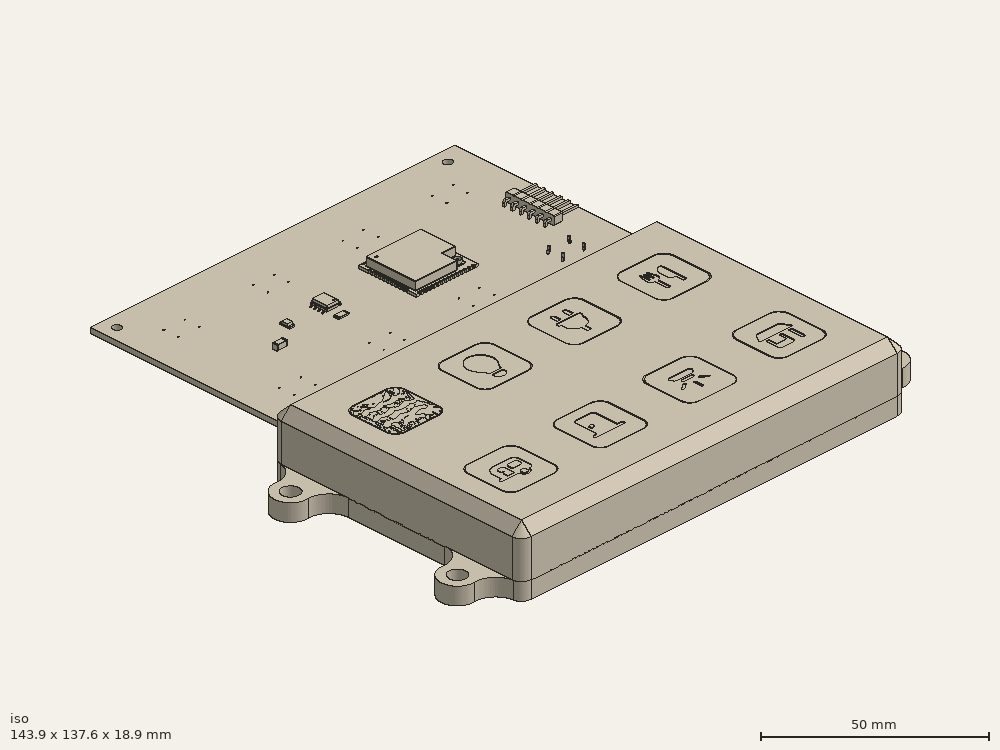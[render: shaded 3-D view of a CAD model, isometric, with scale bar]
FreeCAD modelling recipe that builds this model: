
FCSTD DOCUMENT  (FreeCAD 1.1R20260223 (Git shallow))
Label: trailer-switch-panel-eight-buttons
License: All rights reserved
LicenseURL: https://en.wikipedia.org/wiki/All_rights_reserved
objects: App::Link×73, Sketcher::SketchObject×42, Part::Feature×32, PartDesign::Pad×27, App::Point×24, PartDesign::Pocket×23, App::Part×12, PartDesign::Plane×11, PartDesign::Body×11, App::VarSet×9, PartDesign::Thickness×9, PartDesign::AdditivePipe×9, Part::Part2DObjectPython×8, PartDesign::SubShapeBinder×3, App::FeaturePython×3, PartDesign::CoordinateSystem×2, PartDesign::Mirrored×2, PartDesign::Fillet×2, Assembly::JointGroup×1, Assembly::AssemblyObject×1, +1 more types
note: 368 computed .brp shape members not serialized (recipe doc carries the construction recipe); baked Part::Feature solids carry a one-line shape summary decoded from their .brp

FEATURE [PartDesign::CoordinateSystem] Local_CS_cc27
  AttacherType = Attacher::AttachEngine3D
  MapMode = 2
FEATURE [Part::Feature] Pcb_cc27
  Placement = pos=(-24.2366,113.11,0) rot=(0,0,1;0rad)
  shape: bbox 113.4 x 65.77 x 1.6 mm, 60 faces (baked)
FEATURE [Sketcher::SketchObject] PCB_Sketch_cc27
  ArcFitTolerance = 1e-06
  ExternalTypes = [0]
  FullyConstrained = false
  MakeInternals = false
  sketch-geometry (8):
    g0: LineSegment StartX=0.45 StartY=65.81 StartZ=0 EndX=113.87 EndY=65.81 EndZ=0
    g1: LineSegment StartX=113.87 StartY=65.81 StartZ=0 EndX=113.87 EndY=0.04 EndZ=0
    g2: LineSegment StartX=113.87 StartY=0.04 StartZ=0 EndX=0.45 EndY=0.04 EndZ=0
    g3: LineSegment StartX=0.45 StartY=0.04 StartZ=0 EndX=0.45 EndY=65.81 EndZ=0
    g4: Circle CenterX=4.51408 CenterY=61.5799 CenterZ=0 NormalX=0 NormalY=0 NormalZ=1 AngleXU=0 Radius=1.25
    g5: Circle CenterX=107.514 CenterY=61.5799 CenterZ=0 NormalX=0 NormalY=0 NormalZ=1 AngleXU=0 Radius=1.25
    g6: Circle CenterX=107.514 CenterY=5.02733 CenterZ=0 NormalX=0 NormalY=0 NormalZ=1 AngleXU=0 Radius=1.25
    g7: Circle CenterX=4.51408 CenterY=5.02733 CenterZ=0 NormalX=0 NormalY=0 NormalZ=1 AngleXU=0 Radius=1.25
  constraints (4):
    c: Coincident(g2,g3)
    c: Coincident(g0,g3)
    c: Coincident(g1,g2)
    c: Coincident(g0,g1)
FEATURE [App::Part] Board_Geoms_cc27
  Group = -> [Pcb_cc27,PCB_Sketch_cc27]
  Origin = -> Origin
FEATURE [Part::Feature] Shape  label="C6_C_1206_3216Metric_fe8f5ab1829c"
  Placement = pos=(23.5634,30.042,0) rot=(0,0,1;3.14159rad)
  shape: bbox 3.2 x 1.6 x 1.6 mm, 28 faces (baked)
FEATURE [Part::Feature] Shape001  label="U1_ESP32-WROOM-32U_0b53285c672d"
  Placement = pos=(69.99,33.305,0) rot=(0,0,-1;1.5708rad)
  shape: bbox 19.2 x 18 x 3.2 mm, 766 faces (baked)
FEATURE [Part::Feature] Shape002  label="U2_SOIC_8_39x49mm_P127mm_6befcaffebcc"
  Placement = pos=(43.625,35.8786,0) rot=(0,0,1;3.14159rad)
  shape: bbox 6 x 4.9 x 1.75 mm, 156 faces (baked)
FEATURE [App::Link] C6_C_1206_3216Metric_fe8f5ab1829c_ln_  label="C5_C_1206_3216Metric_921661c36668"
  LinkPlacement = pos=(23.5634,32.484,0) rot=(0,0,1;3.14159rad)
  LinkedObject = -> Shape
  Placement = pos=(23.5634,32.484,0) rot=(0,0,1;3.14159rad)
FEATURE [App::Link] C6_C_1206_3216Metric_fe8f5ab1829c_ln_001  label="C4_C_1206_3216Metric_1d953bd43f95"
  LinkPlacement = pos=(18.375,36.646,0) rot=(0,0,1;0rad)
  LinkedObject = -> Shape
  Placement = pos=(18.375,36.646,0) rot=(0,0,1;0rad)
FEATURE [App::Link] C6_C_1206_3216Metric_fe8f5ab1829c_ln_002  label="C3_C_1206_3216Metric_0d3c0877bab4"
  LinkPlacement = pos=(18.375,29.28,0) rot=(0,0,1;0rad)
  LinkedObject = -> Shape
  Placement = pos=(18.375,29.28,0) rot=(0,0,1;0rad)
FEATURE [Part::Feature] Shape003  label="R4_R_1206_3216Metric_a98f0a8b4acf"
  Placement = pos=(42.97,30.25,0) rot=(0,0,1;3.14159rad)
  shape: bbox 3.2 x 1.6 x 0.55 mm, 26 faces (baked)
FEATURE [Part::Feature] Part__Feature  label="AP63203WU-7"
  shape: bbox 0.65 x 0.63 x 0.375 mm, 14 faces (baked)
FEATURE [Part::Feature] Part__Feature001  label="AP63203WU-008"
  shape: bbox 0.65 x 0.63 x 0.375 mm, 14 faces (baked)
FEATURE [Part::Feature] Part__Feature002  label="AP63203WU-009"
  shape: bbox 0.65 x 0.63 x 0.375 mm, 14 faces (baked)
FEATURE [Part::Feature] Part__Feature003  label="AP63203WU-010"
  shape: bbox 0.65 x 0.63 x 0.375 mm, 14 faces (baked)
FEATURE [Part::Feature] Part__Feature004  label="AP63203WU-011"
  shape: bbox 0.65 x 0.63 x 0.375 mm, 14 faces (baked)
FEATURE [Part::Feature] Part__Feature005  label="AP63203WU-012"
  shape: bbox 0.65 x 0.63 x 0.375 mm, 14 faces (baked)
FEATURE [Part::Feature] Part__Feature006  label="AP63203WU-013"
  shape: bbox 1.601 x 0.9 x 2.901 mm, 45 faces (baked)
FEATURE [Part::Feature] Part__Feature007  label="AP63203WU-014"
  shape: bbox 0.2 x 0.05 x 0.2 mm, 4 faces (baked)
FEATURE [App::Part] AP63203WU_7  label="IC1_AP63203WU-015_b8c35da43584"
  Group = -> [Part__Feature,Part__Feature001,Part__Feature002,Part__Feature003,Part__Feature004,Part__Feature005,Part__Feature006,Part__Feature007]
  Origin = -> Origin008
  Placement = pos=(18.126,32.96,0) rot=(1,0,0;1.5708rad)
FEATURE [App::Link] R4_R_1206_3216Metric_a98f0a8b4acf_ln_  label="R1_R_1206_3216Metric_0d48a55c24de"
  LinkPlacement = pos=(92.55,43.89,0) rot=(0,0,1;1.5708rad)
  LinkedObject = -> Shape003
  Placement = pos=(92.55,43.89,0) rot=(0,0,1;1.5708rad)
FEATURE [App::Link] C6_C_1206_3216Metric_fe8f5ab1829c_ln_003  label="C1_C_1206_3216Metric_20d4e43c8e49"
  LinkPlacement = pos=(85.52,41.17,0) rot=(0,0,1;3.14159rad)
  LinkedObject = -> Shape
  Placement = pos=(85.52,41.17,0) rot=(0,0,1;3.14159rad)
FEATURE [App::Link] R4_R_1206_3216Metric_a98f0a8b4acf_ln_001  label="R2_R_1206_3216Metric_7877a5f10d37"
  LinkPlacement = pos=(31.62,30.71,0) rot=(0,0,1;1.5708rad)
  LinkedObject = -> Shape003
  Placement = pos=(31.62,30.71,0) rot=(0,0,1;1.5708rad)
FEATURE [Part::Feature] Shape004  label="J1_PinHeader_1x06_P254mm_Horizontal_6c59025dd184"
  Placement = pos=(102.61,39.06,0) rot=(0,0,1;0rad)
  shape: bbox 10.36 x 15.24 x 5.54 mm, 166 faces (baked)
FEATURE [App::Link] C6_C_1206_3216Metric_fe8f5ab1829c_ln_004  label="C2_C_1206_3216Metric_1073df5edb1d"
  LinkPlacement = pos=(85.52,43.71,0) rot=(0,0,1;3.14159rad)
  LinkedObject = -> Shape
  Placement = pos=(85.52,43.71,0) rot=(0,0,1;3.14159rad)
FEATURE [Part::Feature] Shape005  label="D1_LED_1206_3216Metric_5818a68925bf"
  Placement = pos=(31.6022,35.7369,0) rot=(0,0,-1;1.5708rad)
  shape: bbox 1.6 x 3.2 x 1.1 mm, 50 faces (baked)
FEATURE [App::Link] R4_R_1206_3216Metric_a98f0a8b4acf_ln_002  label="R12_R_1206_3216Metric_9a77f9e92562"
  LinkPlacement = pos=(107.28,49.04,0) rot=(0,0,1;0rad)
  LinkedObject = -> Shape003
  Placement = pos=(107.28,49.04,0) rot=(0,0,1;0rad)
FEATURE [App::Part] Top_cc27
  Group = -> [Shape,Shape001,Shape002,C6_C_1206_3216Metric_fe8f5ab1829c_ln_,C6_C_1206_3216Metric_fe8f5ab1829c_ln_001,C6_C_1206_3216Metric_fe8f5ab1829c_ln_002,Shape003,AP63203WU_7,R4_R_1206_3216Metric_a98f0a8b4acf_ln_,C6_C_1206_3216Metric_fe8f5ab1829c_ln_003,R4_R_1206_3216Metric_a98f0a8b4acf_ln_001,Shape004,C6_C_1206_3216Metric_fe8f5ab1829c_ln_004,Shape005,R4_R_1206_3216Metric_a98f0a8b4acf_ln_002]
  Origin = -> Origin003
FEATURE [App::Link] R4_R_1206_3216Metric_a98f0a8b4acf_ln_003  label="R10_R_1206_3216Metric_955bf38eb66b"
  LinkPlacement = pos=(63.83,5.8,-1.6) rot=(1,0,0;3.14159rad)
  LinkedObject = -> Shape003
  Placement = pos=(63.83,5.8,-1.6) rot=(1,0,0;3.14159rad)
FEATURE [App::Link] D1_LED_1206_3216Metric_5818a68925bf_ln_  label="D7_LED_1206_3216Metric_e0f900cdbb9d"
  LinkPlacement = pos=(42.1175,5.8,-1.6) rot=(0,1,0;3.14159rad)
  LinkedObject = -> Shape005
  Placement = pos=(42.1175,5.8,-1.6) rot=(0,1,0;3.14159rad)
FEATURE [App::Link] D1_LED_1206_3216Metric_5818a68925bf_ln_001  label="D8_LED_1206_3216Metric_4590835c06e2"
  LinkPlacement = pos=(69.9575,5.8,-1.6) rot=(0,1,0;3.14159rad)
  LinkedObject = -> Shape005
  Placement = pos=(69.9575,5.8,-1.6) rot=(0,1,0;3.14159rad)
FEATURE [App::Link] R4_R_1206_3216Metric_a98f0a8b4acf_ln_004  label="R8_R_1206_3216Metric_c4d4031c6124"
  LinkPlacement = pos=(9.39,7.35,-1.6) rot=(0.707107,-0.707107,0;3.14159rad)
  LinkedObject = -> Shape003
  Placement = pos=(9.39,7.35,-1.6) rot=(0.707107,-0.707107,0;3.14159rad)
FEATURE [Part::Feature] Shape006  label="SW8_SW_PUSH_6mm_76d8f6a7f289"
  Placement = pos=(101.07,17.5,-1.6) rot=(0,1,0;3.14159rad)
  shape: bbox 7.174 x 6 x 7.8 mm, 105 faces (baked)
FEATURE [App::Link] R4_R_1206_3216Metric_a98f0a8b4acf_ln_005  label="R3_R_1206_3216Metric_c80006f71293"
  LinkPlacement = pos=(92.2,61.31,-1.6) rot=(1,0,0;3.14159rad)
  LinkedObject = -> Shape003
  Placement = pos=(92.2,61.31,-1.6) rot=(1,0,0;3.14159rad)
FEATURE [App::Link] R4_R_1206_3216Metric_a98f0a8b4acf_ln_006  label="R7_R_1206_3216Metric_6f705efabba0"
  LinkPlacement = pos=(20.25,61.26,-1.6) rot=(0,1,0;3.14159rad)
  LinkedObject = -> Shape003
  Placement = pos=(20.25,61.26,-1.6) rot=(0,1,0;3.14159rad)
FEATURE [App::Link] SW8_SW_PUSH_6mm_76d8f6a7f289_ln_  label="SW5_SW_PUSH_6mm_bc2679ab0c28"
  LinkPlacement = pos=(17.55,17.5,-1.6) rot=(0,1,0;3.14159rad)
  LinkedObject = -> Shape006
  Placement = pos=(17.55,17.5,-1.6) rot=(0,1,0;3.14159rad)
FEATURE [App::Link] D1_LED_1206_3216Metric_5818a68925bf_ln_002  label="D9_LED_1206_3216Metric_f97e9ca9ca0c"
  LinkPlacement = pos=(97.7975,5.8,-1.6) rot=(1,0,0;3.14159rad)
  LinkedObject = -> Shape005
  Placement = pos=(97.7975,5.8,-1.6) rot=(1,0,0;3.14159rad)
FEATURE [App::Link] R4_R_1206_3216Metric_a98f0a8b4acf_ln_007  label="R6_R_1206_3216Metric_4dd85524e60b"
  LinkPlacement = pos=(48.42,61.26,-1.6) rot=(0,1,0;3.14159rad)
  LinkedObject = -> Shape003
  Placement = pos=(48.42,61.26,-1.6) rot=(0,1,0;3.14159rad)
FEATURE [App::Link] R4_R_1206_3216Metric_a98f0a8b4acf_ln_008  label="R5_R_1206_3216Metric_5aff5c873fbb"
  LinkPlacement = pos=(75.86,61.27,-1.6) rot=(0,1,0;3.14159rad)
  LinkedObject = -> Shape003
  Placement = pos=(75.86,61.27,-1.6) rot=(0,1,0;3.14159rad)
FEATURE [App::Link] SW8_SW_PUSH_6mm_76d8f6a7f289_ln_001  label="SW7_SW_PUSH_6mm_98a993c83935"
  LinkPlacement = pos=(73.23,17.5,-1.6) rot=(0,1,0;3.14159rad)
  LinkedObject = -> Shape006
  Placement = pos=(73.23,17.5,-1.6) rot=(0,1,0;3.14159rad)
FEATURE [App::Link] SW8_SW_PUSH_6mm_76d8f6a7f289_ln_002  label="SW6_SW_PUSH_6mm_e97d2eab9daa"
  LinkPlacement = pos=(45.39,17.5,-1.6) rot=(0,1,0;3.14159rad)
  LinkedObject = -> Shape006
  Placement = pos=(45.39,17.5,-1.6) rot=(0,1,0;3.14159rad)
FEATURE [App::Link] D1_LED_1206_3216Metric_5818a68925bf_ln_003  label="D4_LED_1206_3216Metric_98b5ea636a78"
  LinkPlacement = pos=(42.1625,61.26,-1.6) rot=(1,0,0;3.14159rad)
  LinkedObject = -> Shape005
  Placement = pos=(42.1625,61.26,-1.6) rot=(1,0,0;3.14159rad)
FEATURE [App::Link] D1_LED_1206_3216Metric_5818a68925bf_ln_004  label="D2_LED_1206_3216Metric_2fa2df955063"
  LinkPlacement = pos=(97.7975,61.26,-1.6) rot=(0,1,0;3.14159rad)
  LinkedObject = -> Shape005
  Placement = pos=(97.7975,61.26,-1.6) rot=(0,1,0;3.14159rad)
FEATURE [App::Link] SW8_SW_PUSH_6mm_76d8f6a7f289_ln_003  label="SW2_SW_PUSH_6mm_e1b948049a03"
  LinkPlacement = pos=(66.73,49.03,-1.6) rot=(1,0,0;3.14159rad)
  LinkedObject = -> Shape006
  Placement = pos=(66.73,49.03,-1.6) rot=(1,0,0;3.14159rad)
FEATURE [App::Link] R4_R_1206_3216Metric_a98f0a8b4acf_ln_009  label="R11_R_1206_3216Metric_e90fbb06c50b"
  LinkPlacement = pos=(104,8.6,-1.6) rot=(0.707107,-0.707107,0;3.14159rad)
  LinkedObject = -> Shape003
  Placement = pos=(104,8.6,-1.6) rot=(0.707107,-0.707107,0;3.14159rad)
FEATURE [App::Link] SW8_SW_PUSH_6mm_76d8f6a7f289_ln_004  label="SW1_SW_PUSH_6mm_846872bf3f2a"
  LinkPlacement = pos=(94.57,49.03,-1.6) rot=(1,0,0;3.14159rad)
  LinkedObject = -> Shape006
  Placement = pos=(94.57,49.03,-1.6) rot=(1,0,0;3.14159rad)
FEATURE [App::Link] SW8_SW_PUSH_6mm_76d8f6a7f289_ln_005  label="SW3_SW_PUSH_6mm_786fe8b935ec"
  LinkPlacement = pos=(38.89,49.03,-1.6) rot=(1,0,0;3.14159rad)
  LinkedObject = -> Shape006
  Placement = pos=(38.89,49.03,-1.6) rot=(1,0,0;3.14159rad)
FEATURE [App::Link] D1_LED_1206_3216Metric_5818a68925bf_ln_005  label="D6_LED_1206_3216Metric_e89784457430"
  LinkPlacement = pos=(14.3225,5.8,-1.6) rot=(0,1,0;3.14159rad)
  LinkedObject = -> Shape005
  Placement = pos=(14.3225,5.8,-1.6) rot=(0,1,0;3.14159rad)
FEATURE [App::Link] D1_LED_1206_3216Metric_5818a68925bf_ln_006  label="D5_LED_1206_3216Metric_64f8a7d577f6"
  LinkPlacement = pos=(14.3225,61.26,-1.6) rot=(1,0,0;3.14159rad)
  LinkedObject = -> Shape005
  Placement = pos=(14.3225,61.26,-1.6) rot=(1,0,0;3.14159rad)
FEATURE [App::Link] D1_LED_1206_3216Metric_5818a68925bf_ln_007  label="D3_LED_1206_3216Metric_db0b37632ff3"
  LinkPlacement = pos=(70.0025,61.26,-1.6) rot=(1,0,0;3.14159rad)
  LinkedObject = -> Shape005
  Placement = pos=(70.0025,61.26,-1.6) rot=(1,0,0;3.14159rad)
FEATURE [App::Link] R4_R_1206_3216Metric_a98f0a8b4acf_ln_010  label="R9_R_1206_3216Metric_fd9422578c86"
  LinkPlacement = pos=(35.88,5.8,-1.6) rot=(1,0,0;3.14159rad)
  LinkedObject = -> Shape003
  Placement = pos=(35.88,5.8,-1.6) rot=(1,0,0;3.14159rad)
FEATURE [App::Link] SW8_SW_PUSH_6mm_76d8f6a7f289_ln_006  label="SW4_SW_PUSH_6mm_2c4766872f97"
  LinkPlacement = pos=(11.05,49.03,-1.6) rot=(1,0,0;3.14159rad)
  LinkedObject = -> Shape006
  Placement = pos=(11.05,49.03,-1.6) rot=(1,0,0;3.14159rad)
FEATURE [App::Part] Bot_cc27
  Group = -> [R4_R_1206_3216Metric_a98f0a8b4acf_ln_003,D1_LED_1206_3216Metric_5818a68925bf_ln_,D1_LED_1206_3216Metric_5818a68925bf_ln_001,R4_R_1206_3216Metric_a98f0a8b4acf_ln_004,Shape006,R4_R_1206_3216Metric_a98f0a8b4acf_ln_005,R4_R_1206_3216Metric_a98f0a8b4acf_ln_006,SW8_SW_PUSH_6mm_76d8f6a7f289_ln_,D1_LED_1206_3216Metric_5818a68925bf_ln_002,R4_R_1206_3216Metric_a98f0a8b4acf_ln_007,+14 more]
  Origin = -> Origin004
FEATURE [App::Part] Step_Models_cc27
  Group = -> [Top_cc27,Bot_cc27]
  Origin = -> Origin002
FEATURE [App::Part] Board_cc27  label="trailer-switch-panel-eight-buttons"
  Group = -> [Local_CS_cc27,Board_Geoms_cc27,Step_Models_cc27]
  Origin = -> Origin001
  Placement = pos=(0,0,0) rot=(1,0,0;3.14159rad)
FEATURE [PartDesign::SubShapeBinder] Binder006  label="BinderPcb001"
  BindCopyOnChange = 0
  BindMode = 0
  ClaimChildren = false
  Context = -> Body003 [Binder006.]
  Fuse = false
  MakeFace = true
  OffsetFill = false
  OffsetIntersection = false
  OffsetJoinType = 0
  OffsetOpenResult = false
  PartialLoad = false
  Placement = pos=(0,0,-3.64) rot=(0,0,1;0rad)
  Refine = true
  Relative = true
  Support = -> [Board_cc27]
  _Version = 2
FEATURE [Sketcher::SketchObject] Sketch033  label="SketchBackPlateToCover"
  ArcFitTolerance = 1e-06
  AttachmentSupport = -> [XY_Plane013]
  ExternalGeometry = -> [Binder006]
  ExternalTypes = [0]
  FullyConstrained = true
  MakeInternals = false
  MapMode = 5
  expr: Constraints[19] = <<VarSetButtonDimensions>>.Base_button_width + <<VarSetButtonDimensions>>.tolerance
  expr: Constraints[20] = <<VarSetButtonDimensions>>.Base_button_height + <<VarSetButtonDimensions>>.tolerance
  expr: Constraints[33] = <<VarSetButtonDimensions>>.Base_button_radius
  sketch-geometry (84):
    g0: LineSegment StartX=6.2 StartY=-10.05 StartZ=0 EndX=6.2 EndY=-20.45 EndZ=0
    g1: LineSegment StartX=9.2 StartY=-23.45 StartZ=0 EndX=19.6 EndY=-23.45 EndZ=0
    g2: LineSegment StartX=22.6 StartY=-20.45 StartZ=0 EndX=22.6 EndY=-10.05 EndZ=0
    g3: LineSegment StartX=19.6 StartY=-7.05 StartZ=0 EndX=9.2 EndY=-7.05 EndZ=0
    g4: ArcOfCircle CenterX=9.2 CenterY=-10.05 CenterZ=0 NormalX=0 NormalY=0 NormalZ=1 AngleXU=0 Radius=3 StartAngle=1.5708 EndAngle=3.14159
    g5: ArcOfCircle CenterX=9.2 CenterY=-20.45 CenterZ=0 NormalX=0 NormalY=0 NormalZ=1 AngleXU=0 Radius=3 StartAngle=3.14159 EndAngle=4.71239
    g6: ArcOfCircle CenterX=19.6 CenterY=-20.45 CenterZ=0 NormalX=0 NormalY=0 NormalZ=1 AngleXU=0 Radius=3 StartAngle=4.71239 EndAngle=6.28319
    g7: ArcOfCircle CenterX=19.6 CenterY=-10.05 CenterZ=0 NormalX=0 NormalY=0 NormalZ=1 AngleXU=0 Radius=3 StartAngle=6e-16 EndAngle=1.5708
    g8: GeomPoint [constr] X=6.2 Y=-7.05 Z=0
    g9: GeomPoint [constr] X=22.6 Y=-23.45 Z=0
    g10: LineSegment StartX=-3 StartY=6 StartZ=0 EndX=-3 EndY=-71.81 EndZ=0
    g11: LineSegment StartX=-3 StartY=-71.81 StartZ=0 EndX=116.87 EndY=-71.81 EndZ=0
    g12: LineSegment StartX=116.87 StartY=-71.81 StartZ=0 EndX=116.87 EndY=6 EndZ=0
    g13: LineSegment StartX=116.87 StartY=6 StartZ=0 EndX=-3 EndY=6 EndZ=0
    g14: LineSegment StartX=34.04 StartY=-10.05 StartZ=0 EndX=34.04 EndY=-20.45 EndZ=0
    g15: LineSegment StartX=37.04 StartY=-23.45 StartZ=0 EndX=47.44 EndY=-23.45 EndZ=0
    g16: LineSegment StartX=50.44 StartY=-20.45 StartZ=0 EndX=50.44 EndY=-10.05 EndZ=0
    g17: LineSegment StartX=47.44 StartY=-7.05 StartZ=0 EndX=37.04 EndY=-7.05 EndZ=0
    g18: ArcOfCircle CenterX=37.04 CenterY=-10.05 CenterZ=0 NormalX=0 NormalY=0 NormalZ=1 AngleXU=0 Radius=3 StartAngle=1.5708 EndAngle=3.14159
    g19: ArcOfCircle CenterX=37.04 CenterY=-20.45 CenterZ=0 NormalX=0 NormalY=0 NormalZ=1 AngleXU=0 Radius=3 StartAngle=3.14159 EndAngle=4.71239
    g20: ArcOfCircle CenterX=47.44 CenterY=-20.45 CenterZ=0 NormalX=0 NormalY=0 NormalZ=1 AngleXU=0 Radius=3 StartAngle=4.71239 EndAngle=6.28319
    g21: ArcOfCircle CenterX=47.44 CenterY=-10.05 CenterZ=0 NormalX=0 NormalY=0 NormalZ=1 AngleXU=0 Radius=3 StartAngle=0 EndAngle=1.5708
    g22: GeomPoint [constr] X=50.44 Y=-23.45 Z=0
    g23: GeomPoint [constr] X=42.24 Y=-15.25 Z=0
    g24: LineSegment StartX=61.88 StartY=-10.05 StartZ=0 EndX=61.88 EndY=-20.45 EndZ=0
    g25: LineSegment StartX=64.88 StartY=-23.45 StartZ=0 EndX=75.28 EndY=-23.45 EndZ=0
    g26: LineSegment StartX=78.28 StartY=-20.45 StartZ=0 EndX=78.28 EndY=-10.05 EndZ=0
    g27: LineSegment StartX=75.28 StartY=-7.05 StartZ=0 EndX=64.88 EndY=-7.05 EndZ=0
    g28: ArcOfCircle CenterX=64.88 CenterY=-10.05 CenterZ=0 NormalX=0 NormalY=0 NormalZ=1 AngleXU=0 Radius=3 StartAngle=1.5708 EndAngle=3.14159
    g29: ArcOfCircle CenterX=64.88 CenterY=-20.45 CenterZ=0 NormalX=0 NormalY=0 NormalZ=1 AngleXU=0 Radius=3 StartAngle=3.14159 EndAngle=4.71239
    g30: ArcOfCircle CenterX=75.28 CenterY=-20.45 CenterZ=0 NormalX=0 NormalY=0 NormalZ=1 AngleXU=0 Radius=3 StartAngle=4.71239 EndAngle=6.28319
    g31: ArcOfCircle CenterX=75.28 CenterY=-10.05 CenterZ=0 NormalX=0 NormalY=0 NormalZ=1 AngleXU=0 Radius=3 StartAngle=1e-16 EndAngle=1.5708
    g32: GeomPoint [constr] X=78.28 Y=-23.45 Z=0
    g33: GeomPoint [constr] X=70.08 Y=-15.25 Z=0
    g34: LineSegment StartX=89.72 StartY=-10.05 StartZ=0 EndX=89.72 EndY=-20.45 EndZ=0
    g35: LineSegment StartX=92.72 StartY=-23.45 StartZ=0 EndX=103.12 EndY=-23.45 EndZ=0
    g36: LineSegment StartX=106.12 StartY=-20.45 StartZ=0 EndX=106.12 EndY=-10.05 EndZ=0
    g37: LineSegment StartX=103.12 StartY=-7.05 StartZ=0 EndX=92.72 EndY=-7.05 EndZ=0
    g38: ArcOfCircle CenterX=92.72 CenterY=-10.05 CenterZ=0 NormalX=0 NormalY=0 NormalZ=1 AngleXU=0 Radius=3 StartAngle=1.5708 EndAngle=3.14159
    g39: ArcOfCircle CenterX=92.72 CenterY=-20.45 CenterZ=0 NormalX=0 NormalY=0 NormalZ=1 AngleXU=0 Radius=3 StartAngle=3.14159 EndAngle=4.71239
    g40: ArcOfCircle CenterX=103.12 CenterY=-20.45 CenterZ=0 NormalX=0 NormalY=0 NormalZ=1 AngleXU=0 Radius=3 StartAngle=4.71239 EndAngle=6.28319
    g41: ArcOfCircle CenterX=103.12 CenterY=-10.05 CenterZ=0 NormalX=0 NormalY=0 NormalZ=1 AngleXU=0 Radius=3 StartAngle=3e-16 EndAngle=1.5708
    g42: GeomPoint [constr] X=106.12 Y=-23.45 Z=0
    g43: GeomPoint [constr] X=97.92 Y=-15.25 Z=0
    g44: LineSegment StartX=6 StartY=-46.08 StartZ=0 EndX=6 EndY=-56.48 EndZ=0
    g45: LineSegment StartX=9 StartY=-59.48 StartZ=0 EndX=19.4 EndY=-59.48 EndZ=0
    g46: LineSegment StartX=22.4 StartY=-56.48 StartZ=0 EndX=22.4 EndY=-46.08 EndZ=0
    g47: LineSegment StartX=19.4 StartY=-43.08 StartZ=0 EndX=9 EndY=-43.08 EndZ=0
    g48: ArcOfCircle CenterX=9 CenterY=-46.08 CenterZ=0 NormalX=0 NormalY=0 NormalZ=1 AngleXU=0 Radius=3 StartAngle=1.5708 EndAngle=3.14159
    g49: ArcOfCircle CenterX=9 CenterY=-56.48 CenterZ=0 NormalX=0 NormalY=0 NormalZ=1 AngleXU=0 Radius=3 StartAngle=3.14159 EndAngle=4.71239
    g50: ArcOfCircle CenterX=19.4 CenterY=-56.48 CenterZ=0 NormalX=0 NormalY=0 NormalZ=1 AngleXU=0 Radius=3 StartAngle=4.71239 EndAngle=6.28319
    g51: ArcOfCircle CenterX=19.4 CenterY=-46.08 CenterZ=0 NormalX=0 NormalY=0 NormalZ=1 AngleXU=0 Radius=3 StartAngle=9e-16 EndAngle=1.5708
    g52: GeomPoint [constr] X=22.4 Y=-59.48 Z=0
    g53: GeomPoint [constr] X=14.2 Y=-51.28 Z=0
    g54: LineSegment StartX=33.84 StartY=-46.08 StartZ=0 EndX=33.84 EndY=-56.48 EndZ=0
    g55: LineSegment StartX=36.84 StartY=-59.48 StartZ=0 EndX=47.24 EndY=-59.48 EndZ=0
    g56: LineSegment StartX=50.24 StartY=-56.48 StartZ=0 EndX=50.24 EndY=-46.08 EndZ=0
    g57: LineSegment StartX=47.24 StartY=-43.08 StartZ=0 EndX=36.84 EndY=-43.08 EndZ=0
    g58: ArcOfCircle CenterX=36.84 CenterY=-46.08 CenterZ=0 NormalX=0 NormalY=0 NormalZ=1 AngleXU=0 Radius=3 StartAngle=1.5708 EndAngle=3.14159
    g59: ArcOfCircle CenterX=36.84 CenterY=-56.48 CenterZ=0 NormalX=0 NormalY=0 NormalZ=1 AngleXU=0 Radius=3 StartAngle=3.14159 EndAngle=4.71239
    g60: ArcOfCircle CenterX=47.24 CenterY=-56.48 CenterZ=0 NormalX=0 NormalY=0 NormalZ=1 AngleXU=0 Radius=3 StartAngle=4.71239 EndAngle=6.28319
    g61: ArcOfCircle CenterX=47.24 CenterY=-46.08 CenterZ=0 NormalX=0 NormalY=0 NormalZ=1 AngleXU=0 Radius=3 StartAngle=7e-16 EndAngle=1.5708
    g62: GeomPoint [constr] X=50.24 Y=-59.48 Z=0
    g63: GeomPoint [constr] X=42.04 Y=-51.28 Z=0
    g64: LineSegment StartX=61.68 StartY=-46.08 StartZ=0 EndX=61.68 EndY=-56.48 EndZ=0
    g65: LineSegment StartX=64.68 StartY=-59.48 StartZ=0 EndX=75.08 EndY=-59.48 EndZ=0
    g66: LineSegment StartX=78.08 StartY=-56.48 StartZ=0 EndX=78.08 EndY=-46.08 EndZ=0
    g67: LineSegment StartX=75.08 StartY=-43.08 StartZ=0 EndX=64.68 EndY=-43.08 EndZ=0
    g68: ArcOfCircle CenterX=64.68 CenterY=-46.08 CenterZ=0 NormalX=0 NormalY=0 NormalZ=1 AngleXU=0 Radius=3 StartAngle=1.5708 EndAngle=3.14159
    g69: ArcOfCircle CenterX=64.68 CenterY=-56.48 CenterZ=0 NormalX=0 NormalY=0 NormalZ=1 AngleXU=0 Radius=3 StartAngle=3.14159 EndAngle=4.71239
    g70: ArcOfCircle CenterX=75.08 CenterY=-56.48 CenterZ=0 NormalX=0 NormalY=0 NormalZ=1 AngleXU=0 Radius=3 StartAngle=4.71239 EndAngle=6.28319
    g71: ArcOfCircle CenterX=75.08 CenterY=-46.08 CenterZ=0 NormalX=0 NormalY=0 NormalZ=1 AngleXU=0 Radius=3 StartAngle=9e-16 EndAngle=1.5708
    g72: GeomPoint [constr] X=78.08 Y=-59.48 Z=0
    g73: GeomPoint [constr] X=69.88 Y=-51.28 Z=0
    g74: LineSegment StartX=89.52 StartY=-46.08 StartZ=0 EndX=89.52 EndY=-56.48 EndZ=0
    g75: LineSegment StartX=92.52 StartY=-59.48 StartZ=0 EndX=102.92 EndY=-59.48 EndZ=0
    g76: LineSegment StartX=105.92 StartY=-56.48 StartZ=0 EndX=105.92 EndY=-46.08 EndZ=0
    g77: LineSegment StartX=102.92 StartY=-43.08 StartZ=0 EndX=92.52 EndY=-43.08 EndZ=0
    g78: ArcOfCircle CenterX=92.52 CenterY=-46.08 CenterZ=0 NormalX=0 NormalY=0 NormalZ=1 AngleXU=0 Radius=3 StartAngle=1.5708 EndAngle=3.14159
    g79: ArcOfCircle CenterX=92.52 CenterY=-56.48 CenterZ=0 NormalX=0 NormalY=0 NormalZ=1 AngleXU=0 Radius=3 StartAngle=3.14159 EndAngle=4.71239
    g80: ArcOfCircle CenterX=102.92 CenterY=-56.48 CenterZ=0 NormalX=0 NormalY=0 NormalZ=1 AngleXU=0 Radius=3 StartAngle=4.71239 EndAngle=6.28319
    g81: ArcOfCircle CenterX=102.92 CenterY=-46.08 CenterZ=0 NormalX=0 NormalY=0 NormalZ=1 AngleXU=0 Radius=3 StartAngle=6e-16 EndAngle=1.5708
    g82: GeomPoint [constr] X=105.92 Y=-59.48 Z=0
    g83: GeomPoint [constr] X=97.72 Y=-51.28 Z=0
  constraints (189):
    c: Tangent(g0,g4) = -1.5708
    c: Tangent(g0,g5) = -1.5708
    c: Tangent(g1,g5) = -1.5708
    c: Tangent(g1,g6) = -1.5708
    c: Tangent(g2,g6) = -1.5708
    c: Tangent(g2,g7) = -1.5708
    c: Tangent(g3,g7) = -1.5708
    c: Tangent(g3,g4) = -1.5708
    c: Vertical(g0)
    c: Vertical(g2)
    c: Horizontal(g1)
    c: Horizontal(g3)
    c: Equal(g4,g5)
    c: Equal(g5,g6)
    c: Equal(g6,g7)
    c: PointOnObject(g8,g0)
    c: PointOnObject(g8,g3)
    c: PointOnObject(g9,g1)
    c: PointOnObject(g9,g2)
    c: Distance(g0,g2) = 16.4
    c: Distance(g1,g3) = 16.4
    c: Coincident(g10,g11)
    c: Coincident(g11,g12)
    c: Coincident(g12,g13)
    c: Coincident(g13,g10)
    c: Vertical(g10)
    c: Vertical(g12)
    c: Horizontal(g11)
    c: Horizontal(g13)
    c: DistanceX(g10,g-1) = 3
    c: DistanceY(g-1,g10) = 6
    c: DistanceX(g-5,g11) = 3
    c: DistanceY(g11,g-5) = 6
    c: Radius(g7) = 3
    c: Symmetric(g4,g6,g-7)
    c: Tangent(g14,g18) = -1.5708
    c: Tangent(g14,g19) = -1.5708
    c: Tangent(g15,g19) = -1.5708
    c: Tangent(g15,g20) = -1.5708
    c: Tangent(g16,g20) = -1.5708
    c: Tangent(g16,g21) = -1.5708
    c: Tangent(g17,g21) = -1.5708
    c: Tangent(g17,g18) = -1.5708
    c: Vertical(g14)
    c: Vertical(g16)
    c: Horizontal(g15)
    c: Horizontal(g17)
    c: Equal(g18,g19)
    c: Equal(g19,g20)
    c: Equal(g20,g21)
    c: Symmetric(g16,g14,g23)
    c: PointOnObject(g22,g15)
    c: PointOnObject(g22,g16)
    c: Coincident(g23,g-8)
    c: Tangent(g24,g28) = -1.5708
    c: Tangent(g24,g29) = -1.5708
    c: Tangent(g25,g29) = -1.5708
    c: Tangent(g25,g30) = -1.5708
    c: Tangent(g26,g30) = -1.5708
    c: Tangent(g26,g31) = -1.5708
    c: Tangent(g27,g31) = -1.5708
    c: Tangent(g27,g28) = -1.5708
    c: Vertical(g24)
    c: Vertical(g26)
    c: Horizontal(g25)
    c: Horizontal(g27)
    c: Equal(g28,g29)
    c: Equal(g29,g30)
    c: Equal(g30,g31)
    c: Symmetric(g26,g24,g33)
    c: PointOnObject(g32,g25)
    c: PointOnObject(g32,g26)
    c: Coincident(g33,g-9)
    c: Tangent(g34,g38) = -1.5708
    c: Tangent(g34,g39) = -1.5708
    c: Tangent(g35,g39) = -1.5708
    c: Tangent(g35,g40) = -1.5708
    c: Tangent(g36,g40) = -1.5708
    c: Tangent(g36,g41) = -1.5708
    c: Tangent(g37,g41) = -1.5708
    c: Tangent(g37,g38) = -1.5708
    c: Vertical(g34)
    c: Vertical(g36)
    c: Horizontal(g35)
    c: Horizontal(g37)
    c: Equal(g38,g39)
    c: Equal(g39,g40)
    c: Equal(g40,g41)
    c: Symmetric(g36,g34,g43)
    c: PointOnObject(g42,g35)
    c: PointOnObject(g42,g36)
    c: Coincident(g43,g-10)
    c: Tangent(g44,g48) = -1.5708
    c: Tangent(g44,g49) = -1.5708
    c: Tangent(g45,g49) = -1.5708
    c: Tangent(g45,g50) = -1.5708
    c: Tangent(g46,g50) = -1.5708
    c: Tangent(g46,g51) = -1.5708
    c: Tangent(g47,g51) = -1.5708
    c: Tangent(g47,g48) = -1.5708
    c: Vertical(g44)
    c: Vertical(g46)
    c: Horizontal(g45)
    c: Horizontal(g47)
    c: Equal(g48,g49)
    c: Equal(g49,g50)
    c: Equal(g50,g51)
    c: Symmetric(g46,g44,g53)
    c: PointOnObject(g52,g45)
    c: PointOnObject(g52,g46)
    c: Coincident(g53,g-14)
    c: Tangent(g54,g58) = -1.5708
    c: Tangent(g54,g59) = -1.5708
    c: Tangent(g55,g59) = -1.5708
    c: Tangent(g55,g60) = -1.5708
    c: Tangent(g56,g60) = -1.5708
    c: Tangent(g56,g61) = -1.5708
    c: Tangent(g57,g61) = -1.5708
    c: Tangent(g57,g58) = -1.5708
    c: Vertical(g54)
    c: Vertical(g56)
    c: Horizontal(g55)
    c: Horizontal(g57)
    c: Equal(g58,g59)
    c: Equal(g59,g60)
    c: Equal(g60,g61)
    c: Symmetric(g56,g54,g63)
    c: PointOnObject(g62,g55)
    c: PointOnObject(g62,g56)
    c: Coincident(g63,g-13)
    c: Tangent(g64,g68) = -1.5708
    c: Tangent(g64,g69) = -1.5708
    c: Tangent(g65,g69) = -1.5708
    c: Tangent(g65,g70) = -1.5708
    c: Tangent(g66,g70) = -1.5708
    c: Tangent(g66,g71) = -1.5708
    c: Tangent(g67,g71) = -1.5708
    c: Tangent(g67,g68) = -1.5708
    c: Vertical(g64)
    c: Vertical(g66)
    c: Horizontal(g65)
    c: Horizontal(g67)
    c: Equal(g68,g69)
    c: Equal(g69,g70)
    c: Equal(g70,g71)
    c: Symmetric(g66,g64,g73)
    c: PointOnObject(g72,g65)
    c: PointOnObject(g72,g66)
    c: Coincident(g73,g-12)
    c: Tangent(g74,g78) = -1.5708
    c: Tangent(g74,g79) = -1.5708
    c: Tangent(g75,g79) = -1.5708
    c: Tangent(g75,g80) = -1.5708
    c: Tangent(g76,g80) = -1.5708
    c: Tangent(g76,g81) = -1.5708
    c: Tangent(g77,g81) = -1.5708
    c: Tangent(g77,g78) = -1.5708
    c: Vertical(g74)
    c: Vertical(g76)
    c: Horizontal(g75)
    c: Horizontal(g77)
    c: Equal(g78,g79)
    c: Equal(g79,g80)
    c: Equal(g80,g81)
    c: Symmetric(g76,g74,g83)
    c: PointOnObject(g82,g75)
    c: PointOnObject(g82,g76)
    c: Coincident(g83,g-11)
    c: Equal(g4,g18)
    c: Equal(g18,g48)
    c: Equal(g48,g58)
    c: Equal(g58,g68)
    c: Equal(g68,g28)
    c: Equal(g28,g38)
    c: Equal(g38,g78)
    c: Equal(g2,g16)
    c: Equal(g16,g26)
    c: Equal(g26,g36)
    c: Equal(g36,g76)
    c: Equal(g76,g66)
    c: Equal(g66,g56)
    c: Equal(g56,g46)
    c: Equal(g3,g17)
    c: Equal(g17,g27)
    c: Equal(g27,g37)
    c: Equal(g37,g77)
    c: Equal(g77,g67)
    c: Equal(g67,g57)
    c: Equal(g57,g47)
FEATURE [App::VarSet] VarSet002  label="VarSetButtonDimensions"
  Base_base_thickness = 1.5
  Base_button_height = 16
  Base_button_radius = 3
  Base_button_slide_depth = 0.09
  Base_button_width = 16
  button_cap_height = 3
  button_cap_wall_thickness = 1.5
  button_snap_thickness = 0.5
  button_tab_depth = 1
  tolerance = 0.4
FEATURE [PartDesign::Pad] Pad024  label="PadOuterWalls"
  Direction = (0,0,1)
  Length = 1.5
  Length2 = 10
  Profile = -> Sketch033
  ReferenceAxis = -> Sketch033 [N_Axis]
  Refine = true
  SideType = 0
  Suppressed = false
  Type = 0
  Type2 = 0
  expr: Length = <<VarSetButtonDimensions>>.Base_base_thickness
FEATURE [Sketcher::SketchObject] Sketch034  label="SketchButtonSlide"
  ArcFitTolerance = 1e-06
  AttachmentSupport = -> [Pad024]
  ExternalGeometry = -> [Pad024]
  ExternalTypes = [0]
  FullyConstrained = true
  MakeInternals = false
  MapMode = 5
  Placement = pos=(0,0,1.5) rot=(0,0,1;0rad)
  expr: Constraints[29] = <<VarSetButtonDimensions>>.Base_button_radius
  expr: Constraints[30] = <<VarSetButtonDimensions>>.Base_button_width + <<VarSetButtonDimensions>>.tolerance + <<VarSetButtonDimensions>>.button_snap_thickness * 2 + <<VarSetButtonDimensions>>.button_tab_depth
  expr: Constraints[31] = <<VarSetButtonDimensions>>.Base_button_width + <<VarSetButtonDimensions>>.tolerance + <<VarSetButtonDimensions>>.button_snap_thickness * 2 + <<VarSetButtonDimensions>>.button_tab_depth
  sketch-geometry (93):
    g0: LineSegment StartX=-3 StartY=6 StartZ=0 EndX=-3 EndY=-71.81 EndZ=0
    g1: LineSegment StartX=-3 StartY=-71.81 StartZ=0 EndX=116.87 EndY=-71.81 EndZ=0
    g2: LineSegment StartX=116.87 StartY=-71.81 StartZ=0 EndX=116.87 EndY=6 EndZ=0
    g3: LineSegment StartX=116.87 StartY=6 StartZ=0 EndX=-3 EndY=6 EndZ=0
    g4: LineSegment StartX=5.2 StartY=-9.05 StartZ=0 EndX=5.2 EndY=-21.45 EndZ=0
    g5: LineSegment StartX=8.2 StartY=-24.45 StartZ=0 EndX=20.6 EndY=-24.45 EndZ=0
    g6: LineSegment StartX=23.6 StartY=-21.45 StartZ=0 EndX=23.6 EndY=-9.05 EndZ=0
    g7: LineSegment StartX=20.6 StartY=-6.05 StartZ=0 EndX=8.2 EndY=-6.05 EndZ=0
    g8: ArcOfCircle CenterX=8.2 CenterY=-9.05 CenterZ=0 NormalX=0 NormalY=0 NormalZ=1 AngleXU=0 Radius=3 StartAngle=1.5708 EndAngle=3.14159
    g9: ArcOfCircle CenterX=8.2 CenterY=-21.45 CenterZ=0 NormalX=0 NormalY=0 NormalZ=1 AngleXU=0 Radius=3 StartAngle=3.14159 EndAngle=4.71239
    g10: ArcOfCircle CenterX=20.6 CenterY=-21.45 CenterZ=0 NormalX=0 NormalY=0 NormalZ=1 AngleXU=0 Radius=3 StartAngle=4.71239 EndAngle=6.28319
    g11: ArcOfCircle CenterX=20.6 CenterY=-9.05 CenterZ=0 NormalX=0 NormalY=0 NormalZ=1 AngleXU=0 Radius=3 StartAngle=0 EndAngle=1.5708
    g12: GeomPoint [constr] X=5.2 Y=-6.05 Z=0
    g13: GeomPoint [constr] X=23.6 Y=-24.45 Z=0
    g14: GeomPoint X=14.4 Y=-15.25 Z=0
    g15: GeomPoint X=14.4 Y=-15.25 Z=0
    g16: LineSegment StartX=33.04 StartY=-9.05 StartZ=0 EndX=33.04 EndY=-21.45 EndZ=0
    g17: LineSegment StartX=36.04 StartY=-24.45 StartZ=0 EndX=48.44 EndY=-24.45 EndZ=0
    g18: LineSegment StartX=51.44 StartY=-21.45 StartZ=0 EndX=51.44 EndY=-9.05 EndZ=0
    g19: LineSegment StartX=48.44 StartY=-6.05 StartZ=0 EndX=36.04 EndY=-6.05 EndZ=0
    g20: ArcOfCircle CenterX=36.04 CenterY=-9.05 CenterZ=0 NormalX=0 NormalY=0 NormalZ=1 AngleXU=0 Radius=3 StartAngle=1.5708 EndAngle=3.14159
    g21: ArcOfCircle CenterX=36.04 CenterY=-21.45 CenterZ=0 NormalX=0 NormalY=0 NormalZ=1 AngleXU=0 Radius=3 StartAngle=3.14159 EndAngle=4.71239
    g22: ArcOfCircle CenterX=48.44 CenterY=-21.45 CenterZ=0 NormalX=0 NormalY=0 NormalZ=1 AngleXU=0 Radius=3 StartAngle=4.71239 EndAngle=6.28319
    g23: ArcOfCircle CenterX=48.44 CenterY=-9.05 CenterZ=0 NormalX=0 NormalY=0 NormalZ=1 AngleXU=0 Radius=3 StartAngle=0 EndAngle=1.5708
    g24: GeomPoint [constr] X=33.04 Y=-6.05 Z=0
    g25: GeomPoint [constr] X=51.44 Y=-24.45 Z=0
    g26: LineSegment StartX=60.88 StartY=-9.05 StartZ=0 EndX=60.88 EndY=-21.45 EndZ=0
    g27: LineSegment StartX=63.88 StartY=-24.45 StartZ=0 EndX=76.28 EndY=-24.45 EndZ=0
    g28: LineSegment StartX=79.28 StartY=-21.45 StartZ=0 EndX=79.28 EndY=-9.05 EndZ=0
    g29: LineSegment StartX=76.28 StartY=-6.05 StartZ=0 EndX=63.88 EndY=-6.05 EndZ=0
    g30: ArcOfCircle CenterX=63.88 CenterY=-9.05 CenterZ=0 NormalX=0 NormalY=0 NormalZ=1 AngleXU=0 Radius=3 StartAngle=1.5708 EndAngle=3.14159
    g31: ArcOfCircle CenterX=63.88 CenterY=-21.45 CenterZ=0 NormalX=0 NormalY=0 NormalZ=1 AngleXU=0 Radius=3 StartAngle=3.14159 EndAngle=4.71239
    g32: ArcOfCircle CenterX=76.28 CenterY=-21.45 CenterZ=0 NormalX=0 NormalY=0 NormalZ=1 AngleXU=0 Radius=3 StartAngle=4.71239 EndAngle=6.28319
    g33: ArcOfCircle CenterX=76.28 CenterY=-9.05 CenterZ=0 NormalX=0 NormalY=0 NormalZ=1 AngleXU=0 Radius=3 StartAngle=0 EndAngle=1.5708
    g34: GeomPoint [constr] X=60.88 Y=-6.05 Z=0
    g35: GeomPoint [constr] X=79.28 Y=-24.45 Z=0
    g36: LineSegment StartX=88.72 StartY=-9.05 StartZ=0 EndX=88.72 EndY=-21.45 EndZ=0
    g37: LineSegment StartX=91.72 StartY=-24.45 StartZ=0 EndX=104.12 EndY=-24.45 EndZ=0
    g38: LineSegment StartX=107.12 StartY=-21.45 StartZ=0 EndX=107.12 EndY=-9.05 EndZ=0
    g39: LineSegment StartX=104.12 StartY=-6.05 StartZ=0 EndX=91.72 EndY=-6.05 EndZ=0
    g40: ArcOfCircle CenterX=91.72 CenterY=-9.05 CenterZ=0 NormalX=0 NormalY=0 NormalZ=1 AngleXU=0 Radius=3 StartAngle=1.5708 EndAngle=3.14159
    g41: ArcOfCircle CenterX=91.72 CenterY=-21.45 CenterZ=0 NormalX=0 NormalY=0 NormalZ=1 AngleXU=0 Radius=3 StartAngle=3.14159 EndAngle=4.71239
    g42: ArcOfCircle CenterX=104.12 CenterY=-21.45 CenterZ=0 NormalX=0 NormalY=0 NormalZ=1 AngleXU=0 Radius=3 StartAngle=4.71239 EndAngle=6.28319
    g43: ArcOfCircle CenterX=104.12 CenterY=-9.05 CenterZ=0 NormalX=0 NormalY=0 NormalZ=1 AngleXU=0 Radius=3 StartAngle=0 EndAngle=1.5708
    g44: GeomPoint [constr] X=88.72 Y=-6.05 Z=0
    g45: GeomPoint [constr] X=107.12 Y=-24.45 Z=0
    g46: LineSegment StartX=88.52 StartY=-45.08 StartZ=0 EndX=88.52 EndY=-57.48 EndZ=0
    g47: LineSegment StartX=91.52 StartY=-60.48 StartZ=0 EndX=103.92 EndY=-60.48 EndZ=0
    g48: LineSegment StartX=106.92 StartY=-57.48 StartZ=0 EndX=106.92 EndY=-45.08 EndZ=0
    g49: LineSegment StartX=103.92 StartY=-42.08 StartZ=0 EndX=91.52 EndY=-42.08 EndZ=0
    g50: ArcOfCircle CenterX=91.52 CenterY=-45.08 CenterZ=0 NormalX=0 NormalY=0 NormalZ=1 AngleXU=0 Radius=3 StartAngle=1.5708 EndAngle=3.14159
    g51: ArcOfCircle CenterX=91.52 CenterY=-57.48 CenterZ=0 NormalX=0 NormalY=0 NormalZ=1 AngleXU=0 Radius=3 StartAngle=3.14159 EndAngle=4.71239
    g52: ArcOfCircle CenterX=103.92 CenterY=-57.48 CenterZ=0 NormalX=0 NormalY=0 NormalZ=1 AngleXU=0 Radius=3 StartAngle=4.71239 EndAngle=6.28319
    g53: ArcOfCircle CenterX=103.92 CenterY=-45.08 CenterZ=0 NormalX=0 NormalY=0 NormalZ=1 AngleXU=0 Radius=3 StartAngle=0 EndAngle=1.5708
    g54: GeomPoint [constr] X=88.52 Y=-42.08 Z=0
    g55: GeomPoint [constr] X=106.92 Y=-60.48 Z=0
    g56: LineSegment StartX=60.68 StartY=-45.08 StartZ=0 EndX=60.68 EndY=-57.48 EndZ=0
    g57: LineSegment StartX=63.68 StartY=-60.48 StartZ=0 EndX=76.08 EndY=-60.48 EndZ=0
    g58: LineSegment StartX=79.08 StartY=-57.48 StartZ=0 EndX=79.08 EndY=-45.08 EndZ=0
    g59: LineSegment StartX=76.08 StartY=-42.08 StartZ=0 EndX=63.68 EndY=-42.08 EndZ=0
    g60: ArcOfCircle CenterX=63.68 CenterY=-45.08 CenterZ=0 NormalX=0 NormalY=0 NormalZ=1 AngleXU=0 Radius=3 StartAngle=1.5708 EndAngle=3.14159
    g61: ArcOfCircle CenterX=63.68 CenterY=-57.48 CenterZ=0 NormalX=0 NormalY=0 NormalZ=1 AngleXU=0 Radius=3 StartAngle=3.14159 EndAngle=4.71239
    g62: ArcOfCircle CenterX=76.08 CenterY=-57.48 CenterZ=0 NormalX=0 NormalY=0 NormalZ=1 AngleXU=0 Radius=3 StartAngle=4.71239 EndAngle=6.28319
    g63: ArcOfCircle CenterX=76.08 CenterY=-45.08 CenterZ=0 NormalX=0 NormalY=0 NormalZ=1 AngleXU=0 Radius=3 StartAngle=0 EndAngle=1.5708
    g64: GeomPoint [constr] X=60.68 Y=-42.08 Z=0
    g65: GeomPoint [constr] X=79.08 Y=-60.48 Z=0
    g66: LineSegment StartX=32.84 StartY=-45.08 StartZ=0 EndX=32.84 EndY=-57.48 EndZ=0
    g67: LineSegment StartX=35.84 StartY=-60.48 StartZ=0 EndX=48.24 EndY=-60.48 EndZ=0
    g68: LineSegment StartX=51.24 StartY=-57.48 StartZ=0 EndX=51.24 EndY=-45.08 EndZ=0
    g69: LineSegment StartX=48.24 StartY=-42.08 StartZ=0 EndX=35.84 EndY=-42.08 EndZ=0
    g70: ArcOfCircle CenterX=35.84 CenterY=-45.08 CenterZ=0 NormalX=0 NormalY=0 NormalZ=1 AngleXU=0 Radius=3 StartAngle=1.5708 EndAngle=3.14159
    g71: ArcOfCircle CenterX=35.84 CenterY=-57.48 CenterZ=0 NormalX=0 NormalY=0 NormalZ=1 AngleXU=0 Radius=3 StartAngle=3.14159 EndAngle=4.71239
    g72: ArcOfCircle CenterX=48.24 CenterY=-57.48 CenterZ=0 NormalX=0 NormalY=0 NormalZ=1 AngleXU=0 Radius=3 StartAngle=4.71239 EndAngle=6.28319
    g73: ArcOfCircle CenterX=48.24 CenterY=-45.08 CenterZ=0 NormalX=0 NormalY=0 NormalZ=1 AngleXU=0 Radius=3 StartAngle=0 EndAngle=1.5708
    g74: GeomPoint [constr] X=32.84 Y=-42.08 Z=0
    g75: GeomPoint [constr] X=51.24 Y=-60.48 Z=0
    g76: LineSegment StartX=5 StartY=-45.08 StartZ=0 EndX=5 EndY=-57.48 EndZ=0
    g77: LineSegment StartX=8 StartY=-60.48 StartZ=0 EndX=20.4 EndY=-60.48 EndZ=0
    g78: LineSegment StartX=23.4 StartY=-57.48 StartZ=0 EndX=23.4 EndY=-45.08 EndZ=0
    g79: LineSegment StartX=20.4 StartY=-42.08 StartZ=0 EndX=8 EndY=-42.08 EndZ=0
    g80: ArcOfCircle CenterX=8 CenterY=-45.08 CenterZ=0 NormalX=0 NormalY=0 NormalZ=1 AngleXU=0 Radius=3 StartAngle=1.5708 EndAngle=3.14159
    g81: ArcOfCircle CenterX=8 CenterY=-57.48 CenterZ=0 NormalX=0 NormalY=0 NormalZ=1 AngleXU=0 Radius=3 StartAngle=3.14159 EndAngle=4.71239
    g82: ArcOfCircle CenterX=20.4 CenterY=-57.48 CenterZ=0 NormalX=0 NormalY=0 NormalZ=1 AngleXU=0 Radius=3 StartAngle=4.71239 EndAngle=6.28319
    g83: ArcOfCircle CenterX=20.4 CenterY=-45.08 CenterZ=0 NormalX=0 NormalY=0 NormalZ=1 AngleXU=0 Radius=3 StartAngle=7e-16 EndAngle=1.5708
    g84: GeomPoint [constr] X=5 Y=-42.08 Z=0
    g85: GeomPoint [constr] X=23.4 Y=-60.48 Z=0
    g86: GeomPoint X=42.24 Y=-15.25 Z=0
    g87: GeomPoint X=70.08 Y=-15.25 Z=0
    g88: GeomPoint X=97.92 Y=-15.25 Z=0
    g89: GeomPoint X=14.2 Y=-51.28 Z=0
    g90: GeomPoint X=42.04 Y=-51.28 Z=0
    g91: GeomPoint X=69.88 Y=-51.28 Z=0
    g92: GeomPoint X=97.72 Y=-51.28 Z=0
  constraints (203):
    c: Coincident(g0,g1)
    c: Coincident(g1,g2)
    c: Coincident(g2,g3)
    c: Coincident(g3,g0)
    c: Vertical(g0)
    c: Vertical(g2)
    c: Horizontal(g1)
    c: Horizontal(g3)
    c: Coincident(g0,g-11)
    c: Coincident(g1,g-12)
    c: Tangent(g4,g8) = -1.5708
    c: Tangent(g4,g9) = -1.5708
    c: Tangent(g5,g9) = -1.5708
    c: Tangent(g5,g10) = -1.5708
    c: Tangent(g6,g10) = -1.5708
    c: Tangent(g6,g11) = -1.5708
    c: Tangent(g7,g11) = -1.5708
    c: Tangent(g7,g8) = -1.5708
    c: Vertical(g4)
    c: Vertical(g6)
    c: Horizontal(g5)
    c: Horizontal(g7)
    c: Equal(g8,g9)
    c: Equal(g9,g10)
    c: Equal(g10,g11)
    c: PointOnObject(g12,g4)
    c: PointOnObject(g12,g7)
    c: PointOnObject(g13,g5)
    c: PointOnObject(g13,g6)
    c: Radius(g11) = 3
    c: DistanceY(g5,g7) = 18.4
    c: DistanceX(g4,g6) = 18.4
    c: Symmetric(g8,g10,g14)
    c: Symmetric(g-4,g-8,g15)
    c: Coincident(g14,g15)
    c: Tangent(g16,g20) = -1.5708
    c: Tangent(g16,g21) = -1.5708
    c: Tangent(g17,g21) = -1.5708
    c: Tangent(g17,g22) = -1.5708
    c: Tangent(g18,g22) = -1.5708
    c: Tangent(g18,g23) = -1.5708
    c: Tangent(g19,g23) = -1.5708
    c: Tangent(g19,g20) = -1.5708
    c: Vertical(g16)
    c: Vertical(g18)
    c: Horizontal(g17)
    c: Horizontal(g19)
    c: Equal(g20,g21)
    c: Equal(g21,g22)
    c: Equal(g22,g23)
    c: PointOnObject(g24,g16)
    c: PointOnObject(g24,g19)
    c: PointOnObject(g25,g17)
    c: PointOnObject(g25,g18)
    c: Tangent(g26,g30) = -1.5708
    c: Tangent(g26,g31) = -1.5708
    c: Tangent(g27,g31) = -1.5708
    c: Tangent(g27,g32) = -1.5708
    c: Tangent(g28,g32) = -1.5708
    c: Tangent(g28,g33) = -1.5708
    c: Tangent(g29,g33) = -1.5708
    c: Tangent(g29,g30) = -1.5708
    c: Vertical(g26)
    c: Vertical(g28)
    c: Horizontal(g27)
    c: Horizontal(g29)
    c: Equal(g30,g31)
    c: Equal(g31,g32)
    c: Equal(g32,g33)
    c: PointOnObject(g34,g26)
    c: PointOnObject(g34,g29)
    c: PointOnObject(g35,g27)
    c: PointOnObject(g35,g28)
    c: Tangent(g36,g40) = -1.5708
    c: Tangent(g36,g41) = -1.5708
    c: Tangent(g37,g41) = -1.5708
    c: Tangent(g37,g42) = -1.5708
    c: Tangent(g38,g42) = -1.5708
    c: Tangent(g38,g43) = -1.5708
    c: Tangent(g39,g43) = -1.5708
    c: Tangent(g39,g40) = -1.5708
    c: Vertical(g36)
    c: Vertical(g38)
    c: Horizontal(g37)
    c: Horizontal(g39)
    c: Equal(g40,g41)
    c: Equal(g41,g42)
    c: Equal(g42,g43)
    c: PointOnObject(g44,g36)
    c: PointOnObject(g44,g39)
    c: PointOnObject(g45,g37)
    c: PointOnObject(g45,g38)
    c: Tangent(g46,g50) = -1.5708
    c: Tangent(g46,g51) = -1.5708
    c: Tangent(g47,g51) = -1.5708
    c: Tangent(g47,g52) = -1.5708
    c: Tangent(g48,g52) = -1.5708
    c: Tangent(g48,g53) = -1.5708
    c: Tangent(g49,g53) = -1.5708
    c: Tangent(g49,g50) = -1.5708
    c: Vertical(g46)
    c: Vertical(g48)
    c: Horizontal(g47)
    c: Horizontal(g49)
    c: Equal(g50,g51)
    c: Equal(g51,g52)
    c: Equal(g52,g53)
    c: PointOnObject(g54,g46)
    c: PointOnObject(g54,g49)
    c: PointOnObject(g55,g47)
    c: PointOnObject(g55,g48)
    c: Tangent(g56,g60) = -1.5708
    c: Tangent(g56,g61) = -1.5708
    c: Tangent(g57,g61) = -1.5708
    c: Tangent(g57,g62) = -1.5708
    c: Tangent(g58,g62) = -1.5708
    c: Tangent(g58,g63) = -1.5708
    c: Tangent(g59,g63) = -1.5708
    c: Tangent(g59,g60) = -1.5708
    c: Vertical(g56)
    c: Vertical(g58)
    c: Horizontal(g57)
    c: Horizontal(g59)
    c: Equal(g60,g61)
    c: Equal(g61,g62)
    c: Equal(g62,g63)
    c: PointOnObject(g64,g56)
    c: PointOnObject(g64,g59)
    c: PointOnObject(g65,g57)
    c: PointOnObject(g65,g58)
    c: Tangent(g66,g70) = -1.5708
    c: Tangent(g66,g71) = -1.5708
    c: Tangent(g67,g71) = -1.5708
    c: Tangent(g67,g72) = -1.5708
    c: Tangent(g68,g72) = -1.5708
    c: Tangent(g68,g73) = -1.5708
    c: Tangent(g69,g73) = -1.5708
    c: Tangent(g69,g70) = -1.5708
    c: Vertical(g66)
    c: Vertical(g68)
    c: Horizontal(g67)
    c: Horizontal(g69)
    c: Equal(g70,g71)
    c: Equal(g71,g72)
    c: Equal(g72,g73)
    c: PointOnObject(g74,g66)
    c: PointOnObject(g74,g69)
    c: PointOnObject(g75,g67)
    c: PointOnObject(g75,g68)
    c: Tangent(g76,g80) = -1.5708
    c: Tangent(g76,g81) = -1.5708
    c: Tangent(g77,g81) = -1.5708
    c: Tangent(g77,g82) = -1.5708
    c: Tangent(g78,g82) = -1.5708
    c: Tangent(g78,g83) = -1.5708
    c: Tangent(g79,g83) = -1.5708
    c: Tangent(g79,g80) = -1.5708
    c: Vertical(g76)
    c: Vertical(g78)
    c: Horizontal(g77)
    c: Horizontal(g79)
    c: Equal(g80,g81)
    c: Equal(g81,g82)
    c: Equal(g82,g83)
    c: PointOnObject(g84,g76)
    c: PointOnObject(g84,g79)
    c: PointOnObject(g85,g77)
    c: PointOnObject(g85,g78)
    c: Equal(g11,g23)
    c: Equal(g23,g33)
    c: Equal(g33,g43)
    c: Equal(g43,g53)
    c: Equal(g53,g63)
    c: Equal(g63,g73)
    c: Equal(g73,g83)
    c: Equal(g7,g19)
    c: Equal(g19,g29)
    c: Equal(g29,g39)
    c: Equal(g39,g49)
    c: Equal(g49,g59)
    c: Equal(g59,g79)
    c: Equal(g76,g66)
    c: Equal(g66,g56)
    c: Equal(g56,g46)
    c: Equal(g46,g36)
    c: Equal(g36,g26)
    c: Equal(g26,g16)
    c: Equal(g16,g4)
    c: Equal(g59,g69)
    c: Symmetric(g-14,g-18,g86)
    c: Symmetric(g20,g22,g86)
    c: Symmetric(g-22,g-26,g87)
    c: Symmetric(g30,g32,g87)
    c: Symmetric(g-29,g-33,g88)
    c: Symmetric(g40,g42,g88)
    c: Symmetric(g-61,g-65,g89)
    c: Symmetric(g-60,g-56,g90)
    c: Symmetric(g-47,g-51,g91)
    c: Symmetric(g-44,g-40,g92)
    c: Symmetric(g50,g52,g92)
    c: Symmetric(g60,g62,g91)
    c: Symmetric(g70,g72,g90)
    c: Symmetric(g80,g82,g89)
FEATURE [PartDesign::Pad] Pad025  label="PadButtonSlideChannel"
  BaseFeature = -> Pad024
  Direction = (0,0,1)
  Length = 1.59
  Length2 = 10
  Profile = -> Sketch034
  ReferenceAxis = -> Sketch034 [N_Axis]
  Refine = true
  SideType = 0
  Suppressed = false
  Type = 0
  Type2 = 0
  expr: Length = <<VarSetButtonDimensions>>.Base_button_slide_depth + <<VarSetButtonDimensions>>.Base_base_thickness
FEATURE [PartDesign::Plane] DatumPlane003  label="DatumPlaneForMirroring"
  AttachmentSupport = -> [Pad025]
  Length = 165.309
  MapMode = 5
  Placement = pos=(0,0,3.09) rot=(0,0,1;0rad)
  ResizeMode = 0
  Width = 120.249
FEATURE [PartDesign::Mirrored] Mirrored004
  BaseFeature = -> Pad025
  MirrorPlane = -> DatumPlane003
  Originals = -> [Pad024,Pad025]
  Refine = true
  Suppressed = false
  TransformMode = 0
FEATURE [Sketcher::SketchObject] Sketch036  label="SketchButtonCapBase"
  ArcFitTolerance = 1e-06
  AttachmentSupport = -> [XY_Plane014]
  ExternalTypes = [0]
  FullyConstrained = true
  MakeInternals = false
  MapMode = 5
  expr: Constraints[19] = <<VarSetButtonDimensions>>.Base_button_radius
  expr: Constraints[20] = <<VarSetButtonDimensions>>.Base_button_height
  expr: Constraints[21] = <<VarSetButtonDimensions>>.Base_button_width
  sketch-geometry (10):
    g0: LineSegment StartX=-5 StartY=-8 StartZ=0 EndX=5 EndY=-8 EndZ=0
    g1: LineSegment StartX=8 StartY=-5 StartZ=0 EndX=8 EndY=5 EndZ=0
    g2: LineSegment StartX=5 StartY=8 StartZ=0 EndX=-5 EndY=8 EndZ=0
    g3: LineSegment StartX=-8 StartY=5 StartZ=0 EndX=-8 EndY=-5 EndZ=0
    g4: ArcOfCircle CenterX=-5 CenterY=-5 CenterZ=0 NormalX=0 NormalY=0 NormalZ=1 AngleXU=0 Radius=3 StartAngle=3.14159 EndAngle=4.71239
    g5: ArcOfCircle CenterX=5 CenterY=-5 CenterZ=0 NormalX=0 NormalY=0 NormalZ=1 AngleXU=0 Radius=3 StartAngle=4.71239 EndAngle=6.28319
    g6: ArcOfCircle CenterX=5 CenterY=5 CenterZ=0 NormalX=0 NormalY=0 NormalZ=1 AngleXU=0 Radius=3 StartAngle=1e-16 EndAngle=1.5708
    g7: ArcOfCircle CenterX=-5 CenterY=5 CenterZ=0 NormalX=0 NormalY=0 NormalZ=1 AngleXU=0 Radius=3 StartAngle=1.5708 EndAngle=3.14159
    g8: GeomPoint [constr] X=8 Y=8 Z=0
    g9: GeomPoint [constr] X=0 Y=0 Z=0
  constraints (22):
    c: Tangent(g0,g4) = -1.5708
    c: Tangent(g0,g5) = -1.5708
    c: Tangent(g1,g5) = -1.5708
    c: Tangent(g1,g6) = -1.5708
    c: Tangent(g2,g6) = -1.5708
    c: Tangent(g2,g7) = -1.5708
    c: Tangent(g3,g7) = -1.5708
    c: Tangent(g3,g4) = -1.5708
    c: Horizontal(g0)
    c: Horizontal(g2)
    c: Vertical(g1)
    c: Vertical(g3)
    c: Equal(g4,g5)
    c: Equal(g5,g6)
    c: Equal(g6,g7)
    c: Symmetric(g2,g0,g9)
    c: PointOnObject(g8,g1)
    c: PointOnObject(g8,g2)
    c: Coincident(g9,g-1)
    c: Radius(g5) = 3
    c: DistanceY(g0,g2) = 16
    c: DistanceX(g3,g1) = 16
FEATURE [PartDesign::Plane] DatumPlane004
  AttachmentSupport = -> [Sketch036]
  Length = 60
  MapMode = 7
  Placement = pos=(8,-5,0) rot=(1,0,0;1.5708rad)
  ResizeMode = 0
  Width = 60
FEATURE [PartDesign::Pad] Pad026  label="PadButtonCapPlusBase"
  Direction = (0,0,1)
  Length = 4.59
  Length2 = 10
  Profile = -> Sketch036
  ReferenceAxis = -> Sketch036 [N_Axis]
  Refine = true
  SideType = 0
  Suppressed = false
  Type = 0
  Type2 = 0
  expr: Length = <<VarSetButtonDimensions>>.button_cap_height + <<VarSetButtonDimensions>>.Base_button_slide_depth + <<VarSetButtonDimensions>>.Base_base_thickness
FEATURE [PartDesign::Thickness] Thickness001  label="ThicknessCapWall"
  Base = -> Pad026 [Face9]
  BaseFeature = -> Pad026
  Intersection = false
  Join = 0
  Mode = 0
  Refine = true
  Reversed = true
  SupportTransform = false
  Suppressed = false
  Value = 1.5
  expr: Value = <<VarSetButtonDimensions>>.button_cap_wall_thickness
FEATURE [App::Link] C6_C_1206_3216Metric_fe8f5ab1829c_ln_005  label="C5_C_1206_3216Metric_921661c36669"
  LinkPlacement = pos=(23.5634,32.484,0) rot=(0,0,1;3.14159rad)
  LinkedObject = -> Shape007
  Placement = pos=(23.5634,32.484,0) rot=(0,0,1;3.14159rad)
FEATURE [App::Link] C6_C_1206_3216Metric_fe8f5ab1829c_ln_006  label="C4_C_1206_3216Metric_1d953bd43f096"
  LinkPlacement = pos=(18.375,36.646,0) rot=(0,0,1;0rad)
  LinkedObject = -> Shape007
  Placement = pos=(18.375,36.646,0) rot=(0,0,1;0rad)
FEATURE [App::Link] C6_C_1206_3216Metric_fe8f5ab1829c_ln_007  label="C3_C_1206_3216Metric_0d3c0877bab005"
  LinkPlacement = pos=(18.375,29.28,0) rot=(0,0,1;0rad)
  LinkedObject = -> Shape007
  Placement = pos=(18.375,29.28,0) rot=(0,0,1;0rad)
FEATURE [App::Link] C6_C_1206_3216Metric_fe8f5ab1829c_ln_008  label="C1_C_1206_3216Metric_20d4e43c8e050"
  LinkPlacement = pos=(85.52,41.17,0) rot=(0,0,1;3.14159rad)
  LinkedObject = -> Shape007
  Placement = pos=(85.52,41.17,0) rot=(0,0,1;3.14159rad)
FEATURE [App::Link] C6_C_1206_3216Metric_fe8f5ab1829c_ln_009  label="C2_C_1206_3216Metric_1073df5edb1d001"
  LinkPlacement = pos=(85.52,43.71,0) rot=(0,0,1;3.14159rad)
  LinkedObject = -> Shape007
  Placement = pos=(85.52,43.71,0) rot=(0,0,1;3.14159rad)
FEATURE [App::Link] D1_LED_1206_3216Metric_5818a68925bf_ln_008  label="D7_LED_1206_3216Metric_e0f900cdbb9d001"
  LinkPlacement = pos=(42.1175,5.8,-1.6) rot=(0,1,0;3.14159rad)
  LinkedObject = -> Shape012
  Placement = pos=(42.1175,5.8,-1.6) rot=(0,1,0;3.14159rad)
FEATURE [App::Link] D1_LED_1206_3216Metric_5818a68925bf_ln_009  label="D8_LED_1206_3216Metric_4590835c06e003"
  LinkPlacement = pos=(69.9575,5.8,-1.6) rot=(0,1,0;3.14159rad)
  LinkedObject = -> Shape012
  Placement = pos=(69.9575,5.8,-1.6) rot=(0,1,0;3.14159rad)
FEATURE [App::Link] D1_LED_1206_3216Metric_5818a68925bf_ln_010  label="D9_LED_1206_3216Metric_f97e9ca9ca0c001"
  LinkPlacement = pos=(97.7975,5.8,-1.6) rot=(1,0,0;3.14159rad)
  LinkedObject = -> Shape012
  Placement = pos=(97.7975,5.8,-1.6) rot=(1,0,0;3.14159rad)
FEATURE [App::Link] D1_LED_1206_3216Metric_5818a68925bf_ln_011  label="D4_LED_1206_3216Metric_98b5ea636a079"
  LinkPlacement = pos=(42.1625,61.26,-1.6) rot=(1,0,0;3.14159rad)
  LinkedObject = -> Shape012
  Placement = pos=(42.1625,61.26,-1.6) rot=(1,0,0;3.14159rad)
FEATURE [App::Link] D1_LED_1206_3216Metric_5818a68925bf_ln_012  label="D2_LED_1206_3216Metric_2fa2df955064"
  LinkPlacement = pos=(97.7975,61.26,-1.6) rot=(0,1,0;3.14159rad)
  LinkedObject = -> Shape012
  Placement = pos=(97.7975,61.26,-1.6) rot=(0,1,0;3.14159rad)
FEATURE [App::Link] D1_LED_1206_3216Metric_5818a68925bf_ln_013  label="D6_LED_1206_3216Metric_e89784457431"
  LinkPlacement = pos=(14.3225,5.8,-1.6) rot=(0,1,0;3.14159rad)
  LinkedObject = -> Shape012
  Placement = pos=(14.3225,5.8,-1.6) rot=(0,1,0;3.14159rad)
FEATURE [App::Link] D1_LED_1206_3216Metric_5818a68925bf_ln_014  label="D5_LED_1206_3216Metric_64f8a7d577f007"
  LinkPlacement = pos=(14.3225,61.26,-1.6) rot=(1,0,0;3.14159rad)
  LinkedObject = -> Shape012
  Placement = pos=(14.3225,61.26,-1.6) rot=(1,0,0;3.14159rad)
FEATURE [App::Link] D1_LED_1206_3216Metric_5818a68925bf_ln_015  label="D3_LED_1206_3216Metric_db0b37632ff004"
  LinkPlacement = pos=(70.0025,61.26,-1.6) rot=(1,0,0;3.14159rad)
  LinkedObject = -> Shape012
  Placement = pos=(70.0025,61.26,-1.6) rot=(1,0,0;3.14159rad)
FEATURE [PartDesign::CoordinateSystem] Local_CS_cc028
  AttacherType = Attacher::AttachEngine3D
  MapMode = 2
FEATURE [Sketcher::SketchObject] PCB_Sketch_cc028
  ArcFitTolerance = 1e-06
  ExternalTypes = [0]
  FullyConstrained = false
  MakeInternals = false
  sketch-geometry (8):
    g0: LineSegment StartX=0.45 StartY=65.81 StartZ=0 EndX=113.87 EndY=65.81 EndZ=0
    g1: LineSegment StartX=113.87 StartY=65.81 StartZ=0 EndX=113.87 EndY=0.04 EndZ=0
    g2: LineSegment StartX=113.87 StartY=0.04 StartZ=0 EndX=0.45 EndY=0.04 EndZ=0
    g3: LineSegment StartX=0.45 StartY=0.04 StartZ=0 EndX=0.45 EndY=65.81 EndZ=0
    g4: Circle CenterX=4.51408 CenterY=61.5799 CenterZ=0 NormalX=0 NormalY=0 NormalZ=1 AngleXU=0 Radius=1.25
    g5: Circle CenterX=107.514 CenterY=61.5799 CenterZ=0 NormalX=0 NormalY=0 NormalZ=1 AngleXU=0 Radius=1.25
    g6: Circle CenterX=107.514 CenterY=5.02733 CenterZ=0 NormalX=0 NormalY=0 NormalZ=1 AngleXU=0 Radius=1.25
    g7: Circle CenterX=4.51408 CenterY=5.02733 CenterZ=0 NormalX=0 NormalY=0 NormalZ=1 AngleXU=0 Radius=1.25
  constraints (4):
    c: Coincident(g2,g3)
    c: Coincident(g0,g3)
    c: Coincident(g1,g2)
    c: Coincident(g0,g1)
FEATURE [Part::Feature] Part__Feature008  label="AP63203WU-015"
  shape: bbox 0.65 x 0.63 x 0.375 mm, 14 faces (baked)
FEATURE [Part::Feature] Part__Feature009  label="AP63203WU-016"
  shape: bbox 0.65 x 0.63 x 0.375 mm, 14 faces (baked)
FEATURE [Part::Feature] Part__Feature010  label="AP63203WU-017"
  shape: bbox 0.65 x 0.63 x 0.375 mm, 14 faces (baked)
FEATURE [Part::Feature] Part__Feature011  label="AP63203WU-018"
  shape: bbox 0.65 x 0.63 x 0.375 mm, 14 faces (baked)
FEATURE [Part::Feature] Part__Feature012  label="AP63203WU-019"
  shape: bbox 0.65 x 0.63 x 0.375 mm, 14 faces (baked)
FEATURE [Part::Feature] Part__Feature013  label="AP63203WU-020"
  shape: bbox 0.65 x 0.63 x 0.375 mm, 14 faces (baked)
FEATURE [Part::Feature] Part__Feature014  label="AP63203WU-021"
  shape: bbox 1.601 x 0.9 x 2.901 mm, 45 faces (baked)
FEATURE [Part::Feature] Part__Feature015  label="AP63203WU-022"
  shape: bbox 0.2 x 0.05 x 0.2 mm, 4 faces (baked)
FEATURE [App::Part] AP63203WU_008  label="IC1_AP63203WU-015_b8c35da43585"
  Group = -> [Part__Feature008,Part__Feature009,Part__Feature010,Part__Feature011,Part__Feature012,Part__Feature013,Part__Feature014,Part__Feature015]
  Origin = -> Origin020
  Placement = pos=(18.126,32.96,0) rot=(1,0,0;1.5708rad)
FEATURE [Part::Feature] Pcb_cc028
  Placement = pos=(-24.2366,113.11,0) rot=(0,0,1;0rad)
  shape: bbox 113.4 x 65.77 x 1.6 mm, 60 faces (baked)
FEATURE [App::Part] Board_Geoms_cc028  label="Board_Geoms_cc029"
  Group = -> [Pcb_cc028,PCB_Sketch_cc028]
  Origin = -> Origin015
FEATURE [App::Link] R4_R_1206_3216Metric_a98f0a8b4acf_ln_011  label="R1_R_1206_3216Metric_0d48a55c24de001"
  LinkPlacement = pos=(92.55,43.89,0) rot=(0,0,1;1.5708rad)
  LinkedObject = -> Shape010
  Placement = pos=(92.55,43.89,0) rot=(0,0,1;1.5708rad)
FEATURE [App::Link] R4_R_1206_3216Metric_a98f0a8b4acf_ln_012  label="R2_R_1206_3216Metric_7877a5f10d038"
  LinkPlacement = pos=(31.62,30.71,0) rot=(0,0,1;1.5708rad)
  LinkedObject = -> Shape010
  Placement = pos=(31.62,30.71,0) rot=(0,0,1;1.5708rad)
FEATURE [App::Link] R4_R_1206_3216Metric_a98f0a8b4acf_ln_013  label="R12_R_1206_3216Metric_9a77f9e92563"
  LinkPlacement = pos=(107.28,49.04,0) rot=(0,0,1;0rad)
  LinkedObject = -> Shape010
  Placement = pos=(107.28,49.04,0) rot=(0,0,1;0rad)
FEATURE [App::Link] R4_R_1206_3216Metric_a98f0a8b4acf_ln_014  label="R10_R_1206_3216Metric_955bf38eb66b001"
  LinkPlacement = pos=(63.83,5.8,-1.6) rot=(1,0,0;3.14159rad)
  LinkedObject = -> Shape010
  Placement = pos=(63.83,5.8,-1.6) rot=(1,0,0;3.14159rad)
FEATURE [App::Link] R4_R_1206_3216Metric_a98f0a8b4acf_ln_015  label="R8_R_1206_3216Metric_c4d4031c6125"
  LinkPlacement = pos=(9.39,7.35,-1.6) rot=(0.707107,-0.707107,0;3.14159rad)
  LinkedObject = -> Shape010
  Placement = pos=(9.39,7.35,-1.6) rot=(0.707107,-0.707107,0;3.14159rad)
FEATURE [App::Link] R4_R_1206_3216Metric_a98f0a8b4acf_ln_016  label="R3_R_1206_3216Metric_c80006f71294"
  LinkPlacement = pos=(92.2,61.31,-1.6) rot=(1,0,0;3.14159rad)
  LinkedObject = -> Shape010
  Placement = pos=(92.2,61.31,-1.6) rot=(1,0,0;3.14159rad)
FEATURE [App::Link] R4_R_1206_3216Metric_a98f0a8b4acf_ln_017  label="R7_R_1206_3216Metric_6f705efabba001"
  LinkPlacement = pos=(20.25,61.26,-1.6) rot=(0,1,0;3.14159rad)
  LinkedObject = -> Shape010
  Placement = pos=(20.25,61.26,-1.6) rot=(0,1,0;3.14159rad)
FEATURE [App::Link] R4_R_1206_3216Metric_a98f0a8b4acf_ln_018  label="R6_R_1206_3216Metric_4dd85524e60b001"
  LinkPlacement = pos=(48.42,61.26,-1.6) rot=(0,1,0;3.14159rad)
  LinkedObject = -> Shape010
  Placement = pos=(48.42,61.26,-1.6) rot=(0,1,0;3.14159rad)
FEATURE [App::Link] R4_R_1206_3216Metric_a98f0a8b4acf_ln_019  label="R5_R_1206_3216Metric_5aff5c873fbb001"
  LinkPlacement = pos=(75.86,61.27,-1.6) rot=(0,1,0;3.14159rad)
  LinkedObject = -> Shape010
  Placement = pos=(75.86,61.27,-1.6) rot=(0,1,0;3.14159rad)
FEATURE [App::Link] R4_R_1206_3216Metric_a98f0a8b4acf_ln_020  label="R11_R_1206_3216Metric_e90fbb06c50b001"
  LinkPlacement = pos=(104,8.6,-1.6) rot=(0.707107,-0.707107,0;3.14159rad)
  LinkedObject = -> Shape010
  Placement = pos=(104,8.6,-1.6) rot=(0.707107,-0.707107,0;3.14159rad)
FEATURE [App::Link] R4_R_1206_3216Metric_a98f0a8b4acf_ln_021  label="R9_R_1206_3216Metric_fd9422578c087"
  LinkPlacement = pos=(35.88,5.8,-1.6) rot=(1,0,0;3.14159rad)
  LinkedObject = -> Shape010
  Placement = pos=(35.88,5.8,-1.6) rot=(1,0,0;3.14159rad)
FEATURE [App::Link] SW8_SW_PUSH_6mm_76d8f6a7f289_ln_007  label="SW5_SW_PUSH_6mm_bc2679ab0c029"
  LinkPlacement = pos=(17.55,17.5,-1.6) rot=(0,1,0;3.14159rad)
  LinkedObject = -> Shape013
  Placement = pos=(17.55,17.5,-1.6) rot=(0,1,0;3.14159rad)
FEATURE [App::Link] SW8_SW_PUSH_6mm_76d8f6a7f289_ln_008  label="SW7_SW_PUSH_6mm_98a993c83936"
  LinkPlacement = pos=(73.23,17.5,-1.6) rot=(0,1,0;3.14159rad)
  LinkedObject = -> Shape013
  Placement = pos=(73.23,17.5,-1.6) rot=(0,1,0;3.14159rad)
FEATURE [App::Link] SW8_SW_PUSH_6mm_76d8f6a7f289_ln_009  label="SW6_SW_PUSH_6mm_e97d2eab9daa001"
  LinkPlacement = pos=(45.39,17.5,-1.6) rot=(0,1,0;3.14159rad)
  LinkedObject = -> Shape013
  Placement = pos=(45.39,17.5,-1.6) rot=(0,1,0;3.14159rad)
FEATURE [App::Link] SW8_SW_PUSH_6mm_76d8f6a7f289_ln_010  label="SW2_SW_PUSH_6mm_e1b948049a004"
  LinkPlacement = pos=(66.73,49.03,-1.6) rot=(1,0,0;3.14159rad)
  LinkedObject = -> Shape013
  Placement = pos=(66.73,49.03,-1.6) rot=(1,0,0;3.14159rad)
FEATURE [App::Link] SW8_SW_PUSH_6mm_76d8f6a7f289_ln_011  label="SW1_SW_PUSH_6mm_846872bf3f2a001"
  LinkPlacement = pos=(94.57,49.03,-1.6) rot=(1,0,0;3.14159rad)
  LinkedObject = -> Shape013
  Placement = pos=(94.57,49.03,-1.6) rot=(1,0,0;3.14159rad)
FEATURE [App::Link] SW8_SW_PUSH_6mm_76d8f6a7f289_ln_012  label="SW3_SW_PUSH_6mm_786fe8b935ec001"
  LinkPlacement = pos=(38.89,49.03,-1.6) rot=(1,0,0;3.14159rad)
  LinkedObject = -> Shape013
  Placement = pos=(38.89,49.03,-1.6) rot=(1,0,0;3.14159rad)
FEATURE [App::Link] SW8_SW_PUSH_6mm_76d8f6a7f289_ln_013  label="SW4_SW_PUSH_6mm_2c4766872f098"
  LinkPlacement = pos=(11.05,49.03,-1.6) rot=(1,0,0;3.14159rad)
  LinkedObject = -> Shape013
  Placement = pos=(11.05,49.03,-1.6) rot=(1,0,0;3.14159rad)
FEATURE [Part::Feature] Shape007  label="C6_C_1206_3216Metric_fe8f5ab1829c001"
  Placement = pos=(23.5634,30.042,0) rot=(0,0,1;3.14159rad)
  shape: bbox 3.2 x 1.6 x 1.6 mm, 28 faces (baked)
FEATURE [Part::Feature] Shape008  label="U1_ESP32-WROOM-32U_0b53285c672d001"
  Placement = pos=(69.99,33.305,0) rot=(0,0,-1;1.5708rad)
  shape: bbox 19.2 x 18 x 3.2 mm, 766 faces (baked)
FEATURE [Part::Feature] Shape009  label="U2_SOIC_8_39x49mm_P127mm_6befcaffebcc001"
  Placement = pos=(43.625,35.8786,0) rot=(0,0,1;3.14159rad)
  shape: bbox 6 x 4.9 x 1.75 mm, 156 faces (baked)
FEATURE [Part::Feature] Shape010  label="R4_R_1206_3216Metric_a98f0a8b4acf001"
  Placement = pos=(42.97,30.25,0) rot=(0,0,1;3.14159rad)
  shape: bbox 3.2 x 1.6 x 0.55 mm, 26 faces (baked)
FEATURE [Part::Feature] Shape011  label="J1_PinHeader_1x06_P254mm_Horizontal_6c59025dd185"
  Placement = pos=(102.61,39.06,0) rot=(0,0,1;0rad)
  shape: bbox 10.36 x 15.24 x 5.54 mm, 166 faces (baked)
FEATURE [Part::Feature] Shape012  label="D1_LED_1206_3216Metric_5818a68925bf001"
  Placement = pos=(31.6022,35.7369,0) rot=(0,0,-1;1.5708rad)
  shape: bbox 1.6 x 3.2 x 1.1 mm, 50 faces (baked)
FEATURE [Part::Feature] Shape013  label="SW8_SW_PUSH_6mm_76d8f6a7f290"
  Placement = pos=(101.07,17.5,-1.6) rot=(0,1,0;3.14159rad)
  shape: bbox 7.174 x 6 x 7.8 mm, 105 faces (baked)
FEATURE [App::Part] Bot_cc028  label="Bot_cc029"
  Group = -> [R4_R_1206_3216Metric_a98f0a8b4acf_ln_014,D1_LED_1206_3216Metric_5818a68925bf_ln_008,D1_LED_1206_3216Metric_5818a68925bf_ln_009,R4_R_1206_3216Metric_a98f0a8b4acf_ln_015,Shape013,R4_R_1206_3216Metric_a98f0a8b4acf_ln_016,R4_R_1206_3216Metric_a98f0a8b4acf_ln_017,SW8_SW_PUSH_6mm_76d8f6a7f289_ln_007,D1_LED_1206_3216Metric_5818a68925bf_ln_010,R4_R_1206_3216Metric_a98f0a8b4acf_ln_018,+14 more]
  Origin = -> Origin019
FEATURE [App::Part] Top_cc028  label="Top_cc029"
  Group = -> [Shape007,Shape008,Shape009,C6_C_1206_3216Metric_fe8f5ab1829c_ln_005,C6_C_1206_3216Metric_fe8f5ab1829c_ln_006,C6_C_1206_3216Metric_fe8f5ab1829c_ln_007,Shape010,AP63203WU_008,R4_R_1206_3216Metric_a98f0a8b4acf_ln_011,C6_C_1206_3216Metric_fe8f5ab1829c_ln_008,R4_R_1206_3216Metric_a98f0a8b4acf_ln_012,Shape011,C6_C_1206_3216Metric_fe8f5ab1829c_ln_009,Shape012,R4_R_1206_3216Metric_a98f0a8b4acf_ln_013]
  Origin = -> Origin018
FEATURE [App::Part] Step_Models_cc028  label="Step_Models_cc029"
  Group = -> [Top_cc028,Bot_cc028]
  Origin = -> Origin017
FEATURE [App::Part] Board_cc028  label="trailer-switch-panel-eight-buttons-v2"
  Group = -> [Local_CS_cc028,Board_Geoms_cc028,Step_Models_cc028]
  Origin = -> Origin016
  Placement = pos=(0,-4e-16,-2.95) rot=(1,0,0;3.14159rad)
FEATURE [PartDesign::SubShapeBinder] Binder007  label="BinderPcbV2"
  BindCopyOnChange = 0
  BindMode = 0
  ClaimChildren = false
  Context = -> Body003 [Binder007.]
  Fuse = false
  MakeFace = true
  OffsetFill = false
  OffsetIntersection = false
  OffsetJoinType = 0
  OffsetOpenResult = false
  PartialLoad = false
  Placement = pos=(0.66,0,0) rot=(0,0,1;0rad)
  Refine = true
  Relative = true
  Support = -> [Board_cc028]
  _Version = 2
FEATURE [Sketcher::SketchObject] Sketch040  label="SketchPcbStandOffs001"
  ArcFitTolerance = 1e-06
  AttachmentSupport = -> [Mirrored004]
  ExternalGeometry = -> [Mirrored004,Binder007]
  ExternalTypes = [0]
  FullyConstrained = true
  MakeInternals = false
  MapMode = 5
  Placement = pos=(0,0,0) rot=(1,0,0;3.14159rad)
  sketch-geometry (8):
    g0: Circle CenterX=5.17408 CenterY=61.5799 CenterZ=0 NormalX=0 NormalY=0 NormalZ=1 AngleXU=0 Radius=1
    g1: Circle CenterX=5.17408 CenterY=5.02733 CenterZ=0 NormalX=0 NormalY=0 NormalZ=1 AngleXU=0 Radius=1
    g2: Circle CenterX=108.174 CenterY=5.02733 CenterZ=0 NormalX=0 NormalY=0 NormalZ=1 AngleXU=0 Radius=1
    g3: Circle CenterX=108.174 CenterY=61.5799 CenterZ=0 NormalX=0 NormalY=0 NormalZ=1 AngleXU=0 Radius=1
    g4: Circle CenterX=5.17408 CenterY=61.5799 CenterZ=0 NormalX=0 NormalY=0 NormalZ=1 AngleXU=0 Radius=2.5
    g5: Circle CenterX=5.17408 CenterY=5.02733 CenterZ=0 NormalX=0 NormalY=0 NormalZ=1 AngleXU=0 Radius=2.5
    g6: Circle CenterX=108.174 CenterY=5.02733 CenterZ=0 NormalX=0 NormalY=0 NormalZ=1 AngleXU=0 Radius=2.5
    g7: Circle CenterX=108.174 CenterY=61.5799 CenterZ=0 NormalX=0 NormalY=0 NormalZ=1 AngleXU=0 Radius=2.5
  constraints (17):
    c: Diameter(g0) = 2
    c: Equal(g0,g1)
    c: Equal(g1,g2)
    c: Equal(g2,g3)
    c: Coincident(g4,g0)
    c: Diameter(g4) = 5
    c: Coincident(g5,g1)
    c: Coincident(g6,g2)
    c: Coincident(g7,g3)
    c: Equal(g4,g7)
    c: Equal(g7,g6)
    c: Equal(g6,g5)
    c: Coincident(g3,g-5)
    c: Coincident(g-6,g2)
    c: Coincident(g1,g-7)
    c: Coincident(g0,g-8)
    c: DistanceX(g1,g2) = 103
FEATURE [PartDesign::Pad] Pad029  label="PadStandoffs"
  BaseFeature = -> Mirrored004
  Direction = (0,0,-1)
  Length = 3.2
  Length2 = 10
  Profile = -> Sketch040
  ReferenceAxis = -> Sketch040 [N_Axis]
  Refine = true
  SideType = 0
  Suppressed = false
  Type = 0
  Type2 = 0
FEATURE [PartDesign::Pocket] Pocket007  label="PocketHeatInsertHole"
  BaseFeature = -> Pad029
  Direction = (0,0,1)
  Length = 6.5
  Length2 = 5
  Profile = -> Pad029 [Face230,Face228,Face227,Face229]
  Refine = true
  SideType = 0
  Suppressed = false
  Type = 0
  Type2 = 0
FEATURE [Sketcher::SketchObject] Sketch041  label="SketchSidewalls"
  ArcFitTolerance = 1e-06
  AttachmentSupport = -> [Pocket007]
  ExternalGeometry = -> [Pocket007]
  ExternalTypes = [0]
  FullyConstrained = true
  MakeInternals = false
  MapMode = 5
  Placement = pos=(0,0,0) rot=(1,0,0;3.14159rad)
  sketch-geometry (8):
    g0: LineSegment StartX=-3 StartY=71.81 StartZ=0 EndX=-3 EndY=-6 EndZ=0
    g1: LineSegment StartX=-3 StartY=-6 StartZ=0 EndX=116.87 EndY=-6 EndZ=0
    g2: LineSegment StartX=116.87 StartY=-6 StartZ=0 EndX=116.87 EndY=71.81 EndZ=0
    g3: LineSegment StartX=116.87 StartY=71.81 StartZ=0 EndX=-3 EndY=71.81 EndZ=0
    g4: LineSegment StartX=-1 StartY=69.81 StartZ=0 EndX=-1 EndY=-4 EndZ=0
    g5: LineSegment StartX=-1 StartY=-4 StartZ=0 EndX=114.87 EndY=-4 EndZ=0
    g6: LineSegment StartX=114.87 StartY=-4 StartZ=0 EndX=114.87 EndY=69.81 EndZ=0
    g7: LineSegment StartX=114.87 StartY=69.81 StartZ=0 EndX=-1 EndY=69.81 EndZ=0
  constraints (22):
    c: Coincident(g0,g1)
    c: Coincident(g1,g2)
    c: Coincident(g2,g3)
    c: Coincident(g3,g0)
    c: Vertical(g0)
    c: Vertical(g2)
    c: Horizontal(g1)
    c: Horizontal(g3)
    c: Coincident(g0,g-3)
    c: Coincident(g1,g-4)
    c: Coincident(g4,g5)
    c: Coincident(g5,g6)
    c: Coincident(g6,g7)
    c: Coincident(g7,g4)
    c: Vertical(g4)
    c: Vertical(g6)
    c: Horizontal(g5)
    c: Horizontal(g7)
    c: DistanceX(g5,g1) = 2
    c: DistanceY(g1,g5) = 2
    c: DistanceY(g4,g0) = 2
    c: DistanceX(g0,g4) = 2
FEATURE [PartDesign::Pad] Pad030  label="PadSidewalls"
  BaseFeature = -> Pocket007
  Direction = (0,0,-1)
  Length = 8
  Length2 = 10
  Profile = -> Sketch041
  ReferenceAxis = -> Sketch041 [N_Axis]
  Refine = true
  SideType = 0
  Suppressed = false
  Type = 0
  Type2 = 0
FEATURE [Sketcher::SketchObject] Sketch042  label="SketchCaseBackCoverHoles"
  ArcFitTolerance = 1e-06
  AttachmentSupport = -> [Pad030]
  ExternalGeometry = -> [Binder006,Pad030]
  ExternalTypes = [0]
  FullyConstrained = true
  MakeInternals = false
  MapMode = 5
  Placement = pos=(0,0,0) rot=(1,0,0;3.14159rad)
  sketch-geometry (14):
    g0: GeomPoint X=57.16 Y=32.925 Z=0
    g1: GeomPoint [constr] X=57.16 Y=32.925 Z=0
    g2: Circle CenterX=113.57 CenterY=68.81 CenterZ=0 NormalX=0 NormalY=0 NormalZ=1 AngleXU=0 Radius=1
    g3: Circle CenterX=2e-16 CenterY=68.81 CenterZ=0 NormalX=0 NormalY=0 NormalZ=1 AngleXU=0 Radius=1
    g4: Circle CenterX=2e-16 CenterY=-2.7 CenterZ=0 NormalX=0 NormalY=0 NormalZ=1 AngleXU=0 Radius=1
    g5: Circle CenterX=113.57 CenterY=-2.7 CenterZ=0 NormalX=0 NormalY=0 NormalZ=1 AngleXU=0 Radius=1
    g6: Circle CenterX=113.57 CenterY=68.81 CenterZ=0 NormalX=0 NormalY=0 NormalZ=1 AngleXU=0 Radius=2.5
    g7: Circle CenterX=113.57 CenterY=-2.7 CenterZ=0 NormalX=0 NormalY=0 NormalZ=1 AngleXU=0 Radius=2.5
    g8: Circle CenterX=2e-16 CenterY=-2.7 CenterZ=0 NormalX=0 NormalY=0 NormalZ=1 AngleXU=0 Radius=2.5
    g9: Circle CenterX=2e-16 CenterY=68.81 CenterZ=0 NormalX=0 NormalY=0 NormalZ=1 AngleXU=0 Radius=2.5
    g10: LineSegment [constr] StartX=2e-16 StartY=68.81 StartZ=0 EndX=2e-16 EndY=-2.7 EndZ=0
    g11: LineSegment [constr] StartX=2e-16 StartY=-2.7 StartZ=0 EndX=113.57 EndY=-2.7 EndZ=0
    g12: LineSegment [constr] StartX=113.57 StartY=-2.7 StartZ=0 EndX=113.57 EndY=68.81 EndZ=0
    g13: LineSegment [constr] StartX=113.57 StartY=68.81 StartZ=0 EndX=0 EndY=68.81 EndZ=0
  constraints (30):
    c: Symmetric(g-3,g-4,g0)
    c: Coincident(g1,g0)
    c: Diameter(g2) = 2
    c: Equal(g2,g5)
    c: Equal(g5,g4)
    c: Equal(g4,g3)
    c: Diameter(g6) = 5
    c: Equal(g6,g9)
    c: Equal(g9,g8)
    c: Equal(g8,g7)
    c: Coincident(g3,g9)
    c: Coincident(g6,g2)
    c: Coincident(g7,g5)
    c: Coincident(g8,g4)
    c: Coincident(g10,g11)
    c: Coincident(g11,g12)
    c: Coincident(g12,g13)
    c: Coincident(g13,g10)
    c: Vertical(g10)
    c: Vertical(g12)
    c: Horizontal(g11)
    c: Horizontal(g13)
    c: DistanceX(g11,g-7) = 3.3
    c: DistanceY(g-7,g11) = 3.3
    c: DistanceX(g-5,g10) = 3
    c: DistanceY(g10,g-5) = 3
    c: Coincident(g11,g5)
    c: Coincident(g3,g10)
    c: Coincident(g2,g12)
    c: Coincident(g4,g10)
FEATURE [PartDesign::Pad] Pad031  label="PadCaseBackingMountHoles"
  BaseFeature = -> Pad030
  Direction = (0,0,-1)
  Length = 8
  Length2 = 10
  Profile = -> Sketch042
  ReferenceAxis = -> Sketch042 [N_Axis]
  Refine = true
  SideType = 0
  Suppressed = false
  Type = 0
  Type2 = 0
FEATURE [Sketcher::SketchObject] Sketch043
  ArcFitTolerance = 1e-06
  AttachmentSupport = -> [Pad031]
  ExternalGeometry = -> [Pad031]
  ExternalTypes = [0]
  FullyConstrained = true
  MakeInternals = false
  MapMode = 5
  Placement = pos=(0,4,0) rot=(1,0,0;1.5708rad)
  sketch-geometry (12):
    g0: GeomPoint X=56.785 Y=-8 Z=0
    g1: LineSegment StartX=49.285 StartY=-1.3 StartZ=0 EndX=49.285 EndY=-6.5 EndZ=0
    g2: LineSegment StartX=49.285 StartY=-6.5 StartZ=0 EndX=64.285 EndY=-6.5 EndZ=0
    g3: LineSegment StartX=64.285 StartY=-6.5 StartZ=0 EndX=64.285 EndY=-1.3 EndZ=0
    g4: LineSegment StartX=64.285 StartY=-1.3 StartZ=0 EndX=58.085 EndY=-1.3 EndZ=0
    g5: LineSegment StartX=58.085 StartY=-1.3 StartZ=0 EndX=58.085 EndY=-0.3 EndZ=0
    g6: LineSegment StartX=58.085 StartY=-0.3 StartZ=0 EndX=55.485 EndY=-0.3 EndZ=0
    g7: LineSegment StartX=55.485 StartY=-0.3 StartZ=0 EndX=55.485 EndY=-1.3 EndZ=0
    g8: LineSegment StartX=55.485 StartY=-1.3 StartZ=0 EndX=49.285 EndY=-1.3 EndZ=0
    g9: GeomPoint X=56.785 Y=-3.9 Z=0
    g10: GeomPoint X=56.785 Y=-0.3 Z=0
    g11: GeomPoint X=56.785 Y=-8 Z=0
  constraints (28):
    c: Coincident(g1,g2)
    c: Coincident(g2,g3)
    c: Coincident(g3,g4)
    c: Coincident(g8,g1)
    c: Vertical(g1)
    c: Vertical(g3)
    c: Horizontal(g2)
    c: Horizontal(g4)
    c: Coincident(g5,g6)
    c: Coincident(g6,g7)
    c: Horizontal(g6)
    c: Vertical(g5)
    c: Vertical(g7)
    c: Coincident(g8,g7)
    c: Horizontal(g8)
    c: Horizontal(g7,g4)
    c: Symmetric(g1,g2,g9)
    c: Symmetric(g6,g5,g10)
    c: Coincident(g5,g4)
    c: DistanceY(g5,g5) = 1
    c: DistanceX(g6,g6) = 2.6
    c: DistanceY(g3,g3) = 5.2
    c: DistanceX(g2,g2) = 15
    c: Vertical(g10,g9)
    c: Vertical(g9,g0)
    c: DistanceY(g0,g2) = 1.5
    c: Symmetric(g-3,g-3,g11)
    c: Coincident(g0,g11)
FEATURE [PartDesign::Pocket] Pocket008  label="PocketWiringOpening"
  BaseFeature = -> Pad031
  Direction = (0,1,-2e-16)
  Length = 5
  Length2 = 5
  Profile = -> Sketch043
  ReferenceAxis = -> Sketch043 [N_Axis]
  Refine = true
  SideType = 0
  Suppressed = false
  Type = 2
  Type2 = 0
FEATURE [PartDesign::SubShapeBinder] Binder
  BindCopyOnChange = 0
  BindMode = 0
  ClaimChildren = false
  Context = -> Body [Binder.]
  Fuse = false
  MakeFace = true
  OffsetFill = false
  OffsetIntersection = false
  OffsetJoinType = 0
  OffsetOpenResult = false
  PartialLoad = false
  Refine = true
  Relative = true
  Support = -> [Body003[Pocket009.]]
  _Version = 2
FEATURE [Sketcher::SketchObject] Sketch  label="SketchBackOutline"
  ArcFitTolerance = 1e-06
  AttachmentSupport = -> [XY_Plane021]
  ExternalGeometry = -> [Binder]
  ExternalTypes = [0]
  FullyConstrained = true
  MakeInternals = false
  MapMode = 5
  sketch-geometry (8):
    g0: LineSegment StartX=116.87 StartY=6 StartZ=0 EndX=-3 EndY=6 EndZ=0
    g1: LineSegment StartX=-3 StartY=6 StartZ=0 EndX=-3 EndY=-71.81 EndZ=0
    g2: LineSegment StartX=-3 StartY=-71.81 StartZ=0 EndX=116.87 EndY=-71.81 EndZ=0
    g3: LineSegment StartX=116.87 StartY=-71.81 StartZ=0 EndX=116.87 EndY=6 EndZ=0
    g4: Circle CenterX=0 CenterY=-68.81 CenterZ=0 NormalX=0 NormalY=0 NormalZ=1 AngleXU=0 Radius=1.45
    g5: Circle CenterX=113.57 CenterY=-68.81 CenterZ=0 NormalX=0 NormalY=0 NormalZ=1 AngleXU=0 Radius=1.45
    g6: Circle CenterX=113.57 CenterY=2.7 CenterZ=0 NormalX=0 NormalY=0 NormalZ=1 AngleXU=0 Radius=1.45
    g7: Circle CenterX=0 CenterY=2.7 CenterZ=0 NormalX=0 NormalY=0 NormalZ=1 AngleXU=0 Radius=1.45
  constraints (18):
    c: Coincident(g0,g1)
    c: Coincident(g1,g2)
    c: Coincident(g2,g3)
    c: Coincident(g3,g0)
    c: Horizontal(g0)
    c: Horizontal(g2)
    c: Vertical(g1)
    c: Vertical(g3)
    c: Coincident(g0,g-4)
    c: Coincident(g1,g-6)
    c: Coincident(g5,g-7)
    c: Coincident(g6,g-8)
    c: Diameter(g4) = 2.9
    c: Equal(g4,g5)
    c: Coincident(g4,g-9)
    c: Coincident(g7,g-10)
    c: Equal(g7,g4)
    c: Equal(g4,g6)
FEATURE [PartDesign::Pad] Pad  label="PadCaseThickness"
  Direction = (0,0,1)
  Length = 5
  Length2 = 10
  Profile = -> Sketch
  ReferenceAxis = -> Sketch [N_Axis]
  Refine = true
  SideType = 0
  Suppressed = false
  Type = 0
  Type2 = 0
FEATURE [Sketcher::SketchObject] Sketch045  label="SketchMountingTabs"
  ArcFitTolerance = 1e-06
  AttachmentSupport = -> [Pad]
  ExternalGeometry = -> [Pad]
  ExternalTypes = [0]
  FullyConstrained = true
  MakeInternals = false
  MapMode = 5
  Placement = pos=(0,0,0) rot=(1,0,0;3.14159rad)
  sketch-geometry (24):
    g0: Circle CenterX=123.87 CenterY=58.84 CenterZ=0 NormalX=0 NormalY=0 NormalZ=1 AngleXU=0 Radius=2.5
    g1: Circle CenterX=-10 CenterY=58.84 CenterZ=0 NormalX=0 NormalY=0 NormalZ=1 AngleXU=0 Radius=2.5
    g2: Circle CenterX=-10 CenterY=6.97 CenterZ=0 NormalX=0 NormalY=0 NormalZ=1 AngleXU=0 Radius=2.5
    g3: Circle CenterX=123.87 CenterY=6.97 CenterZ=0 NormalX=0 NormalY=0 NormalZ=1 AngleXU=0 Radius=2.5
    g4: GeomPoint X=-3 Y=32.905 Z=0
    g5: GeomPoint X=116.87 Y=32.905 Z=0
    g6: GeomPoint X=-10 Y=32.905 Z=0
    g7: GeomPoint X=123.87 Y=32.905 Z=0
    g8: ArcOfCircle CenterX=-10 CenterY=58.84 CenterZ=0 NormalX=0 NormalY=0 NormalZ=1 AngleXU=0 Radius=5 StartAngle=1.48389 EndAngle=4.79929
    g9: ArcOfCircle CenterX=-10 CenterY=6.97 CenterZ=0 NormalX=0 NormalY=0 NormalZ=1 AngleXU=0 Radius=5 StartAngle=1.48389 EndAngle=4.79929
    g10: ArcOfCircle CenterX=123.87 CenterY=6.97 CenterZ=0 NormalX=0 NormalY=0 NormalZ=1 AngleXU=0 Radius=5 StartAngle=4.62549 EndAngle=7.94088
    g11: ArcOfCircle CenterX=123.87 CenterY=58.84 CenterZ=0 NormalX=0 NormalY=0 NormalZ=1 AngleXU=0 Radius=5 StartAngle=4.62549 EndAngle=7.94088
    g12: ArcOfCircle CenterX=122.912 CenterY=47.84 CenterZ=0 NormalX=0 NormalY=0 NormalZ=1 AngleXU=0 Radius=6.04167 StartAngle=1.48389 EndAngle=3.14159
    g13: ArcOfCircle CenterX=122.912 CenterY=69.84 CenterZ=0 NormalX=0 NormalY=0 NormalZ=1 AngleXU=0 Radius=6.04167 StartAngle=3.14159 EndAngle=4.79929
    g14: ArcOfCircle CenterX=122.912 CenterY=17.97 CenterZ=0 NormalX=0 NormalY=0 NormalZ=1 AngleXU=0 Radius=6.04167 StartAngle=3.14159 EndAngle=4.79929
    g15: ArcOfCircle CenterX=122.912 CenterY=-4.03 CenterZ=0 NormalX=0 NormalY=0 NormalZ=1 AngleXU=0 Radius=6.04167 StartAngle=1.48389 EndAngle=3.14159
    g16: ArcOfCircle CenterX=-9.04167 CenterY=-4.03 CenterZ=0 NormalX=0 NormalY=0 NormalZ=1 AngleXU=0 Radius=6.04167 StartAngle=0 EndAngle=1.6577
    g17: ArcOfCircle CenterX=-9.04167 CenterY=17.97 CenterZ=0 NormalX=0 NormalY=0 NormalZ=1 AngleXU=0 Radius=6.04167 StartAngle=4.62549 EndAngle=6.28319
    g18: ArcOfCircle CenterX=-9.04167 CenterY=47.84 CenterZ=0 NormalX=0 NormalY=0 NormalZ=1 AngleXU=0 Radius=6.04167 StartAngle=0 EndAngle=1.6577
    g19: ArcOfCircle CenterX=-9.04167 CenterY=69.84 CenterZ=0 NormalX=0 NormalY=0 NormalZ=1 AngleXU=0 Radius=6.04167 StartAngle=4.62549 EndAngle=6.28319
    g20: LineSegment StartX=-3 StartY=69.84 StartZ=0 EndX=-3 EndY=47.84 EndZ=0
    g21: LineSegment StartX=-3 StartY=17.97 StartZ=0 EndX=-3 EndY=-4.03 EndZ=0
    g22: LineSegment StartX=116.87 StartY=17.97 StartZ=0 EndX=116.87 EndY=-4.03 EndZ=0
    g23: LineSegment StartX=116.87 StartY=69.84 StartZ=0 EndX=116.87 EndY=47.84 EndZ=0
  constraints (58):
    c: Distance(g0,g-6) = 7
    c: Diameter(g0) = 5
    c: Equal(g0,g2)
    c: Equal(g2,g1)
    c: Horizontal(g1,g0)
    c: Equal(g0,g3)
    c: Vertical(g0,g3)
    c: Symmetric(g-5,g-5,g4)
    c: Symmetric(g-6,g-6,g5)
    c: Symmetric(g0,g3,g7)
    c: Symmetric(g1,g2,g6)
    c: Horizontal(g6,g4)
    c: Horizontal(g5,g7)
    c: Vertical(g2,g1)
    c: DistanceX(g1,g-5) = 7
    c: DistanceY(g-5,g-5) = 77.81
    c: DistanceY(g1,g-5) = 12.97
    c: PointOnObject(g15,g-6)
    c: PointOnObject(g16,g-5)
    c: Tangent(g19,g-5) = -1.5708
    c: Tangent(g19,g8) = 1.5708
    c: Tangent(g18,g8) = 1.5708
    c: Coincident(g8,g1)
    c: Vertical(g8,g8)
    c: DistanceY(g18,g19) = 22
    c: Radius(g8) = 5
    c: Tangent(g17,g-5) = -1.5708
    c: Tangent(g17,g9) = 1.5708
    c: Tangent(g16,g9) = 1.5708
    c: Equal(g9,g8)
    c: Coincident(g9,g2)
    c: DistanceY(g16,g17) = 22
    c: Vertical(g9,g9)
    c: Vertical(g9,g8)
    c: Tangent(g13,g-6) = -1.5708
    c: Tangent(g13,g11) = 1.5708
    c: Tangent(g12,g11) = 1.5708
    c: Tangent(g12,g-6) = -1.5708
    c: Coincident(g11,g0)
    c: Vertical(g11,g11)
    c: Equal(g8,g11)
    c: Horizontal(g13,g19)
    c: Tangent(g14,g-6) = -1.5708
    c: Tangent(g14,g10) = 1.5708
    c: Tangent(g15,g10) = 1.5708
    c: Vertical(g10,g10)
    c: Vertical(g10,g11)
    c: Coincident(g10,g3)
    c: Tangent(g-6,g15,g15) = -1.5708
    c: Horizontal(g14,g17)
    c: Tangent(g20,g19) = 1.5708
    c: Coincident(g20,g18)
    c: Coincident(g21,g17)
    c: Tangent(g21,g16) = 1.5708
    c: Coincident(g22,g14)
    c: Coincident(g22,g15)
    c: Coincident(g23,g13)
    c: Coincident(g23,g12)
FEATURE [PartDesign::Pad] Pad032  label="PadMountingTabs"
  BaseFeature = -> Pad
  Direction = (0,0,-1)
  Length = 5
  Length2 = 10
  Profile = -> Sketch045
  ReferenceAxis = -> Sketch045 [N_Axis]
  Refine = true
  Reversed = true
  SideType = 0
  Suppressed = false
  Type = 0
  Type2 = 0
FEATURE [Sketcher::SketchObject] Sketch046
  ArcFitTolerance = 1e-06
  AttachmentSupport = -> [Pad032]
  ExternalGeometry = -> [Pad032]
  ExternalTypes = [0]
  FullyConstrained = true
  MakeInternals = false
  MapMode = 5
  Placement = pos=(0,0,0) rot=(1,0,0;3.14159rad)
  sketch-geometry (4):
    g0: Circle CenterX=0 CenterY=-2.7 CenterZ=0 NormalX=0 NormalY=0 NormalZ=1 AngleXU=0 Radius=2.3
    g1: Circle CenterX=113.57 CenterY=-2.7 CenterZ=0 NormalX=0 NormalY=0 NormalZ=1 AngleXU=0 Radius=2.3
    g2: Circle CenterX=113.57 CenterY=68.81 CenterZ=0 NormalX=0 NormalY=0 NormalZ=1 AngleXU=0 Radius=2.3
    g3: Circle CenterX=0 CenterY=68.81 CenterZ=0 NormalX=0 NormalY=0 NormalZ=1 AngleXU=0 Radius=2.3
  constraints (8):
    c: Coincident(g1,g-4)
    c: Coincident(g2,g-3)
    c: Diameter(g3) = 4.6
    c: Equal(g3,g2)
    c: Equal(g2,g1)
    c: Equal(g1,g0)
    c: Coincident(g3,g-5)
    c: Coincident(g-6,g0)
FEATURE [PartDesign::Pocket] Pocket
  BaseFeature = -> Pad032
  Direction = (0,0,1)
  Length = 3.5
  Length2 = 5
  Profile = -> Sketch046
  ReferenceAxis = -> Sketch046 [N_Axis]
  Refine = true
  SideType = 0
  Suppressed = false
  Type = 0
  Type2 = 0
FEATURE [Sketcher::SketchObject] Sketch048
  ArcFitTolerance = 1e-06
  ExternalTypes = [0]
  FullyConstrained = true
  MakeInternals = false
  MapMode = 5
  Placement = pos=(0,0,6.18) rot=(0,0,1;0rad)
  sketch-geometry (4):
    g0: Circle CenterX=5.17408 CenterY=-5.02733 CenterZ=0 NormalX=0 NormalY=0 NormalZ=1 AngleXU=0 Radius=1.6
    g1: Circle CenterX=5.17408 CenterY=-61.5799 CenterZ=0 NormalX=0 NormalY=0 NormalZ=1 AngleXU=0 Radius=1.6
    g2: Circle CenterX=108.174 CenterY=-61.5799 CenterZ=0 NormalX=0 NormalY=0 NormalZ=1 AngleXU=0 Radius=1.6
    g3: Circle CenterX=108.174 CenterY=-5.02733 CenterZ=0 NormalX=0 NormalY=0 NormalZ=1 AngleXU=0 Radius=1.6
  constraints (8):
    c: Coincident(g0,g-3)
    c: Equal(g0,g-3)
    c: Coincident(g1,g-4)
    c: Equal(g1,g-4)
    c: Coincident(g2,g-5)
    c: Equal(g2,g-5)
    c: Coincident(g3,g-6)
    c: Equal(g3,g-6)
FEATURE [PartDesign::Pad] Pad033  label="PadFaceHoleFill"
  BaseFeature = -> Pocket008
  Direction = (0,0,1)
  Length = 1.5
  Length2 = 10
  Profile = -> Sketch048
  ReferenceAxis = -> Sketch048 [N_Axis]
  Refine = true
  Reversed = true
  SideType = 0
  Suppressed = false
  Type = 0
  Type2 = 0
  expr: Length = <<VarSetButtonDimensions>>.button_cap_wall_thickness
FEATURE [Sketcher::SketchObject] Sketch049  label="SketchPcbStopBar"
  ArcFitTolerance = 1e-06
  AttachmentSupport = -> [Pad033]
  ExternalGeometry = -> [Pad033]
  ExternalTypes = [0]
  FullyConstrained = true
  MakeInternals = false
  MapMode = 5
  Placement = pos=(0,0,0) rot=(1,0,0;3.14159rad)
  expr: Constraints[11] = <<VarSetButtonDimensions>>.button_cap_wall_thickness
  sketch-geometry (6):
    g0: LineSegment StartX=11.935 StartY=64.56 StartZ=0 EndX=11.935 EndY=66.06 EndZ=0
    g1: LineSegment StartX=11.935 StartY=66.06 StartZ=0 EndX=101.935 EndY=66.06 EndZ=0
    g2: LineSegment StartX=101.935 StartY=66.06 StartZ=0 EndX=101.935 EndY=64.56 EndZ=0
    g3: LineSegment StartX=101.935 StartY=64.56 StartZ=0 EndX=11.935 EndY=64.56 EndZ=0
    g4: GeomPoint [constr] X=56.935 Y=65.31 Z=0
    g5: GeomPoint X=56.935 Y=71.81 Z=0
  constraints (14):
    c: Coincident(g0,g1)
    c: Coincident(g1,g2)
    c: Coincident(g2,g3)
    c: Coincident(g3,g0)
    c: Vertical(g0)
    c: Vertical(g2)
    c: Horizontal(g1)
    c: Horizontal(g3)
    c: Symmetric(g2,g0,g4)
    c: Symmetric(g-3,g-3,g5)
    c: Vertical(g4,g5)
    c: DistanceY(g2,g2) = 1.5
    c: DistanceX(g3,g3) = 90
    c: Distance(g4,g5) = 6.5
FEATURE [PartDesign::Pad] Pad034  label="PadPcbStopBar"
  BaseFeature = -> Pad033
  Direction = (0,0,-1)
  Length = 3.2
  Length2 = 10
  Profile = -> Sketch049
  ReferenceAxis = -> Sketch049 [N_Axis]
  Refine = true
  SideType = 0
  Suppressed = false
  Type = 0
  Type2 = 0
FEATURE [PartDesign::Plane] DatumPlane
  AttachmentOffset = pos=(0,0,-38.905) rot=(0,0,1;0rad)
  AttachmentSupport = -> [Pad034]
  Length = 158.715
  MapMode = 5
  Placement = pos=(0,-32.905,-8.6e-15) rot=(1,0,0;1.5708rad)
  ResizeMode = 0
  Width = 66.8446
FEATURE [PartDesign::Mirrored] Mirrored
  BaseFeature = -> Pad034
  MirrorPlane = -> DatumPlane
  Originals = -> [Pad034]
  Refine = true
  Suppressed = false
  TransformMode = 0
FEATURE [App::Link] BodyFrontMountPcbButtonCover  label="BodyFrontMountPcbButtonCover001"
  LinkedObject = -> Body003
FEATURE [App::FeaturePython] GroundedJoint  # Assembly grounded joint (typed FeaturePython)
  ObjectToGround = -> BodyFrontMountPcbButtonCover
FEATURE [App::Link] trailer_switch_panel_eight_buttons_v2  label="trailer-switch-panel-eight-buttons-v003"
  LinkPlacement = pos=(-107.514,5.02733,0.6) rot=(1,0,0;3.14159rad)
  LinkedObject = -> Board_cc028
  Placement = pos=(-107.514,5.02733,0.6) rot=(1,0,0;3.14159rad)
FEATURE [App::Link] BodyButtonCap  label="BodyButtonCap001"
  LinkPlacement = pos=(-93.3141,-46.2527,7.3) rot=(0,0,1;0rad)
  LinkedObject = -> Body004
  Placement = pos=(-93.3141,-46.2527,7.3) rot=(0,0,1;0rad)
FEATURE [App::Link] BodyButtonCap001  label="BodyButtonCap002"
  LinkPlacement = pos=(561.88,-238,87.57) rot=(0,0,1;3.14159rad)
  LinkedObject = -> Body004
  Placement = pos=(561.88,-238,87.57) rot=(0,0,1;3.14159rad)
FEATURE [App::Link] BodyButtonCap002  label="BodyButtonCap003"
  LinkPlacement = pos=(785.96,-238,87.57) rot=(0,0,1;3.14159rad)
  LinkedObject = -> Body004
  Placement = pos=(785.96,-238,87.57) rot=(0,0,1;3.14159rad)
FEATURE [App::Link] BodyButtonCap003  label="BodyButtonCap004"
  LinkPlacement = pos=(115.4,-560.36,87.57) rot=(0,0,1;0rad)
  LinkedObject = -> Body004
  Placement = pos=(115.4,-560.36,87.57) rot=(0,0,1;0rad)
FEATURE [App::Link] BodyButtonCap004  label="BodyButtonCap005"
  LinkPlacement = pos=(1227.64,-560.36,87.57) rot=(0,0,1;0rad)
  LinkedObject = -> Body004
  Placement = pos=(1227.64,-560.36,87.57) rot=(0,0,1;0rad)
FEATURE [App::Link] BodyButtonCap005  label="BodyButtonCap006"
  LinkPlacement = pos=(449.48,-560.36,87.57) rot=(0,0,1;0rad)
  LinkedObject = -> Body004
  Placement = pos=(449.48,-560.36,87.57) rot=(0,0,1;0rad)
FEATURE [App::Link] BodyButtonCap006  label="BodyButtonCap007"
  LinkPlacement = pos=(1230.04,-128,87.57) rot=(0,0,1;0rad)
  LinkedObject = -> Body004
  Placement = pos=(1230.04,-128,87.57) rot=(0,0,1;0rad)
FEATURE [App::Link] BodyButtonCap007  label="BodyButtonCap008"
  LinkPlacement = pos=(893.56,-560.36,87.57) rot=(0,0,1;0rad)
  LinkedObject = -> Body004
  Placement = pos=(893.56,-560.36,87.57) rot=(0,0,1;0rad)
FEATURE [App::Link] BodyCaseBack  label="BodyCaseBack001"
  LinkPlacement = pos=(-6.24549,-5.05144,-64.6446) rot=(0,0,1;0rad)
  LinkedObject = -> Body
  Placement = pos=(-6.24549,-5.05144,-64.6446) rot=(0,0,1;0rad)
FEATURE [Sketcher::SketchObject] Sketch050  label="SketchButtonSkirt"
  ArcFitTolerance = 1e-06
  AttachmentSupport = -> [YZ_Plane014]
  ExternalGeometry = -> [Thickness001]
  ExternalTypes = [0]
  FullyConstrained = true
  MakeInternals = false
  MapMode = 5
  Placement = pos=(0,0,0) rot=(0.57735,0.57735,0.57735;2.0944rad)
  sketch-geometry (4):
    g0: LineSegment StartX=8 StartY=0 StartZ=0 EndX=8 EndY=2.5 EndZ=0
    g1: LineSegment StartX=8 StartY=2.5 StartZ=0 EndX=9 EndY=2.5 EndZ=0
    g2: LineSegment StartX=8 StartY=0 StartZ=0 EndX=9 EndY=0 EndZ=0
    g3: LineSegment StartX=9 StartY=2.5 StartZ=0 EndX=9 EndY=0 EndZ=0
  constraints (11):
    c: Coincident(g0,g-3)
    c: PointOnObject(g0,g-3)
    c: DistanceY(g0,g0) = 2.5
    c: Coincident(g1,g0)
    c: Horizontal(g1)
    c: Coincident(g2,g0)
    c: PointOnObject(g2,g-1)
    c: Coincident(g3,g1)
    c: Coincident(g3,g2)
    c: Vertical(g3)
    c: DistanceX(g1,g1) = 1
FEATURE [PartDesign::AdditivePipe] AdditivePipe  label="AdditivePipeButtonSkirt"
  AuxiliaryCurvilinear = true
  AuxiliarySpineTangent = false
  BaseFeature = -> Thickness001
  Binormal = (0,0,0)
  Mode = 0
  Profile = -> Sketch050
  Refine = true
  Spine = -> Thickness001 [Edge15,Edge18,Edge21,Edge23,Edge3,Edge6,Edge9,Edge12]
  SpineTangent = false
  Suppressed = false
  Transformation = 0
  Transition = 0
FEATURE [PartDesign::Pad] Pad035  label="PadButtonBottomContact"
  BaseFeature = -> AdditivePipe
  Direction = (0,0,-1)
  Length = 10
  Length2 = 10
  Profile = -> AdditivePipe [Face28]
  Refine = true
  SideType = 0
  Suppressed = false
  Type = 3
  Type2 = 0
  UpToFace = -> AdditivePipe [Face19]
FEATURE [PartDesign::Pocket] Pocket011  label="PocketBaseShorten"
  BaseFeature = -> Pad035
  Direction = (0,0,1)
  Length = 0.2
  Length2 = 5
  Profile = -> Pad035 [Face19]
  Refine = true
  SideType = 0
  Suppressed = false
  Type = 0
  Type2 = 0
FEATURE [PartDesign::Body] Body004  label="BodyButtonCapBlank"
  AllowCompound = false
  Group = -> [Sketch036,DatumPlane004,Pad026,Thickness001,Sketch050,AdditivePipe,Pad035,Pocket011]
  Origin = -> Origin014
  Placement = pos=(14.41,-15.25,1.6) rot=(0,0,1;0rad)
  Tip = -> Pocket011
FEATURE [App::FeaturePython] Joint005  label="Fixed005"  # Assembly joint (typed FeaturePython)
  Angle = 0
  AngleMax = 0
  AngleMin = 0
  Detach1 = false
  Detach2 = false
  Distance = 0
  Distance2 = 0
  EnableAngleMax = false
  EnableAngleMin = false
  EnableLengthMax = false
  EnableLengthMin = false
  JointType = 0 (Fixed)
  LengthMax = 0
  LengthMin = 0
  Offset2 = pos=(0,0,1) rot=(0,0,1;0rad)
  Placement1 = pos=(3.15,-2.25,4.3) rot=(0,1,0;3.14159rad)
  Placement2 = pos=(0,0,-0.8) rot=(0,1,0;3.14159rad)
  Reference1 = -> trailer_switch_panel_eight_buttons_v2 [Step_Models_cc028.Bot_cc028.SW8_SW_PUSH_6mm_76d8f6a7f289_ln_013.Face41,Step_Models_cc028.Bot_cc028.SW8_SW_PUSH_6mm_76d8f6a7f289_ln_013.Face41]
  Reference2 = -> BodyButtonCap [Face4,Face4]
  Suppressed = false
FEATURE [App::FeaturePython] Joint  label="Fixed"  # Assembly joint (typed FeaturePython)
  Angle = 0
  AngleMax = 0
  AngleMin = 0
  Detach1 = false
  Detach2 = false
  Distance = 0
  Distance2 = 0
  EnableAngleMax = false
  EnableAngleMin = false
  EnableLengthMax = false
  EnableLengthMin = false
  JointType = 0 (Fixed)
  LengthMax = 0
  LengthMin = 0
  Offset2 = pos=(0,0,2.2) rot=(0,0,1;0rad)
  Placement1 = pos=(131.751,-108.083,-1.6) rot=(0,0,1;0rad)
  Placement2 = pos=(0,0,2.2) rot=(0,0,1;0rad)
  Reference1 = -> trailer_switch_panel_eight_buttons_v2 [Board_Geoms_cc028.Pcb_cc028.Edge15,Board_Geoms_cc028.Pcb_cc028.Edge15]
  Reference2 = -> BodyFrontMountPcbButtonCover [?Edge699,?Edge699]
  Suppressed = false
FEATURE [Assembly::JointGroup] Joints
  Group = -> [GroundedJoint,Joint005,Joint]
FEATURE [Assembly::AssemblyObject] Assembly  label="AssemblyControllerHousing"
  Group = -> [Joints,BodyFrontMountPcbButtonCover,GroundedJoint,trailer_switch_panel_eight_buttons_v2,BodyButtonCap,BodyButtonCap001,BodyButtonCap002,BodyButtonCap003,BodyButtonCap004,BodyButtonCap005,BodyButtonCap006,BodyButtonCap007,BodyCaseBack,Joint005,Joint]
  Origin = -> Origin022
  Type = Assembly
FEATURE [Sketcher::SketchObject] Sketch051
  ArcFitTolerance = 1e-06
  AttachmentSupport = -> [Pocket]
  ExternalGeometry = -> [Pocket]
  ExternalTypes = [0]
  FullyConstrained = true
  MakeInternals = false
  MapMode = 5
  Placement = pos=(0,0,5) rot=(0,0,1;0rad)
  sketch-geometry (6):
    g0: GeomPoint X=56.935 Y=-32.905 Z=0
    g1: LineSegment StartX=7 StartY=1 StartZ=0 EndX=7 EndY=-66.81 EndZ=0
    g2: LineSegment StartX=7 StartY=-66.81 StartZ=0 EndX=106.87 EndY=-66.81 EndZ=0
    g3: LineSegment StartX=106.87 StartY=-66.81 StartZ=0 EndX=106.87 EndY=1 EndZ=0
    g4: LineSegment StartX=106.87 StartY=1 StartZ=0 EndX=7 EndY=1 EndZ=0
    g5: GeomPoint [constr] X=56.935 Y=-32.905 Z=0
  constraints (13):
    c: Symmetric(g-3,g-4,g0)
    c: Coincident(g1,g2)
    c: Coincident(g2,g3)
    c: Coincident(g3,g4)
    c: Coincident(g4,g1)
    c: Vertical(g1)
    c: Vertical(g3)
    c: Horizontal(g2)
    c: Horizontal(g4)
    c: Symmetric(g3,g1,g5)
    c: Coincident(g5,g0)
    c: DistanceY(g1,g-3) = 5
    c: DistanceX(g-3,g1) = 10
FEATURE [PartDesign::Pocket] Pocket012
  BaseFeature = -> Pocket
  Direction = (0,0,-1)
  Length = 2
  Length2 = 5
  Profile = -> Sketch051
  ReferenceAxis = -> Sketch051 [N_Axis]
  Refine = true
  SideType = 0
  Suppressed = false
  Type = 0
  Type2 = 0
FEATURE [Sketcher::SketchObject] Sketch053  label="SketchProgrammingOpening"
  ArcFitTolerance = 1e-06
  AttachmentSupport = -> [Mirrored]
  ExternalGeometry = -> [Binder006,Mirrored]
  ExternalTypes = [0]
  FullyConstrained = true
  MakeInternals = false
  MapMode = 5
  Placement = pos=(116.87,0,0) rot=(0.57735,0.57735,0.57735;2.0944rad)
  sketch-geometry (6):
    g0: LineSegment StartX=-40.71 StartY=-4.7 StartZ=0 EndX=-40.71 EndY=-8 EndZ=0
    g1: LineSegment StartX=-40.71 StartY=-8 StartZ=0 EndX=-24.71 EndY=-8 EndZ=0
    g2: LineSegment StartX=-24.71 StartY=-8 StartZ=0 EndX=-24.71 EndY=-4.7 EndZ=0
    g3: LineSegment StartX=-24.71 StartY=-4.7 StartZ=0 EndX=-40.71 EndY=-4.7 EndZ=0
    g4: GeomPoint X=-32.71 Y=-6.35 Z=0
    g5: GeomPoint X=-32.71 Y=-4.91 Z=0
  constraints (14):
    c: Coincident(g0,g1)
    c: Coincident(g1,g2)
    c: Coincident(g2,g3)
    c: Coincident(g3,g0)
    c: Vertical(g0)
    c: Vertical(g2)
    c: Horizontal(g1)
    c: Horizontal(g3)
    c: DistanceX(g1,g1) = 16
    c: DistanceY(g2,g2) = 3.3
    c: PointOnObject(g1,g-9)
    c: Symmetric(g0,g1,g4)
    c: Symmetric(g-6,g-8,g5)
    c: Vertical(g4,g5)
FEATURE [PartDesign::Pocket] Pocket014  label="PocketProgrammingOpening"
  BaseFeature = -> Mirrored
  Direction = (-1,0,0)
  Length = 5
  Length2 = 5
  Profile = -> Sketch053
  ReferenceAxis = -> Sketch053 [N_Axis]
  Refine = true
  SideType = 0
  Suppressed = false
  Type = 2
  Type2 = 0
FEATURE [Sketcher::SketchObject] Sketch055  label="SketchButtonCapBase001"
  ArcFitTolerance = 1e-06
  AttachmentSupport = -> [XY_Plane023]
  ExternalTypes = [0]
  FullyConstrained = true
  MakeInternals = false
  MapMode = 5
  expr: Constraints[19] = <<VarSetButtonDimensions001>>.Base_button_radius
  expr: Constraints[20] = <<VarSetButtonDimensions001>>.Base_button_height
  expr: Constraints[21] = <<VarSetButtonDimensions001>>.Base_button_width
  sketch-geometry (10):
    g0: LineSegment StartX=-5 StartY=-8 StartZ=0 EndX=5 EndY=-8 EndZ=0
    g1: LineSegment StartX=8 StartY=-5 StartZ=0 EndX=8 EndY=5 EndZ=0
    g2: LineSegment StartX=5 StartY=8 StartZ=0 EndX=-5 EndY=8 EndZ=0
    g3: LineSegment StartX=-8 StartY=5 StartZ=0 EndX=-8 EndY=-5 EndZ=0
    g4: ArcOfCircle CenterX=-5 CenterY=-5 CenterZ=0 NormalX=0 NormalY=0 NormalZ=1 AngleXU=0 Radius=3 StartAngle=3.14159 EndAngle=4.71239
    g5: ArcOfCircle CenterX=5 CenterY=-5 CenterZ=0 NormalX=0 NormalY=0 NormalZ=1 AngleXU=0 Radius=3 StartAngle=4.71239 EndAngle=6.28319
    g6: ArcOfCircle CenterX=5 CenterY=5 CenterZ=0 NormalX=0 NormalY=0 NormalZ=1 AngleXU=0 Radius=3 StartAngle=1e-16 EndAngle=1.5708
    g7: ArcOfCircle CenterX=-5 CenterY=5 CenterZ=0 NormalX=0 NormalY=0 NormalZ=1 AngleXU=0 Radius=3 StartAngle=1.5708 EndAngle=3.14159
    g8: GeomPoint [constr] X=8 Y=8 Z=0
    g9: GeomPoint [constr] X=0 Y=0 Z=0
  constraints (22):
    c: Tangent(g0,g4) = -1.5708
    c: Tangent(g0,g5) = -1.5708
    c: Tangent(g1,g5) = -1.5708
    c: Tangent(g1,g6) = -1.5708
    c: Tangent(g2,g6) = -1.5708
    c: Tangent(g2,g7) = -1.5708
    c: Tangent(g3,g7) = -1.5708
    c: Tangent(g3,g4) = -1.5708
    c: Horizontal(g0)
    c: Horizontal(g2)
    c: Vertical(g1)
    c: Vertical(g3)
    c: Equal(g4,g5)
    c: Equal(g5,g6)
    c: Equal(g6,g7)
    c: Symmetric(g2,g0,g9)
    c: PointOnObject(g8,g1)
    c: PointOnObject(g8,g2)
    c: Coincident(g9,g-1)
    c: Radius(g5) = 3
    c: DistanceY(g0,g2) = 16
    c: DistanceX(g3,g1) = 16
FEATURE [PartDesign::Plane] DatumPlane005
  AttachmentSupport = -> [Sketch055]
  Length = 60
  MapMode = 7
  Placement = pos=(8,-5,0) rot=(1,0,0;1.5708rad)
  ResizeMode = 0
  Width = 60
FEATURE [PartDesign::Pad] Pad036  label="PadButtonCapPlusBase001"
  Direction = (0,0,1)
  Length = 4.59
  Length2 = 10
  Profile = -> Sketch055
  ReferenceAxis = -> Sketch055 [N_Axis]
  Refine = true
  SideType = 0
  Suppressed = false
  Type = 0
  Type2 = 0
  expr: Length = <<VarSetButtonDimensions001>>.button_cap_height + <<VarSetButtonDimensions001>>.Base_button_slide_depth + <<VarSetButtonDimensions001>>.Base_base_thickness
FEATURE [PartDesign::Thickness] Thickness002  label="ThicknessCapWall001"
  Base = -> Pad036 [Face9]
  BaseFeature = -> Pad036
  Intersection = false
  Join = 0
  Mode = 0
  Refine = true
  Reversed = true
  SupportTransform = false
  Suppressed = false
  Value = 1.5
  expr: Value = <<VarSetButtonDimensions001>>.button_cap_wall_thickness
FEATURE [Sketcher::SketchObject] Sketch056  label="SketchButtonSkirt001"
  ArcFitTolerance = 1e-06
  AttachmentSupport = -> [YZ_Plane023]
  ExternalGeometry = -> [Thickness002]
  ExternalTypes = [0]
  FullyConstrained = true
  MakeInternals = false
  MapMode = 5
  Placement = pos=(0,0,0) rot=(0.57735,0.57735,0.57735;2.0944rad)
  sketch-geometry (4):
    g0: LineSegment StartX=8 StartY=0 StartZ=0 EndX=8 EndY=2.5 EndZ=0
    g1: LineSegment StartX=8 StartY=2.5 StartZ=0 EndX=9 EndY=2.5 EndZ=0
    g2: LineSegment StartX=8 StartY=0 StartZ=0 EndX=9 EndY=0 EndZ=0
    g3: LineSegment StartX=9 StartY=2.5 StartZ=0 EndX=9 EndY=0 EndZ=0
  constraints (11):
    c: Coincident(g0,g-3)
    c: PointOnObject(g0,g-3)
    c: DistanceY(g0,g0) = 2.5
    c: Coincident(g1,g0)
    c: Horizontal(g1)
    c: Coincident(g2,g0)
    c: PointOnObject(g2,g-1)
    c: Coincident(g3,g1)
    c: Coincident(g3,g2)
    c: Vertical(g3)
    c: DistanceX(g1,g1) = 1
FEATURE [PartDesign::AdditivePipe] AdditivePipe001  label="AdditivePipeButtonSkirt001"
  AuxiliaryCurvilinear = true
  AuxiliarySpineTangent = false
  BaseFeature = -> Thickness002
  Binormal = (0,0,0)
  Mode = 0
  Profile = -> Sketch056
  Refine = true
  Spine = -> Thickness002 [Edge15,Edge18,Edge21,Edge23,Edge3,Edge6,Edge9,Edge12]
  SpineTangent = false
  Suppressed = false
  Transformation = 0
  Transition = 0
FEATURE [PartDesign::Pad] Pad037  label="PadButtonBottomContact001"
  BaseFeature = -> AdditivePipe001
  Direction = (0,0,-1)
  Length = 10
  Length2 = 10
  Profile = -> AdditivePipe001 [Face28]
  Refine = true
  SideType = 0
  Suppressed = false
  Type = 3
  Type2 = 0
  UpToFace = -> AdditivePipe001 [Face19]
FEATURE [PartDesign::Pocket] Pocket015  label="PocketBaseShorten001"
  BaseFeature = -> Pad037
  Direction = (0,0,1)
  Length = 0.2
  Length2 = 5
  Profile = -> Pad037 [Face19]
  Refine = true
  SideType = 0
  Suppressed = false
  Type = 0
  Type2 = 0
FEATURE [Sketcher::SketchObject] Sketch057  label="SketchLightBulb001"
  ArcFitTolerance = 1e-06
  AttachmentOffset = pos=(-63,8,0) rot=(0,0,1;0rad)
  AttachmentSupport = -> [Pocket015]
  ExternalTypes = [0]
  FullyConstrained = false
  MakeInternals = false
  MapMode = 5
  Placement = pos=(-63,8,4.59) rot=(0,0,1;0rad)
  sketch-geometry (15):
    g0: BSplineCurve PolesCount=4 KnotsCount=2 Degree=3 IsPeriodic=0
    g1: BSplineCurve PolesCount=4 KnotsCount=2 Degree=3 IsPeriodic=0
    g2: BSplineCurve PolesCount=4 KnotsCount=2 Degree=3 IsPeriodic=0
    g3: BSplineCurve PolesCount=4 KnotsCount=2 Degree=3 IsPeriodic=0
    g4: BSplineCurve PolesCount=4 KnotsCount=2 Degree=3 IsPeriodic=0
    g5: BSplineCurve PolesCount=4 KnotsCount=2 Degree=3 IsPeriodic=0
    g6: BSplineCurve PolesCount=4 KnotsCount=2 Degree=3 IsPeriodic=0
    g7: BSplineCurve PolesCount=4 KnotsCount=2 Degree=3 IsPeriodic=0
    g8: BSplineCurve PolesCount=2 KnotsCount=2 Degree=1 IsPeriodic=0
    g9: BSplineCurve PolesCount=2 KnotsCount=2 Degree=1 IsPeriodic=0
    g10: BSplineCurve PolesCount=4 KnotsCount=2 Degree=3 IsPeriodic=0
    g11: BSplineCurve PolesCount=2 KnotsCount=2 Degree=1 IsPeriodic=0
    g12: BSplineCurve PolesCount=2 KnotsCount=2 Degree=1 IsPeriodic=0
    g13: BSplineCurve PolesCount=2 KnotsCount=2 Degree=1 IsPeriodic=0
    g14: BSplineCurve PolesCount=4 KnotsCount=2 Degree=3 IsPeriodic=0
  constraints (15):
    c: Coincident(g0,g1)
    c: Coincident(g1,g2)
    c: Coincident(g2,g3)
    c: Coincident(g3,g4)
    c: Coincident(g4,g5)
    c: Coincident(g5,g6)
    c: Coincident(g6,g7)
    c: Coincident(g7,g8)
    c: Coincident(g8,g9)
    c: Coincident(g9,g0)
    c: Coincident(g10,g11)
    c: Coincident(g11,g12)
    c: Coincident(g12,g13)
    c: Coincident(g13,g14)
    c: Coincident(g14,g10)
FEATURE [PartDesign::Pocket] Pocket016  label="PocketLightBulb001"
  BaseFeature = -> Pocket015
  Direction = (0,0,-1)
  Length = 0.2
  Length2 = 5
  Profile = -> Sketch057
  ReferenceAxis = -> Sketch057 [N_Axis]
  Refine = true
  SideType = 0
  Suppressed = false
  Type = 0
  Type2 = 0
FEATURE [PartDesign::Body] Body005  label="BodyButtonCapBulb"
  AllowCompound = false
  Group = -> [Sketch055,DatumPlane005,Pad036,Thickness002,Sketch056,AdditivePipe001,Pad037,Pocket015,Sketch057,Pocket016]
  Origin = -> Origin023
  Placement = pos=(42.19,-15.25,1.6) rot=(0,0,1;0rad)
  Tip = -> Pocket016
FEATURE [App::VarSet] VarSet003  label="VarSetButtonDimensions001"
  Base_base_thickness = 1.5
  Base_button_height = 16
  Base_button_radius = 3
  Base_button_slide_depth = 0.09
  Base_button_width = 16
  button_cap_height = 3
  button_cap_wall_thickness = 1.5
  button_snap_thickness = 0.5
  button_tab_depth = 1
  tolerance = 0.4
FEATURE [Sketcher::SketchObject] Sketch059  label="SketchButtonCapBase002"
  ArcFitTolerance = 1e-06
  AttachmentSupport = -> [XY_Plane024]
  ExternalTypes = [0]
  FullyConstrained = true
  MakeInternals = false
  MapMode = 5
  expr: Constraints[19] = <<VarSetButtonDimensions002>>.Base_button_radius
  expr: Constraints[20] = <<VarSetButtonDimensions002>>.Base_button_height
  expr: Constraints[21] = <<VarSetButtonDimensions002>>.Base_button_width
  sketch-geometry (10):
    g0: LineSegment StartX=-5 StartY=-8 StartZ=0 EndX=5 EndY=-8 EndZ=0
    g1: LineSegment StartX=8 StartY=-5 StartZ=0 EndX=8 EndY=5 EndZ=0
    g2: LineSegment StartX=5 StartY=8 StartZ=0 EndX=-5 EndY=8 EndZ=0
    g3: LineSegment StartX=-8 StartY=5 StartZ=0 EndX=-8 EndY=-5 EndZ=0
    g4: ArcOfCircle CenterX=-5 CenterY=-5 CenterZ=0 NormalX=0 NormalY=0 NormalZ=1 AngleXU=0 Radius=3 StartAngle=3.14159 EndAngle=4.71239
    g5: ArcOfCircle CenterX=5 CenterY=-5 CenterZ=0 NormalX=0 NormalY=0 NormalZ=1 AngleXU=0 Radius=3 StartAngle=4.71239 EndAngle=6.28319
    g6: ArcOfCircle CenterX=5 CenterY=5 CenterZ=0 NormalX=0 NormalY=0 NormalZ=1 AngleXU=0 Radius=3 StartAngle=1e-16 EndAngle=1.5708
    g7: ArcOfCircle CenterX=-5 CenterY=5 CenterZ=0 NormalX=0 NormalY=0 NormalZ=1 AngleXU=0 Radius=3 StartAngle=1.5708 EndAngle=3.14159
    g8: GeomPoint [constr] X=8 Y=8 Z=0
    g9: GeomPoint [constr] X=0 Y=0 Z=0
  constraints (22):
    c: Tangent(g0,g4) = -1.5708
    c: Tangent(g0,g5) = -1.5708
    c: Tangent(g1,g5) = -1.5708
    c: Tangent(g1,g6) = -1.5708
    c: Tangent(g2,g6) = -1.5708
    c: Tangent(g2,g7) = -1.5708
    c: Tangent(g3,g7) = -1.5708
    c: Tangent(g3,g4) = -1.5708
    c: Horizontal(g0)
    c: Horizontal(g2)
    c: Vertical(g1)
    c: Vertical(g3)
    c: Equal(g4,g5)
    c: Equal(g5,g6)
    c: Equal(g6,g7)
    c: Symmetric(g2,g0,g9)
    c: PointOnObject(g8,g1)
    c: PointOnObject(g8,g2)
    c: Coincident(g9,g-1)
    c: Radius(g5) = 3
    c: DistanceY(g0,g2) = 16
    c: DistanceX(g3,g1) = 16
FEATURE [PartDesign::Plane] DatumPlane006
  AttachmentSupport = -> [Sketch059]
  Length = 60
  MapMode = 7
  Placement = pos=(8,-5,0) rot=(1,0,0;1.5708rad)
  ResizeMode = 0
  Width = 60
FEATURE [PartDesign::Pad] Pad038  label="PadButtonCapPlusBase002"
  Direction = (0,0,1)
  Length = 4.59
  Length2 = 10
  Profile = -> Sketch059
  ReferenceAxis = -> Sketch059 [N_Axis]
  Refine = true
  SideType = 0
  Suppressed = false
  Type = 0
  Type2 = 0
  expr: Length = <<VarSetButtonDimensions002>>.button_cap_height + <<VarSetButtonDimensions002>>.Base_button_slide_depth + <<VarSetButtonDimensions002>>.Base_base_thickness
FEATURE [PartDesign::Thickness] Thickness003  label="ThicknessCapWall002"
  Base = -> Pad038 [Face9]
  BaseFeature = -> Pad038
  Intersection = false
  Join = 0
  Mode = 0
  Refine = true
  Reversed = true
  SupportTransform = false
  Suppressed = false
  Value = 1.5
  expr: Value = <<VarSetButtonDimensions002>>.button_cap_wall_thickness
FEATURE [Sketcher::SketchObject] Sketch060  label="SketchButtonSkirt002"
  ArcFitTolerance = 1e-06
  AttachmentSupport = -> [YZ_Plane024]
  ExternalGeometry = -> [Thickness003]
  ExternalTypes = [0]
  FullyConstrained = true
  MakeInternals = false
  MapMode = 5
  Placement = pos=(0,0,0) rot=(0.57735,0.57735,0.57735;2.0944rad)
  sketch-geometry (4):
    g0: LineSegment StartX=8 StartY=0 StartZ=0 EndX=8 EndY=2.5 EndZ=0
    g1: LineSegment StartX=8 StartY=2.5 StartZ=0 EndX=9 EndY=2.5 EndZ=0
    g2: LineSegment StartX=8 StartY=0 StartZ=0 EndX=9 EndY=0 EndZ=0
    g3: LineSegment StartX=9 StartY=2.5 StartZ=0 EndX=9 EndY=0 EndZ=0
  constraints (11):
    c: Coincident(g0,g-3)
    c: PointOnObject(g0,g-3)
    c: DistanceY(g0,g0) = 2.5
    c: Coincident(g1,g0)
    c: Horizontal(g1)
    c: Coincident(g2,g0)
    c: PointOnObject(g2,g-1)
    c: Coincident(g3,g1)
    c: Coincident(g3,g2)
    c: Vertical(g3)
    c: DistanceX(g1,g1) = 1
FEATURE [PartDesign::AdditivePipe] AdditivePipe002  label="AdditivePipeButtonSkirt002"
  AuxiliaryCurvilinear = true
  AuxiliarySpineTangent = false
  BaseFeature = -> Thickness003
  Binormal = (0,0,0)
  Mode = 0
  Profile = -> Sketch060
  Refine = true
  Spine = -> Thickness003 [Edge15,Edge18,Edge21,Edge23,Edge3,Edge6,Edge9,Edge12]
  SpineTangent = false
  Suppressed = false
  Transformation = 0
  Transition = 0
FEATURE [PartDesign::Pad] Pad039  label="PadButtonBottomContact002"
  BaseFeature = -> AdditivePipe002
  Direction = (0,0,-1)
  Length = 10
  Length2 = 10
  Profile = -> AdditivePipe002 [Face28]
  Refine = true
  SideType = 0
  Suppressed = false
  Type = 3
  Type2 = 0
  UpToFace = -> AdditivePipe002 [Face19]
FEATURE [PartDesign::Pocket] Pocket017  label="PocketBaseShorten002"
  BaseFeature = -> Pad039
  Direction = (0,0,1)
  Length = 0.2
  Length2 = 5
  Profile = -> Pad039 [Face19]
  Refine = true
  SideType = 0
  Suppressed = false
  Type = 0
  Type2 = 0
FEATURE [Sketcher::SketchObject] Sketch062  label="SketchWaterIcon"
  ArcFitTolerance = 1e-06
  AttachmentOffset = pos=(-25.25,20,0) rot=(0,0,1;0rad)
  AttachmentSupport = -> [Pocket017]
  ExternalTypes = [0]
  FullyConstrained = false
  MakeInternals = false
  MapMode = 5
  Placement = pos=(-25.25,20,4.59) rot=(0,0,1;0rad)
  sketch-geometry (63):
    g0: BSplineCurve PolesCount=4 KnotsCount=2 Degree=3 IsPeriodic=0
    g1: BSplineCurve PolesCount=4 KnotsCount=2 Degree=3 IsPeriodic=0
    g2: BSplineCurve PolesCount=4 KnotsCount=2 Degree=3 IsPeriodic=0
    g3: BSplineCurve PolesCount=4 KnotsCount=2 Degree=3 IsPeriodic=0
    g4: BSplineCurve PolesCount=4 KnotsCount=2 Degree=3 IsPeriodic=0
    g5: BSplineCurve PolesCount=4 KnotsCount=2 Degree=3 IsPeriodic=0
    g6: BSplineCurve PolesCount=4 KnotsCount=2 Degree=3 IsPeriodic=0
    g7: BSplineCurve PolesCount=4 KnotsCount=2 Degree=3 IsPeriodic=0
    g8: BSplineCurve PolesCount=4 KnotsCount=2 Degree=3 IsPeriodic=0
    g9: BSplineCurve PolesCount=4 KnotsCount=2 Degree=3 IsPeriodic=0
    g10: BSplineCurve PolesCount=4 KnotsCount=2 Degree=3 IsPeriodic=0
    g11: BSplineCurve PolesCount=4 KnotsCount=2 Degree=3 IsPeriodic=0
    g12: BSplineCurve PolesCount=4 KnotsCount=2 Degree=3 IsPeriodic=0
    g13: BSplineCurve PolesCount=4 KnotsCount=2 Degree=3 IsPeriodic=0
    g14: BSplineCurve PolesCount=4 KnotsCount=2 Degree=3 IsPeriodic=0
    g15: BSplineCurve PolesCount=4 KnotsCount=2 Degree=3 IsPeriodic=0
    g16: BSplineCurve PolesCount=4 KnotsCount=2 Degree=3 IsPeriodic=0
    g17: BSplineCurve PolesCount=4 KnotsCount=2 Degree=3 IsPeriodic=0
    g18: BSplineCurve PolesCount=4 KnotsCount=2 Degree=3 IsPeriodic=0
    g19: BSplineCurve PolesCount=4 KnotsCount=2 Degree=3 IsPeriodic=0
    g20: BSplineCurve PolesCount=4 KnotsCount=2 Degree=3 IsPeriodic=0
    g21: BSplineCurve PolesCount=4 KnotsCount=2 Degree=3 IsPeriodic=0
    g22: BSplineCurve PolesCount=4 KnotsCount=2 Degree=3 IsPeriodic=0
    g23: BSplineCurve PolesCount=4 KnotsCount=2 Degree=3 IsPeriodic=0
    g24: BSplineCurve PolesCount=4 KnotsCount=2 Degree=3 IsPeriodic=0
    g25: BSplineCurve PolesCount=4 KnotsCount=2 Degree=3 IsPeriodic=0
    g26: BSplineCurve PolesCount=4 KnotsCount=2 Degree=3 IsPeriodic=0
    g27: BSplineCurve PolesCount=4 KnotsCount=2 Degree=3 IsPeriodic=0
    g28: BSplineCurve PolesCount=4 KnotsCount=2 Degree=3 IsPeriodic=0
    g29: BSplineCurve PolesCount=4 KnotsCount=2 Degree=3 IsPeriodic=0
    g30: BSplineCurve PolesCount=4 KnotsCount=2 Degree=3 IsPeriodic=0
    g31: BSplineCurve PolesCount=4 KnotsCount=2 Degree=3 IsPeriodic=0
    g32: BSplineCurve PolesCount=4 KnotsCount=2 Degree=3 IsPeriodic=0
    g33: BSplineCurve PolesCount=4 KnotsCount=2 Degree=3 IsPeriodic=0
    g34: BSplineCurve PolesCount=4 KnotsCount=2 Degree=3 IsPeriodic=0
    g35: BSplineCurve PolesCount=4 KnotsCount=2 Degree=3 IsPeriodic=0
    g36: BSplineCurve PolesCount=4 KnotsCount=2 Degree=3 IsPeriodic=0
    g37: BSplineCurve PolesCount=4 KnotsCount=2 Degree=3 IsPeriodic=0
    g38: BSplineCurve PolesCount=4 KnotsCount=2 Degree=3 IsPeriodic=0
    g39: BSplineCurve PolesCount=4 KnotsCount=2 Degree=3 IsPeriodic=0
    g40: BSplineCurve PolesCount=4 KnotsCount=2 Degree=3 IsPeriodic=0
    g41: BSplineCurve PolesCount=4 KnotsCount=2 Degree=3 IsPeriodic=0
    g42: BSplineCurve PolesCount=4 KnotsCount=2 Degree=3 IsPeriodic=0
    g43: BSplineCurve PolesCount=4 KnotsCount=2 Degree=3 IsPeriodic=0
    g44: BSplineCurve PolesCount=4 KnotsCount=2 Degree=3 IsPeriodic=0
    g45: BSplineCurve PolesCount=4 KnotsCount=2 Degree=3 IsPeriodic=0
    g46: BSplineCurve PolesCount=4 KnotsCount=2 Degree=3 IsPeriodic=0
    g47: BSplineCurve PolesCount=4 KnotsCount=2 Degree=3 IsPeriodic=0
    g48: BSplineCurve PolesCount=4 KnotsCount=2 Degree=3 IsPeriodic=0
    g49: BSplineCurve PolesCount=4 KnotsCount=2 Degree=3 IsPeriodic=0
    g50: BSplineCurve PolesCount=4 KnotsCount=2 Degree=3 IsPeriodic=0
    g51: BSplineCurve PolesCount=4 KnotsCount=2 Degree=3 IsPeriodic=0
    g52: BSplineCurve PolesCount=4 KnotsCount=2 Degree=3 IsPeriodic=0
    g53: BSplineCurve PolesCount=4 KnotsCount=2 Degree=3 IsPeriodic=0
    g54: BSplineCurve PolesCount=4 KnotsCount=2 Degree=3 IsPeriodic=0
    g55: BSplineCurve PolesCount=4 KnotsCount=2 Degree=3 IsPeriodic=0
    g56: BSplineCurve PolesCount=4 KnotsCount=2 Degree=3 IsPeriodic=0
    g57: BSplineCurve PolesCount=4 KnotsCount=2 Degree=3 IsPeriodic=0
    g58: BSplineCurve PolesCount=4 KnotsCount=2 Degree=3 IsPeriodic=0
    g59: BSplineCurve PolesCount=4 KnotsCount=2 Degree=3 IsPeriodic=0
    g60: BSplineCurve PolesCount=4 KnotsCount=2 Degree=3 IsPeriodic=0
    g61: BSplineCurve PolesCount=4 KnotsCount=2 Degree=3 IsPeriodic=0
    g62: BSplineCurve PolesCount=4 KnotsCount=2 Degree=3 IsPeriodic=0
  constraints (63):
    c: Coincident(g0,g1)
    c: Coincident(g1,g2)
    c: Coincident(g2,g3)
    c: Coincident(g3,g4)
    c: Coincident(g4,g5)
    c: Coincident(g5,g6)
    c: Coincident(g6,g7)
    c: Coincident(g7,g8)
    c: Coincident(g8,g9)
    c: Coincident(g9,g10)
    c: Coincident(g10,g11)
    c: Coincident(g11,g12)
    c: Coincident(g12,g13)
    c: Coincident(g13,g14)
    c: Coincident(g14,g15)
    c: Coincident(g15,g16)
    c: Coincident(g16,g17)
    c: Coincident(g17,g18)
    c: Coincident(g18,g19)
    c: Coincident(g19,g20)
    c: Coincident(g20,g0)
    c: Coincident(g21,g22)
    c: Coincident(g22,g23)
    c: Coincident(g23,g24)
    c: Coincident(g24,g25)
    c: Coincident(g25,g26)
    c: Coincident(g26,g27)
    c: Coincident(g27,g28)
    c: Coincident(g28,g29)
    c: Coincident(g29,g30)
    c: Coincident(g30,g31)
    c: Coincident(g31,g32)
    c: Coincident(g32,g33)
    c: Coincident(g33,g34)
    c: Coincident(g34,g35)
    c: Coincident(g35,g36)
    c: Coincident(g36,g37)
    c: Coincident(g37,g38)
    c: Coincident(g38,g39)
    c: Coincident(g39,g40)
    c: Coincident(g40,g41)
    c: Coincident(g41,g21)
    c: Coincident(g42,g43)
    c: Coincident(g43,g44)
    c: Coincident(g44,g45)
    c: Coincident(g45,g46)
    c: Coincident(g46,g47)
    c: Coincident(g47,g48)
    c: Coincident(g48,g49)
    c: Coincident(g49,g50)
    c: Coincident(g50,g51)
    c: Coincident(g51,g52)
    c: Coincident(g52,g53)
    c: Coincident(g53,g54)
    c: Coincident(g54,g55)
    c: Coincident(g55,g56)
    c: Coincident(g56,g57)
    c: Coincident(g57,g58)
    c: Coincident(g58,g59)
    c: Coincident(g59,g60)
    c: Coincident(g60,g61)
    c: Coincident(g61,g62)
    c: Coincident(g62,g42)
FEATURE [App::VarSet] VarSet004  label="VarSetButtonDimensions002"
  Base_base_thickness = 1.5
  Base_button_height = 16
  Base_button_radius = 3
  Base_button_slide_depth = 0.09
  Base_button_width = 16
  button_cap_height = 3
  button_cap_wall_thickness = 1.5
  button_snap_thickness = 0.5
  button_tab_depth = 1
  tolerance = 0.4
FEATURE [Sketcher::SketchObject] Sketch063  label="SketchButtonCapBase003"
  ArcFitTolerance = 1e-06
  AttachmentSupport = -> [XY_Plane025]
  ExternalTypes = [0]
  FullyConstrained = true
  MakeInternals = false
  MapMode = 5
  expr: Constraints[19] = <<VarSetButtonDimensions003>>.Base_button_radius
  expr: Constraints[20] = <<VarSetButtonDimensions003>>.Base_button_height
  expr: Constraints[21] = <<VarSetButtonDimensions003>>.Base_button_width
  sketch-geometry (10):
    g0: LineSegment StartX=-5 StartY=-8 StartZ=0 EndX=5 EndY=-8 EndZ=0
    g1: LineSegment StartX=8 StartY=-5 StartZ=0 EndX=8 EndY=5 EndZ=0
    g2: LineSegment StartX=5 StartY=8 StartZ=0 EndX=-5 EndY=8 EndZ=0
    g3: LineSegment StartX=-8 StartY=5 StartZ=0 EndX=-8 EndY=-5 EndZ=0
    g4: ArcOfCircle CenterX=-5 CenterY=-5 CenterZ=0 NormalX=0 NormalY=0 NormalZ=1 AngleXU=0 Radius=3 StartAngle=3.14159 EndAngle=4.71239
    g5: ArcOfCircle CenterX=5 CenterY=-5 CenterZ=0 NormalX=0 NormalY=0 NormalZ=1 AngleXU=0 Radius=3 StartAngle=4.71239 EndAngle=6.28319
    g6: ArcOfCircle CenterX=5 CenterY=5 CenterZ=0 NormalX=0 NormalY=0 NormalZ=1 AngleXU=0 Radius=3 StartAngle=1e-16 EndAngle=1.5708
    g7: ArcOfCircle CenterX=-5 CenterY=5 CenterZ=0 NormalX=0 NormalY=0 NormalZ=1 AngleXU=0 Radius=3 StartAngle=1.5708 EndAngle=3.14159
    g8: GeomPoint [constr] X=8 Y=8 Z=0
    g9: GeomPoint [constr] X=0 Y=0 Z=0
  constraints (22):
    c: Tangent(g0,g4) = -1.5708
    c: Tangent(g0,g5) = -1.5708
    c: Tangent(g1,g5) = -1.5708
    c: Tangent(g1,g6) = -1.5708
    c: Tangent(g2,g6) = -1.5708
    c: Tangent(g2,g7) = -1.5708
    c: Tangent(g3,g7) = -1.5708
    c: Tangent(g3,g4) = -1.5708
    c: Horizontal(g0)
    c: Horizontal(g2)
    c: Vertical(g1)
    c: Vertical(g3)
    c: Equal(g4,g5)
    c: Equal(g5,g6)
    c: Equal(g6,g7)
    c: Symmetric(g2,g0,g9)
    c: PointOnObject(g8,g1)
    c: PointOnObject(g8,g2)
    c: Coincident(g9,g-1)
    c: Radius(g5) = 3
    c: DistanceY(g0,g2) = 16
    c: DistanceX(g3,g1) = 16
FEATURE [PartDesign::Plane] DatumPlane007
  AttachmentSupport = -> [Sketch063]
  Length = 60
  MapMode = 7
  Placement = pos=(8,-5,0) rot=(1,0,0;1.5708rad)
  ResizeMode = 0
  Width = 60
FEATURE [PartDesign::Pad] Pad040  label="PadButtonCapPlusBase003"
  Direction = (0,0,1)
  Length = 4.59
  Length2 = 10
  Profile = -> Sketch063
  ReferenceAxis = -> Sketch063 [N_Axis]
  Refine = true
  SideType = 0
  Suppressed = false
  Type = 0
  Type2 = 0
  expr: Length = <<VarSetButtonDimensions003>>.button_cap_height + <<VarSetButtonDimensions003>>.Base_button_slide_depth + <<VarSetButtonDimensions003>>.Base_base_thickness
FEATURE [PartDesign::Thickness] Thickness004  label="ThicknessCapWall003"
  Base = -> Pad040 [Face9]
  BaseFeature = -> Pad040
  Intersection = false
  Join = 0
  Mode = 0
  Refine = true
  Reversed = true
  SupportTransform = false
  Suppressed = false
  Value = 1.5
  expr: Value = <<VarSetButtonDimensions003>>.button_cap_wall_thickness
FEATURE [Sketcher::SketchObject] Sketch064  label="SketchButtonSkirt003"
  ArcFitTolerance = 1e-06
  AttachmentSupport = -> [YZ_Plane025]
  ExternalGeometry = -> [Thickness004]
  ExternalTypes = [0]
  FullyConstrained = true
  MakeInternals = false
  MapMode = 5
  Placement = pos=(0,0,0) rot=(0.57735,0.57735,0.57735;2.0944rad)
  sketch-geometry (4):
    g0: LineSegment StartX=8 StartY=0 StartZ=0 EndX=8 EndY=2.5 EndZ=0
    g1: LineSegment StartX=8 StartY=2.5 StartZ=0 EndX=9 EndY=2.5 EndZ=0
    g2: LineSegment StartX=8 StartY=0 StartZ=0 EndX=9 EndY=0 EndZ=0
    g3: LineSegment StartX=9 StartY=2.5 StartZ=0 EndX=9 EndY=0 EndZ=0
  constraints (11):
    c: Coincident(g0,g-3)
    c: PointOnObject(g0,g-3)
    c: DistanceY(g0,g0) = 2.5
    c: Coincident(g1,g0)
    c: Horizontal(g1)
    c: Coincident(g2,g0)
    c: PointOnObject(g2,g-1)
    c: Coincident(g3,g1)
    c: Coincident(g3,g2)
    c: Vertical(g3)
    c: DistanceX(g1,g1) = 1
FEATURE [PartDesign::AdditivePipe] AdditivePipe003  label="AdditivePipeButtonSkirt003"
  AuxiliaryCurvilinear = true
  AuxiliarySpineTangent = false
  BaseFeature = -> Thickness004
  Binormal = (0,0,0)
  Mode = 0
  Profile = -> Sketch064
  Refine = true
  Spine = -> Thickness004 [Edge15,Edge18,Edge21,Edge23,Edge3,Edge6,Edge9,Edge12]
  SpineTangent = false
  Suppressed = false
  Transformation = 0
  Transition = 0
FEATURE [PartDesign::Pad] Pad041  label="PadButtonBottomContact003"
  BaseFeature = -> AdditivePipe003
  Direction = (0,0,-1)
  Length = 10
  Length2 = 10
  Profile = -> AdditivePipe003 [Face28]
  Refine = true
  SideType = 0
  Suppressed = false
  Type = 3
  Type2 = 0
  UpToFace = -> AdditivePipe003 [Face19]
FEATURE [PartDesign::Pocket] Pocket019  label="PocketBaseShorten003"
  BaseFeature = -> Pad041
  Direction = (0,0,1)
  Length = 0.2
  Length2 = 5
  Profile = -> Pad041 [Face19]
  Refine = true
  SideType = 0
  Suppressed = false
  Type = 0
  Type2 = 0
FEATURE [App::VarSet] VarSet005  label="VarSetButtonDimensions003"
  Base_base_thickness = 1.5
  Base_button_height = 16
  Base_button_radius = 3
  Base_button_slide_depth = 0.09
  Base_button_width = 16
  button_cap_height = 3
  button_cap_wall_thickness = 1.5
  button_snap_thickness = 0.5
  button_tab_depth = 1
  tolerance = 0.4
FEATURE [PartDesign::Pocket] Pocket021
  BaseFeature = -> Pocket017
  Direction = (0,0,-1)
  Length = 0.2
  Length2 = 5
  Profile = -> Sketch062
  ReferenceAxis = -> Sketch062 [N_Axis]
  Refine = true
  SideType = 0
  Suppressed = false
  Type = 0
  Type2 = 0
FEATURE [PartDesign::Body] Body006  label="BodyButtonCapWater"
  AllowCompound = false
  Group = -> [Sketch059,DatumPlane006,Pad038,Thickness003,Sketch060,AdditivePipe002,Pad039,Pocket017,Sketch062,Pocket021]
  Origin = -> Origin024
  Placement = pos=(14.41,-15.25,1.6) rot=(0,0,1;0rad)
  Tip = -> Pocket021
FEATURE [Sketcher::SketchObject] Sketch065  label="SketchPowerIcon"
  ArcFitTolerance = 1e-06
  AttachmentOffset = pos=(-19.56,13,0) rot=(0,0,1;0rad)
  AttachmentSupport = -> [Pocket019]
  ExternalTypes = [0]
  FullyConstrained = false
  MakeInternals = false
  MapMode = 5
  Placement = pos=(-19.56,13,4.59) rot=(0,0,1;0rad)
  sketch-geometry (23):
    g0: BSplineCurve PolesCount=4 KnotsCount=2 Degree=3 IsPeriodic=0
    g1: BSplineCurve PolesCount=2 KnotsCount=2 Degree=1 IsPeriodic=0
    g2: BSplineCurve PolesCount=2 KnotsCount=2 Degree=1 IsPeriodic=0
    g3: BSplineCurve PolesCount=2 KnotsCount=2 Degree=1 IsPeriodic=0
    g4: BSplineCurve PolesCount=4 KnotsCount=2 Degree=3 IsPeriodic=0
    g5: BSplineCurve PolesCount=4 KnotsCount=2 Degree=3 IsPeriodic=0
    g6: BSplineCurve PolesCount=2 KnotsCount=2 Degree=1 IsPeriodic=0
    g7: BSplineCurve PolesCount=2 KnotsCount=2 Degree=1 IsPeriodic=0
    g8: BSplineCurve PolesCount=2 KnotsCount=2 Degree=1 IsPeriodic=0
    g9: BSplineCurve PolesCount=4 KnotsCount=2 Degree=3 IsPeriodic=0
    g10: BSplineCurve PolesCount=4 KnotsCount=2 Degree=3 IsPeriodic=0
    g11: BSplineCurve PolesCount=4 KnotsCount=2 Degree=3 IsPeriodic=0
    g12: BSplineCurve PolesCount=2 KnotsCount=2 Degree=1 IsPeriodic=0
    g13: BSplineCurve PolesCount=4 KnotsCount=2 Degree=3 IsPeriodic=0
    g14: BSplineCurve PolesCount=2 KnotsCount=2 Degree=1 IsPeriodic=0
    g15: BSplineCurve PolesCount=4 KnotsCount=2 Degree=3 IsPeriodic=0
    g16: BSplineCurve PolesCount=4 KnotsCount=2 Degree=3 IsPeriodic=0
    g17: BSplineCurve PolesCount=2 KnotsCount=2 Degree=1 IsPeriodic=0
    g18: BSplineCurve PolesCount=4 KnotsCount=2 Degree=3 IsPeriodic=0
    g19: BSplineCurve PolesCount=2 KnotsCount=2 Degree=1 IsPeriodic=0
    g20: BSplineCurve PolesCount=4 KnotsCount=2 Degree=3 IsPeriodic=0
    g21: BSplineCurve PolesCount=4 KnotsCount=2 Degree=3 IsPeriodic=0
    g22: BSplineCurve PolesCount=2 KnotsCount=2 Degree=1 IsPeriodic=0
  constraints (23):
    c: Coincident(g0,g1)
    c: Coincident(g1,g2)
    c: Coincident(g2,g3)
    c: Coincident(g3,g4)
    c: Coincident(g4,g0)
    c: Coincident(g5,g6)
    c: Coincident(g6,g7)
    c: Coincident(g7,g8)
    c: Coincident(g8,g9)
    c: Coincident(g9,g5)
    c: Coincident(g10,g11)
    c: Coincident(g11,g12)
    c: Coincident(g12,g13)
    c: Coincident(g13,g14)
    c: Coincident(g14,g15)
    c: Coincident(g15,g16)
    c: Coincident(g16,g17)
    c: Coincident(g17,g18)
    c: Coincident(g18,g19)
    c: Coincident(g19,g20)
    c: Coincident(g20,g21)
    c: Coincident(g21,g22)
    c: Coincident(g22,g10)
FEATURE [PartDesign::Pocket] Pocket022
  BaseFeature = -> Pocket019
  Direction = (0,0,-1)
  Length = 0.2
  Length2 = 5
  Profile = -> Sketch065
  ReferenceAxis = -> Sketch065 [N_Axis]
  Refine = true
  SideType = 0
  Suppressed = false
  Type = 0
  Type2 = 0
FEATURE [PartDesign::Body] Body007  label="BodyButtonCapPower"
  AllowCompound = false
  Group = -> [Sketch063,DatumPlane007,Pad040,Thickness004,Sketch064,AdditivePipe003,Pad041,Pocket019,Sketch065,Pocket022]
  Origin = -> Origin025
  Placement = pos=(69.92,-15.25,1.6) rot=(0,0,1;0rad)
  Tip = -> Pocket022
FEATURE [Sketcher::SketchObject] Sketch066  label="SketchButtonCapBase004"
  ArcFitTolerance = 1e-06
  AttachmentSupport = -> [XY_Plane026]
  ExternalTypes = [0]
  FullyConstrained = true
  MakeInternals = false
  MapMode = 5
  expr: Constraints[19] = <<VarSetButtonDimensions004>>.Base_button_radius
  expr: Constraints[20] = <<VarSetButtonDimensions004>>.Base_button_height
  expr: Constraints[21] = <<VarSetButtonDimensions004>>.Base_button_width
  sketch-geometry (10):
    g0: LineSegment StartX=-5 StartY=-8 StartZ=0 EndX=5 EndY=-8 EndZ=0
    g1: LineSegment StartX=8 StartY=-5 StartZ=0 EndX=8 EndY=5 EndZ=0
    g2: LineSegment StartX=5 StartY=8 StartZ=0 EndX=-5 EndY=8 EndZ=0
    g3: LineSegment StartX=-8 StartY=5 StartZ=0 EndX=-8 EndY=-5 EndZ=0
    g4: ArcOfCircle CenterX=-5 CenterY=-5 CenterZ=0 NormalX=0 NormalY=0 NormalZ=1 AngleXU=0 Radius=3 StartAngle=3.14159 EndAngle=4.71239
    g5: ArcOfCircle CenterX=5 CenterY=-5 CenterZ=0 NormalX=0 NormalY=0 NormalZ=1 AngleXU=0 Radius=3 StartAngle=4.71239 EndAngle=6.28319
    g6: ArcOfCircle CenterX=5 CenterY=5 CenterZ=0 NormalX=0 NormalY=0 NormalZ=1 AngleXU=0 Radius=3 StartAngle=1e-16 EndAngle=1.5708
    g7: ArcOfCircle CenterX=-5 CenterY=5 CenterZ=0 NormalX=0 NormalY=0 NormalZ=1 AngleXU=0 Radius=3 StartAngle=1.5708 EndAngle=3.14159
    g8: GeomPoint [constr] X=8 Y=8 Z=0
    g9: GeomPoint [constr] X=0 Y=0 Z=0
  constraints (22):
    c: Tangent(g0,g4) = -1.5708
    c: Tangent(g0,g5) = -1.5708
    c: Tangent(g1,g5) = -1.5708
    c: Tangent(g1,g6) = -1.5708
    c: Tangent(g2,g6) = -1.5708
    c: Tangent(g2,g7) = -1.5708
    c: Tangent(g3,g7) = -1.5708
    c: Tangent(g3,g4) = -1.5708
    c: Horizontal(g0)
    c: Horizontal(g2)
    c: Vertical(g1)
    c: Vertical(g3)
    c: Equal(g4,g5)
    c: Equal(g5,g6)
    c: Equal(g6,g7)
    c: Symmetric(g2,g0,g9)
    c: PointOnObject(g8,g1)
    c: PointOnObject(g8,g2)
    c: Coincident(g9,g-1)
    c: Radius(g5) = 3
    c: DistanceY(g0,g2) = 16
    c: DistanceX(g3,g1) = 16
FEATURE [PartDesign::Plane] DatumPlane008
  AttachmentSupport = -> [Sketch066]
  Length = 60
  MapMode = 7
  Placement = pos=(8,-5,0) rot=(1,0,0;1.5708rad)
  ResizeMode = 0
  Width = 60
FEATURE [PartDesign::Pad] Pad042  label="PadButtonCapPlusBase004"
  Direction = (0,0,1)
  Length = 4.59
  Length2 = 10
  Profile = -> Sketch066
  ReferenceAxis = -> Sketch066 [N_Axis]
  Refine = true
  SideType = 0
  Suppressed = false
  Type = 0
  Type2 = 0
  expr: Length = <<VarSetButtonDimensions004>>.button_cap_height + <<VarSetButtonDimensions004>>.Base_button_slide_depth + <<VarSetButtonDimensions004>>.Base_base_thickness
FEATURE [PartDesign::Thickness] Thickness005  label="ThicknessCapWall004"
  Base = -> Pad042 [Face9]
  BaseFeature = -> Pad042
  Intersection = false
  Join = 0
  Mode = 0
  Refine = true
  Reversed = true
  SupportTransform = false
  Suppressed = false
  Value = 1.5
  expr: Value = <<VarSetButtonDimensions004>>.button_cap_wall_thickness
FEATURE [Sketcher::SketchObject] Sketch067  label="SketchButtonSkirt004"
  ArcFitTolerance = 1e-06
  AttachmentSupport = -> [YZ_Plane026]
  ExternalGeometry = -> [Thickness005]
  ExternalTypes = [0]
  FullyConstrained = true
  MakeInternals = false
  MapMode = 5
  Placement = pos=(0,0,0) rot=(0.57735,0.57735,0.57735;2.0944rad)
  sketch-geometry (4):
    g0: LineSegment StartX=8 StartY=0 StartZ=0 EndX=8 EndY=2.5 EndZ=0
    g1: LineSegment StartX=8 StartY=2.5 StartZ=0 EndX=9 EndY=2.5 EndZ=0
    g2: LineSegment StartX=8 StartY=0 StartZ=0 EndX=9 EndY=0 EndZ=0
    g3: LineSegment StartX=9 StartY=2.5 StartZ=0 EndX=9 EndY=0 EndZ=0
  constraints (11):
    c: Coincident(g0,g-3)
    c: PointOnObject(g0,g-3)
    c: DistanceY(g0,g0) = 2.5
    c: Coincident(g1,g0)
    c: Horizontal(g1)
    c: Coincident(g2,g0)
    c: PointOnObject(g2,g-1)
    c: Coincident(g3,g1)
    c: Coincident(g3,g2)
    c: Vertical(g3)
    c: DistanceX(g1,g1) = 1
FEATURE [PartDesign::AdditivePipe] AdditivePipe004  label="AdditivePipeButtonSkirt004"
  AuxiliaryCurvilinear = true
  AuxiliarySpineTangent = false
  BaseFeature = -> Thickness005
  Binormal = (0,0,0)
  Mode = 0
  Profile = -> Sketch067
  Refine = true
  Spine = -> Thickness005 [Edge15,Edge18,Edge21,Edge23,Edge3,Edge6,Edge9,Edge12]
  SpineTangent = false
  Suppressed = false
  Transformation = 0
  Transition = 0
FEATURE [PartDesign::Pad] Pad043  label="PadButtonBottomContact004"
  BaseFeature = -> AdditivePipe004
  Direction = (0,0,-1)
  Length = 10
  Length2 = 10
  Profile = -> AdditivePipe004 [Face28]
  Refine = true
  SideType = 0
  Suppressed = false
  Type = 3
  Type2 = 0
  UpToFace = -> AdditivePipe004 [Face19]
FEATURE [PartDesign::Pocket] Pocket023  label="PocketBaseShorten004"
  BaseFeature = -> Pad043
  Direction = (0,0,1)
  Length = 0.2
  Length2 = 5
  Profile = -> Pad043 [Face19]
  Refine = true
  SideType = 0
  Suppressed = false
  Type = 0
  Type2 = 0
FEATURE [App::VarSet] VarSet006  label="VarSetButtonDimensions004"
  Base_base_thickness = 1.5
  Base_button_height = 16
  Base_button_radius = 3
  Base_button_slide_depth = 0.09
  Base_button_width = 16
  button_cap_height = 3
  button_cap_wall_thickness = 1.5
  button_snap_thickness = 0.5
  button_tab_depth = 1
  tolerance = 0.4
FEATURE [Sketcher::SketchObject] Sketch069  label="SketchButtonCapBase005"
  ArcFitTolerance = 1e-06
  AttachmentSupport = -> [XY_Plane027]
  ExternalTypes = [0]
  FullyConstrained = true
  MakeInternals = false
  MapMode = 5
  expr: Constraints[19] = <<VarSetButtonDimensions005>>.Base_button_radius
  expr: Constraints[20] = <<VarSetButtonDimensions005>>.Base_button_height
  expr: Constraints[21] = <<VarSetButtonDimensions005>>.Base_button_width
  sketch-geometry (10):
    g0: LineSegment StartX=-5 StartY=-8 StartZ=0 EndX=5 EndY=-8 EndZ=0
    g1: LineSegment StartX=8 StartY=-5 StartZ=0 EndX=8 EndY=5 EndZ=0
    g2: LineSegment StartX=5 StartY=8 StartZ=0 EndX=-5 EndY=8 EndZ=0
    g3: LineSegment StartX=-8 StartY=5 StartZ=0 EndX=-8 EndY=-5 EndZ=0
    g4: ArcOfCircle CenterX=-5 CenterY=-5 CenterZ=0 NormalX=0 NormalY=0 NormalZ=1 AngleXU=0 Radius=3 StartAngle=3.14159 EndAngle=4.71239
    g5: ArcOfCircle CenterX=5 CenterY=-5 CenterZ=0 NormalX=0 NormalY=0 NormalZ=1 AngleXU=0 Radius=3 StartAngle=4.71239 EndAngle=6.28319
    g6: ArcOfCircle CenterX=5 CenterY=5 CenterZ=0 NormalX=0 NormalY=0 NormalZ=1 AngleXU=0 Radius=3 StartAngle=1e-16 EndAngle=1.5708
    g7: ArcOfCircle CenterX=-5 CenterY=5 CenterZ=0 NormalX=0 NormalY=0 NormalZ=1 AngleXU=0 Radius=3 StartAngle=1.5708 EndAngle=3.14159
    g8: GeomPoint [constr] X=8 Y=8 Z=0
    g9: GeomPoint [constr] X=0 Y=0 Z=0
  constraints (22):
    c: Tangent(g0,g4) = -1.5708
    c: Tangent(g0,g5) = -1.5708
    c: Tangent(g1,g5) = -1.5708
    c: Tangent(g1,g6) = -1.5708
    c: Tangent(g2,g6) = -1.5708
    c: Tangent(g2,g7) = -1.5708
    c: Tangent(g3,g7) = -1.5708
    c: Tangent(g3,g4) = -1.5708
    c: Horizontal(g0)
    c: Horizontal(g2)
    c: Vertical(g1)
    c: Vertical(g3)
    c: Equal(g4,g5)
    c: Equal(g5,g6)
    c: Equal(g6,g7)
    c: Symmetric(g2,g0,g9)
    c: PointOnObject(g8,g1)
    c: PointOnObject(g8,g2)
    c: Coincident(g9,g-1)
    c: Radius(g5) = 3
    c: DistanceY(g0,g2) = 16
    c: DistanceX(g3,g1) = 16
FEATURE [PartDesign::Plane] DatumPlane009
  AttachmentSupport = -> [Sketch069]
  Length = 60
  MapMode = 7
  Placement = pos=(8,-5,0) rot=(1,0,0;1.5708rad)
  ResizeMode = 0
  Width = 60
FEATURE [PartDesign::Pad] Pad044  label="PadButtonCapPlusBase005"
  Direction = (0,0,1)
  Length = 4.59
  Length2 = 10
  Profile = -> Sketch069
  ReferenceAxis = -> Sketch069 [N_Axis]
  Refine = true
  SideType = 0
  Suppressed = false
  Type = 0
  Type2 = 0
  expr: Length = <<VarSetButtonDimensions005>>.button_cap_height + <<VarSetButtonDimensions005>>.Base_button_slide_depth + <<VarSetButtonDimensions005>>.Base_base_thickness
FEATURE [PartDesign::Thickness] Thickness006  label="ThicknessCapWall005"
  Base = -> Pad044 [Face9]
  BaseFeature = -> Pad044
  Intersection = false
  Join = 0
  Mode = 0
  Refine = true
  Reversed = true
  SupportTransform = false
  Suppressed = false
  Value = 1.5
  expr: Value = <<VarSetButtonDimensions005>>.button_cap_wall_thickness
FEATURE [Sketcher::SketchObject] Sketch070  label="SketchButtonSkirt005"
  ArcFitTolerance = 1e-06
  AttachmentSupport = -> [YZ_Plane027]
  ExternalGeometry = -> [Thickness006]
  ExternalTypes = [0]
  FullyConstrained = true
  MakeInternals = false
  MapMode = 5
  Placement = pos=(0,0,0) rot=(0.57735,0.57735,0.57735;2.0944rad)
  sketch-geometry (4):
    g0: LineSegment StartX=8 StartY=0 StartZ=0 EndX=8 EndY=2.5 EndZ=0
    g1: LineSegment StartX=8 StartY=2.5 StartZ=0 EndX=9 EndY=2.5 EndZ=0
    g2: LineSegment StartX=8 StartY=0 StartZ=0 EndX=9 EndY=0 EndZ=0
    g3: LineSegment StartX=9 StartY=2.5 StartZ=0 EndX=9 EndY=0 EndZ=0
  constraints (11):
    c: Coincident(g0,g-3)
    c: PointOnObject(g0,g-3)
    c: DistanceY(g0,g0) = 2.5
    c: Coincident(g1,g0)
    c: Horizontal(g1)
    c: Coincident(g2,g0)
    c: PointOnObject(g2,g-1)
    c: Coincident(g3,g1)
    c: Coincident(g3,g2)
    c: Vertical(g3)
    c: DistanceX(g1,g1) = 1
FEATURE [PartDesign::AdditivePipe] AdditivePipe005  label="AdditivePipeButtonSkirt005"
  AuxiliaryCurvilinear = true
  AuxiliarySpineTangent = false
  BaseFeature = -> Thickness006
  Binormal = (0,0,0)
  Mode = 0
  Profile = -> Sketch070
  Refine = true
  Spine = -> Thickness006 [Edge15,Edge18,Edge21,Edge23,Edge3,Edge6,Edge9,Edge12]
  SpineTangent = false
  Suppressed = false
  Transformation = 0
  Transition = 0
FEATURE [PartDesign::Pad] Pad045  label="PadButtonBottomContact005"
  BaseFeature = -> AdditivePipe005
  Direction = (0,0,-1)
  Length = 10
  Length2 = 10
  Profile = -> AdditivePipe005 [Face28]
  Refine = true
  SideType = 0
  Suppressed = false
  Type = 3
  Type2 = 0
  UpToFace = -> AdditivePipe005 [Face19]
FEATURE [PartDesign::Pocket] Pocket025  label="PocketBaseShorten005"
  BaseFeature = -> Pad045
  Direction = (0,0,1)
  Length = 0.2
  Length2 = 5
  Profile = -> Pad045 [Face19]
  Refine = true
  SideType = 0
  Suppressed = false
  Type = 0
  Type2 = 0
FEATURE [App::VarSet] VarSet007  label="VarSetButtonDimensions005"
  Base_base_thickness = 1.5
  Base_button_height = 16
  Base_button_radius = 3
  Base_button_slide_depth = 0.09
  Base_button_width = 16
  button_cap_height = 3
  button_cap_wall_thickness = 1.5
  button_snap_thickness = 0.5
  button_tab_depth = 1
  tolerance = 0.4
FEATURE [Sketcher::SketchObject] Sketch071  label="SketchTrailerIcon"
  ArcFitTolerance = 1e-06
  AttachmentOffset = pos=(24.5,12,0) rot=(1,0,0;3.14159rad)
  AttachmentSupport = -> [Pocket025]
  ExternalTypes = [0]
  FullyConstrained = false
  MakeInternals = false
  MapMode = 5
  Placement = pos=(24.5,12,4.59) rot=(1,0,0;3.14159rad)
  sketch-geometry (35):
    g0: BSplineCurve PolesCount=4 KnotsCount=2 Degree=3 IsPeriodic=0
    g1: BSplineCurve PolesCount=2 KnotsCount=2 Degree=1 IsPeriodic=0
    g2: BSplineCurve PolesCount=4 KnotsCount=2 Degree=3 IsPeriodic=0
    g3: BSplineCurve PolesCount=2 KnotsCount=2 Degree=1 IsPeriodic=0
    g4: BSplineCurve PolesCount=2 KnotsCount=2 Degree=1 IsPeriodic=0
    g5: BSplineCurve PolesCount=4 KnotsCount=2 Degree=3 IsPeriodic=0
    g6: BSplineCurve PolesCount=4 KnotsCount=2 Degree=3 IsPeriodic=0
    g7: BSplineCurve PolesCount=2 KnotsCount=2 Degree=1 IsPeriodic=0
    g8: BSplineCurve PolesCount=2 KnotsCount=2 Degree=1 IsPeriodic=0
    g9: BSplineCurve PolesCount=4 KnotsCount=2 Degree=3 IsPeriodic=0
    g10: BSplineCurve PolesCount=4 KnotsCount=2 Degree=3 IsPeriodic=0
    g11: BSplineCurve PolesCount=2 KnotsCount=2 Degree=1 IsPeriodic=0
    g12: BSplineCurve PolesCount=4 KnotsCount=2 Degree=3 IsPeriodic=0
    g13: BSplineCurve PolesCount=2 KnotsCount=2 Degree=1 IsPeriodic=0
    g14: BSplineCurve PolesCount=2 KnotsCount=2 Degree=1 IsPeriodic=0
    g15: BSplineCurve PolesCount=2 KnotsCount=2 Degree=1 IsPeriodic=0
    g16: BSplineCurve PolesCount=2 KnotsCount=2 Degree=1 IsPeriodic=0
    g17: BSplineCurve PolesCount=4 KnotsCount=2 Degree=3 IsPeriodic=0
    g18: BSplineCurve PolesCount=4 KnotsCount=2 Degree=3 IsPeriodic=0
    g19: BSplineCurve PolesCount=2 KnotsCount=2 Degree=1 IsPeriodic=0
    g20: BSplineCurve PolesCount=2 KnotsCount=2 Degree=1 IsPeriodic=0
    g21: BSplineCurve PolesCount=4 KnotsCount=2 Degree=3 IsPeriodic=0
    g22: BSplineCurve PolesCount=2 KnotsCount=2 Degree=1 IsPeriodic=0
    g23: BSplineCurve PolesCount=4 KnotsCount=2 Degree=3 IsPeriodic=0
    g24: BSplineCurve PolesCount=2 KnotsCount=2 Degree=1 IsPeriodic=0
    g25: BSplineCurve PolesCount=4 KnotsCount=2 Degree=3 IsPeriodic=0
    g26: BSplineCurve PolesCount=2 KnotsCount=2 Degree=1 IsPeriodic=0
    g27: BSplineCurve PolesCount=4 KnotsCount=2 Degree=3 IsPeriodic=0
    g28: BSplineCurve PolesCount=2 KnotsCount=2 Degree=1 IsPeriodic=0
    g29: BSplineCurve PolesCount=4 KnotsCount=2 Degree=3 IsPeriodic=0
    g30: BSplineCurve PolesCount=2 KnotsCount=2 Degree=1 IsPeriodic=0
    g31: BSplineCurve PolesCount=4 KnotsCount=2 Degree=3 IsPeriodic=0
    g32: BSplineCurve PolesCount=2 KnotsCount=2 Degree=1 IsPeriodic=0
    g33: BSplineCurve PolesCount=5 KnotsCount=4 Degree=2 IsPeriodic=0
    g34: BSplineCurve PolesCount=5 KnotsCount=4 Degree=2 IsPeriodic=0
  constraints (35):
    c: Coincident(g0,g1)
    c: Coincident(g1,g2)
    c: Coincident(g2,g3)
    c: Coincident(g3,g4)
    c: Coincident(g4,g5)
    c: Coincident(g5,g6)
    c: Coincident(g6,g7)
    c: Coincident(g7,g8)
    c: Coincident(g8,g9)
    c: Coincident(g9,g10)
    c: Coincident(g10,g11)
    c: Coincident(g11,g12)
    c: Coincident(g12,g13)
    c: Coincident(g13,g0)
    c: Coincident(g14,g15)
    c: Coincident(g15,g16)
    c: Coincident(g16,g17)
    c: Coincident(g17,g18)
    c: Coincident(g18,g19)
    c: Coincident(g19,g20)
    c: Coincident(g20,g21)
    c: Coincident(g21,g22)
    c: Coincident(g22,g23)
    c: Coincident(g23,g24)
    c: Coincident(g24,g14)
    c: Coincident(g25,g26)
    c: Coincident(g26,g27)
    c: Coincident(g27,g28)
    c: Coincident(g28,g29)
    c: Coincident(g29,g30)
    c: Coincident(g30,g31)
    c: Coincident(g31,g32)
    c: Coincident(g32,g25)
    c: Coincident(g33,g34)
    c: Coincident(g34,g33)
FEATURE [PartDesign::Pocket] Pocket026  label="PocketTrailerIcon"
  BaseFeature = -> Pocket025
  Direction = (0,1e-16,1)
  Length = 0.2
  Length2 = 5
  Profile = -> Sketch071
  ReferenceAxis = -> Sketch071 [N_Axis]
  Refine = true
  Reversed = true
  SideType = 0
  Suppressed = false
  Type = 0
  Type2 = 0
FEATURE [PartDesign::Body] Body009  label="BodyButtonCapTrailer"
  AllowCompound = false
  Group = -> [Sketch069,DatumPlane009,Pad044,Thickness006,Sketch070,AdditivePipe005,Pad045,Pocket025,Sketch071,Pocket026]
  Origin = -> Origin027
  Placement = pos=(14.24,-51.26,1.6) rot=(0,0,1;0rad)
  Tip = -> Pocket026
FEATURE [Sketcher::SketchObject] Sketch072  label="SketchButtonCapBase006"
  ArcFitTolerance = 1e-06
  AttachmentSupport = -> [XY_Plane028]
  ExternalTypes = [0]
  FullyConstrained = true
  MakeInternals = false
  MapMode = 5
  expr: Constraints[19] = <<VarSetButtonDimensions006>>.Base_button_radius
  expr: Constraints[20] = <<VarSetButtonDimensions006>>.Base_button_height
  expr: Constraints[21] = <<VarSetButtonDimensions006>>.Base_button_width
  sketch-geometry (10):
    g0: LineSegment StartX=-5 StartY=-8 StartZ=0 EndX=5 EndY=-8 EndZ=0
    g1: LineSegment StartX=8 StartY=-5 StartZ=0 EndX=8 EndY=5 EndZ=0
    g2: LineSegment StartX=5 StartY=8 StartZ=0 EndX=-5 EndY=8 EndZ=0
    g3: LineSegment StartX=-8 StartY=5 StartZ=0 EndX=-8 EndY=-5 EndZ=0
    g4: ArcOfCircle CenterX=-5 CenterY=-5 CenterZ=0 NormalX=0 NormalY=0 NormalZ=1 AngleXU=0 Radius=3 StartAngle=3.14159 EndAngle=4.71239
    g5: ArcOfCircle CenterX=5 CenterY=-5 CenterZ=0 NormalX=0 NormalY=0 NormalZ=1 AngleXU=0 Radius=3 StartAngle=4.71239 EndAngle=6.28319
    g6: ArcOfCircle CenterX=5 CenterY=5 CenterZ=0 NormalX=0 NormalY=0 NormalZ=1 AngleXU=0 Radius=3 StartAngle=1e-16 EndAngle=1.5708
    g7: ArcOfCircle CenterX=-5 CenterY=5 CenterZ=0 NormalX=0 NormalY=0 NormalZ=1 AngleXU=0 Radius=3 StartAngle=1.5708 EndAngle=3.14159
    g8: GeomPoint [constr] X=8 Y=8 Z=0
    g9: GeomPoint [constr] X=0 Y=0 Z=0
  constraints (22):
    c: Tangent(g0,g4) = -1.5708
    c: Tangent(g0,g5) = -1.5708
    c: Tangent(g1,g5) = -1.5708
    c: Tangent(g1,g6) = -1.5708
    c: Tangent(g2,g6) = -1.5708
    c: Tangent(g2,g7) = -1.5708
    c: Tangent(g3,g7) = -1.5708
    c: Tangent(g3,g4) = -1.5708
    c: Horizontal(g0)
    c: Horizontal(g2)
    c: Vertical(g1)
    c: Vertical(g3)
    c: Equal(g4,g5)
    c: Equal(g5,g6)
    c: Equal(g6,g7)
    c: Symmetric(g2,g0,g9)
    c: PointOnObject(g8,g1)
    c: PointOnObject(g8,g2)
    c: Coincident(g9,g-1)
    c: Radius(g5) = 3
    c: DistanceY(g0,g2) = 16
    c: DistanceX(g3,g1) = 16
FEATURE [PartDesign::Plane] DatumPlane010
  AttachmentSupport = -> [Sketch072]
  Length = 60
  MapMode = 7
  Placement = pos=(8,-5,0) rot=(1,0,0;1.5708rad)
  ResizeMode = 0
  Width = 60
FEATURE [PartDesign::Pad] Pad046  label="PadButtonCapPlusBase006"
  Direction = (0,0,1)
  Length = 4.59
  Length2 = 10
  Profile = -> Sketch072
  ReferenceAxis = -> Sketch072 [N_Axis]
  Refine = true
  SideType = 0
  Suppressed = false
  Type = 0
  Type2 = 0
  expr: Length = <<VarSetButtonDimensions006>>.button_cap_height + <<VarSetButtonDimensions006>>.Base_button_slide_depth + <<VarSetButtonDimensions006>>.Base_base_thickness
FEATURE [PartDesign::Thickness] Thickness007  label="ThicknessCapWall006"
  Base = -> Pad046 [Face9]
  BaseFeature = -> Pad046
  Intersection = false
  Join = 0
  Mode = 0
  Refine = true
  Reversed = true
  SupportTransform = false
  Suppressed = false
  Value = 1.5
  expr: Value = <<VarSetButtonDimensions006>>.button_cap_wall_thickness
FEATURE [Sketcher::SketchObject] Sketch073  label="SketchButtonSkirt006"
  ArcFitTolerance = 1e-06
  AttachmentSupport = -> [YZ_Plane028]
  ExternalGeometry = -> [Thickness007]
  ExternalTypes = [0]
  FullyConstrained = true
  MakeInternals = false
  MapMode = 5
  Placement = pos=(0,0,0) rot=(0.57735,0.57735,0.57735;2.0944rad)
  sketch-geometry (4):
    g0: LineSegment StartX=8 StartY=0 StartZ=0 EndX=8 EndY=2.5 EndZ=0
    g1: LineSegment StartX=8 StartY=2.5 StartZ=0 EndX=9 EndY=2.5 EndZ=0
    g2: LineSegment StartX=8 StartY=0 StartZ=0 EndX=9 EndY=0 EndZ=0
    g3: LineSegment StartX=9 StartY=2.5 StartZ=0 EndX=9 EndY=0 EndZ=0
  constraints (11):
    c: Coincident(g0,g-3)
    c: PointOnObject(g0,g-3)
    c: DistanceY(g0,g0) = 2.5
    c: Coincident(g1,g0)
    c: Horizontal(g1)
    c: Coincident(g2,g0)
    c: PointOnObject(g2,g-1)
    c: Coincident(g3,g1)
    c: Coincident(g3,g2)
    c: Vertical(g3)
    c: DistanceX(g1,g1) = 1
FEATURE [PartDesign::AdditivePipe] AdditivePipe006  label="AdditivePipeButtonSkirt006"
  AuxiliaryCurvilinear = true
  AuxiliarySpineTangent = false
  BaseFeature = -> Thickness007
  Binormal = (0,0,0)
  Mode = 0
  Profile = -> Sketch073
  Refine = true
  Spine = -> Thickness007 [Edge15,Edge18,Edge21,Edge23,Edge3,Edge6,Edge9,Edge12]
  SpineTangent = false
  Suppressed = false
  Transformation = 0
  Transition = 0
FEATURE [PartDesign::Pad] Pad047  label="PadButtonBottomContact006"
  BaseFeature = -> AdditivePipe006
  Direction = (0,0,-1)
  Length = 10
  Length2 = 10
  Profile = -> AdditivePipe006 [Face28]
  Refine = true
  SideType = 0
  Suppressed = false
  Type = 3
  Type2 = 0
  UpToFace = -> AdditivePipe006 [Face19]
FEATURE [PartDesign::Pocket] Pocket027  label="PocketBaseShorten006"
  BaseFeature = -> Pad047
  Direction = (0,0,1)
  Length = 0.2
  Length2 = 5
  Profile = -> Pad047 [Face19]
  Refine = true
  SideType = 0
  Suppressed = false
  Type = 0
  Type2 = 0
FEATURE [App::VarSet] VarSet008  label="VarSetButtonDimensions006"
  Base_base_thickness = 1.5
  Base_button_height = 16
  Base_button_radius = 3
  Base_button_slide_depth = 0.09
  Base_button_width = 16
  button_cap_height = 3
  button_cap_wall_thickness = 1.5
  button_snap_thickness = 0.5
  button_tab_depth = 1
  tolerance = 0.4
FEATURE [Sketcher::SketchObject] Sketch074  label="SketchIconDoor"
  ArcFitTolerance = 1e-06
  AttachmentOffset = pos=(12.5,132,0) rot=(1,0,0;3.14159rad)
  AttachmentSupport = -> [Pocket027]
  ExternalTypes = [0]
  FullyConstrained = false
  MakeInternals = false
  MapMode = 5
  Placement = pos=(12.5,132,4.59) rot=(1,0,0;3.14159rad)
  sketch-geometry (16):
    g0: BSplineCurve PolesCount=4 KnotsCount=2 Degree=3 IsPeriodic=0
    g1: BSplineCurve PolesCount=2 KnotsCount=2 Degree=1 IsPeriodic=0
    g2: BSplineCurve PolesCount=4 KnotsCount=2 Degree=3 IsPeriodic=0
    g3: BSplineCurve PolesCount=2 KnotsCount=2 Degree=1 IsPeriodic=0
    g4: BSplineCurve PolesCount=2 KnotsCount=2 Degree=1 IsPeriodic=0
    g5: BSplineCurve PolesCount=4 KnotsCount=2 Degree=3 IsPeriodic=0
    g6: BSplineCurve PolesCount=4 KnotsCount=2 Degree=3 IsPeriodic=0
    g7: BSplineCurve PolesCount=2 KnotsCount=2 Degree=1 IsPeriodic=0
    g8: BSplineCurve PolesCount=2 KnotsCount=2 Degree=1 IsPeriodic=0
    g9: BSplineCurve PolesCount=2 KnotsCount=2 Degree=1 IsPeriodic=0
    g10: BSplineCurve PolesCount=4 KnotsCount=2 Degree=3 IsPeriodic=0
    g11: BSplineCurve PolesCount=4 KnotsCount=2 Degree=3 IsPeriodic=0
    g12: BSplineCurve PolesCount=2 KnotsCount=2 Degree=1 IsPeriodic=0
    g13: BSplineCurve PolesCount=2 KnotsCount=2 Degree=1 IsPeriodic=0
    g14: BSplineCurve PolesCount=5 KnotsCount=4 Degree=2 IsPeriodic=0
    g15: BSplineCurve PolesCount=5 KnotsCount=4 Degree=2 IsPeriodic=0
  constraints (16):
    c: Coincident(g0,g1)
    c: Coincident(g1,g2)
    c: Coincident(g2,g3)
    c: Coincident(g3,g4)
    c: Coincident(g4,g5)
    c: Coincident(g5,g6)
    c: Coincident(g6,g7)
    c: Coincident(g7,g8)
    c: Coincident(g8,g9)
    c: Coincident(g9,g10)
    c: Coincident(g10,g11)
    c: Coincident(g11,g12)
    c: Coincident(g12,g13)
    c: Coincident(g13,g0)
    c: Coincident(g14,g15)
    c: Coincident(g15,g14)
FEATURE [PartDesign::Pocket] Pocket028
  BaseFeature = -> Pocket027
  Direction = (0,1e-16,1)
  Length = 0.2
  Length2 = 5
  Profile = -> Sketch074
  ReferenceAxis = -> Sketch074 [N_Axis]
  Refine = true
  Reversed = true
  SideType = 0
  Suppressed = false
  Type = 0
  Type2 = 0
FEATURE [PartDesign::Body] Body010  label="BodyButtonCapEntry"
  AllowCompound = false
  Group = -> [Sketch072,DatumPlane010,Pad046,Thickness007,Sketch073,AdditivePipe006,Pad047,Pocket027,Sketch074,Pocket028]
  Origin = -> Origin028
  Placement = pos=(41.98,-51.31,1.6) rot=(0,0,1;0rad)
  Tip = -> Pocket028
FEATURE [Sketcher::SketchObject] Sketch075  label="SketchButtonCapBase007"
  ArcFitTolerance = 1e-06
  AttachmentSupport = -> [XY_Plane029]
  ExternalTypes = [0]
  FullyConstrained = true
  MakeInternals = false
  MapMode = 5
  expr: Constraints[19] = <<VarSetButtonDimensions007>>.Base_button_radius
  expr: Constraints[20] = <<VarSetButtonDimensions007>>.Base_button_height
  expr: Constraints[21] = <<VarSetButtonDimensions007>>.Base_button_width
  sketch-geometry (10):
    g0: LineSegment StartX=-5 StartY=-8 StartZ=0 EndX=5 EndY=-8 EndZ=0
    g1: LineSegment StartX=8 StartY=-5 StartZ=0 EndX=8 EndY=5 EndZ=0
    g2: LineSegment StartX=5 StartY=8 StartZ=0 EndX=-5 EndY=8 EndZ=0
    g3: LineSegment StartX=-8 StartY=5 StartZ=0 EndX=-8 EndY=-5 EndZ=0
    g4: ArcOfCircle CenterX=-5 CenterY=-5 CenterZ=0 NormalX=0 NormalY=0 NormalZ=1 AngleXU=0 Radius=3 StartAngle=3.14159 EndAngle=4.71239
    g5: ArcOfCircle CenterX=5 CenterY=-5 CenterZ=0 NormalX=0 NormalY=0 NormalZ=1 AngleXU=0 Radius=3 StartAngle=4.71239 EndAngle=6.28319
    g6: ArcOfCircle CenterX=5 CenterY=5 CenterZ=0 NormalX=0 NormalY=0 NormalZ=1 AngleXU=0 Radius=3 StartAngle=1e-16 EndAngle=1.5708
    g7: ArcOfCircle CenterX=-5 CenterY=5 CenterZ=0 NormalX=0 NormalY=0 NormalZ=1 AngleXU=0 Radius=3 StartAngle=1.5708 EndAngle=3.14159
    g8: GeomPoint [constr] X=8 Y=8 Z=0
    g9: GeomPoint [constr] X=0 Y=0 Z=0
  constraints (22):
    c: Tangent(g0,g4) = -1.5708
    c: Tangent(g0,g5) = -1.5708
    c: Tangent(g1,g5) = -1.5708
    c: Tangent(g1,g6) = -1.5708
    c: Tangent(g2,g6) = -1.5708
    c: Tangent(g2,g7) = -1.5708
    c: Tangent(g3,g7) = -1.5708
    c: Tangent(g3,g4) = -1.5708
    c: Horizontal(g0)
    c: Horizontal(g2)
    c: Vertical(g1)
    c: Vertical(g3)
    c: Equal(g4,g5)
    c: Equal(g5,g6)
    c: Equal(g6,g7)
    c: Symmetric(g2,g0,g9)
    c: PointOnObject(g8,g1)
    c: PointOnObject(g8,g2)
    c: Coincident(g9,g-1)
    c: Radius(g5) = 3
    c: DistanceY(g0,g2) = 16
    c: DistanceX(g3,g1) = 16
FEATURE [PartDesign::Plane] DatumPlane011
  AttachmentSupport = -> [Sketch075]
  Length = 60
  MapMode = 7
  Placement = pos=(8,-5,0) rot=(1,0,0;1.5708rad)
  ResizeMode = 0
  Width = 60
FEATURE [PartDesign::Pad] Pad048  label="PadButtonCapPlusBase007"
  Direction = (0,0,1)
  Length = 4.59
  Length2 = 10
  Profile = -> Sketch075
  ReferenceAxis = -> Sketch075 [N_Axis]
  Refine = true
  SideType = 0
  Suppressed = false
  Type = 0
  Type2 = 0
  expr: Length = <<VarSetButtonDimensions007>>.button_cap_height + <<VarSetButtonDimensions007>>.Base_button_slide_depth + <<VarSetButtonDimensions007>>.Base_base_thickness
FEATURE [PartDesign::Thickness] Thickness008  label="ThicknessCapWall007"
  Base = -> Pad048 [Face9]
  BaseFeature = -> Pad048
  Intersection = false
  Join = 0
  Mode = 0
  Refine = true
  Reversed = true
  SupportTransform = false
  Suppressed = false
  Value = 1.5
  expr: Value = <<VarSetButtonDimensions007>>.button_cap_wall_thickness
FEATURE [Sketcher::SketchObject] Sketch076  label="SketchButtonSkirt007"
  ArcFitTolerance = 1e-06
  AttachmentSupport = -> [YZ_Plane029]
  ExternalGeometry = -> [Thickness008]
  ExternalTypes = [0]
  FullyConstrained = true
  MakeInternals = false
  MapMode = 5
  Placement = pos=(0,0,0) rot=(0.57735,0.57735,0.57735;2.0944rad)
  sketch-geometry (4):
    g0: LineSegment StartX=8 StartY=0 StartZ=0 EndX=8 EndY=2.5 EndZ=0
    g1: LineSegment StartX=8 StartY=2.5 StartZ=0 EndX=9 EndY=2.5 EndZ=0
    g2: LineSegment StartX=8 StartY=0 StartZ=0 EndX=9 EndY=0 EndZ=0
    g3: LineSegment StartX=9 StartY=2.5 StartZ=0 EndX=9 EndY=0 EndZ=0
  constraints (11):
    c: Coincident(g0,g-3)
    c: PointOnObject(g0,g-3)
    c: DistanceY(g0,g0) = 2.5
    c: Coincident(g1,g0)
    c: Horizontal(g1)
    c: Coincident(g2,g0)
    c: PointOnObject(g2,g-1)
    c: Coincident(g3,g1)
    c: Coincident(g3,g2)
    c: Vertical(g3)
    c: DistanceX(g1,g1) = 1
FEATURE [PartDesign::AdditivePipe] AdditivePipe007  label="AdditivePipeButtonSkirt007"
  AuxiliaryCurvilinear = true
  AuxiliarySpineTangent = false
  BaseFeature = -> Thickness008
  Binormal = (0,0,0)
  Mode = 0
  Profile = -> Sketch076
  Refine = true
  Spine = -> Thickness008 [Edge15,Edge18,Edge21,Edge23,Edge3,Edge6,Edge9,Edge12]
  SpineTangent = false
  Suppressed = false
  Transformation = 0
  Transition = 0
FEATURE [PartDesign::Pad] Pad049  label="PadButtonBottomContact007"
  BaseFeature = -> AdditivePipe007
  Direction = (0,0,-1)
  Length = 10
  Length2 = 10
  Profile = -> AdditivePipe007 [Face28]
  Refine = true
  SideType = 0
  Suppressed = false
  Type = 3
  Type2 = 0
  UpToFace = -> AdditivePipe007 [Face19]
FEATURE [PartDesign::Pocket] Pocket029  label="PocketBaseShorten007"
  BaseFeature = -> Pad049
  Direction = (0,0,1)
  Length = 0.2
  Length2 = 5
  Profile = -> Pad049 [Face19]
  Refine = true
  SideType = 0
  Suppressed = false
  Type = 0
  Type2 = 0
FEATURE [App::VarSet] VarSet009  label="VarSetButtonDimensions007"
  Base_base_thickness = 1.5
  Base_button_height = 16
  Base_button_radius = 3
  Base_button_slide_depth = 0.09
  Base_button_width = 16
  button_cap_height = 3
  button_cap_wall_thickness = 1.5
  button_snap_thickness = 0.5
  button_tab_depth = 1
  tolerance = 0.4
FEATURE [Sketcher::SketchObject] Sketch077  label="SketchIconUnderCabinet"
  ArcFitTolerance = 1e-06
  AttachmentOffset = pos=(-22.2,-37,0) rot=(1,0,0;3.14159rad)
  AttachmentSupport = -> [Pocket011]
  ExternalTypes = [0]
  FullyConstrained = false
  MakeInternals = false
  MapMode = 5
  Placement = pos=(-22.2,-37,4.59) rot=(1,0,0;3.14159rad)
  sketch-geometry (33):
    g0: BSplineCurve PolesCount=2 KnotsCount=2 Degree=1 IsPeriodic=0
    g1: BSplineCurve PolesCount=4 KnotsCount=2 Degree=3 IsPeriodic=0
    g2: BSplineCurve PolesCount=4 KnotsCount=2 Degree=3 IsPeriodic=0
    g3: BSplineCurve PolesCount=2 KnotsCount=2 Degree=1 IsPeriodic=0
    g4: BSplineCurve PolesCount=4 KnotsCount=2 Degree=3 IsPeriodic=0
    g5: BSplineCurve PolesCount=4 KnotsCount=2 Degree=3 IsPeriodic=0
    g6: BSplineCurve PolesCount=4 KnotsCount=2 Degree=3 IsPeriodic=0
    g7: BSplineCurve PolesCount=2 KnotsCount=2 Degree=1 IsPeriodic=0
    g8: BSplineCurve PolesCount=4 KnotsCount=2 Degree=3 IsPeriodic=0
    g9: BSplineCurve PolesCount=2 KnotsCount=2 Degree=1 IsPeriodic=0
    g10: BSplineCurve PolesCount=2 KnotsCount=2 Degree=1 IsPeriodic=0
    g11: BSplineCurve PolesCount=2 KnotsCount=2 Degree=1 IsPeriodic=0
    g12: BSplineCurve PolesCount=4 KnotsCount=2 Degree=3 IsPeriodic=0
    g13: BSplineCurve PolesCount=2 KnotsCount=2 Degree=1 IsPeriodic=0
    g14: BSplineCurve PolesCount=4 KnotsCount=2 Degree=3 IsPeriodic=0
    g15: BSplineCurve PolesCount=2 KnotsCount=2 Degree=1 IsPeriodic=0
    g16: BSplineCurve PolesCount=4 KnotsCount=2 Degree=3 IsPeriodic=0
    g17: BSplineCurve PolesCount=2 KnotsCount=2 Degree=1 IsPeriodic=0
    g18: BSplineCurve PolesCount=4 KnotsCount=2 Degree=3 IsPeriodic=0
    g19: BSplineCurve PolesCount=2 KnotsCount=2 Degree=1 IsPeriodic=0
    g20: BSplineCurve PolesCount=2 KnotsCount=2 Degree=1 IsPeriodic=0
    g21: BSplineCurve PolesCount=4 KnotsCount=2 Degree=3 IsPeriodic=0
    g22: BSplineCurve PolesCount=2 KnotsCount=2 Degree=1 IsPeriodic=0
    g23: BSplineCurve PolesCount=4 KnotsCount=2 Degree=3 IsPeriodic=0
    g24: BSplineCurve PolesCount=4 KnotsCount=2 Degree=3 IsPeriodic=0
    g25: BSplineCurve PolesCount=2 KnotsCount=2 Degree=1 IsPeriodic=0
    g26: BSplineCurve PolesCount=4 KnotsCount=2 Degree=3 IsPeriodic=0
    g27: BSplineCurve PolesCount=4 KnotsCount=2 Degree=3 IsPeriodic=0
    g28: BSplineCurve PolesCount=4 KnotsCount=2 Degree=3 IsPeriodic=0
    g29: BSplineCurve PolesCount=2 KnotsCount=2 Degree=1 IsPeriodic=0
    g30: BSplineCurve PolesCount=4 KnotsCount=2 Degree=3 IsPeriodic=0
    g31: BSplineCurve PolesCount=4 KnotsCount=2 Degree=3 IsPeriodic=0
    g32: BSplineCurve PolesCount=2 KnotsCount=2 Degree=1 IsPeriodic=0
  constraints (33):
    c: Coincident(g0,g1)
    c: Coincident(g1,g2)
    c: Coincident(g2,g3)
    c: Coincident(g3,g4)
    c: Coincident(g4,g5)
    c: Coincident(g5,g0)
    c: Coincident(g6,g7)
    c: Coincident(g7,g8)
    c: Coincident(g8,g9)
    c: Coincident(g9,g10)
    c: Coincident(g10,g11)
    c: Coincident(g11,g6)
    c: Coincident(g12,g13)
    c: Coincident(g13,g14)
    c: Coincident(g14,g15)
    c: Coincident(g15,g16)
    c: Coincident(g16,g17)
    c: Coincident(g17,g18)
    c: Coincident(g18,g19)
    c: Coincident(g19,g20)
    c: Coincident(g20,g12)
    c: Coincident(g21,g22)
    c: Coincident(g22,g23)
    c: Coincident(g23,g24)
    c: Coincident(g24,g25)
    c: Coincident(g25,g26)
    c: Coincident(g26,g21)
    c: Coincident(g27,g28)
    c: Coincident(g28,g29)
    c: Coincident(g29,g30)
    c: Coincident(g30,g31)
    c: Coincident(g31,g32)
    c: Coincident(g32,g27)
FEATURE [PartDesign::Pocket] Pocket030  label="PocketIconUnderCabinet"
  BaseFeature = -> Pocket029
  Direction = (0,1e-16,1)
  Length = 0.2
  Length2 = 5
  Profile = -> Sketch077
  ReferenceAxis = -> Sketch077 [N_Axis]
  Refine = true
  Reversed = true
  SideType = 0
  Suppressed = false
  Type = 0
  Type2 = 0
FEATURE [PartDesign::Body] Body011  label="BodyButtonCapUnderCabinet"
  AllowCompound = false
  Group = -> [Sketch075,DatumPlane011,Pad048,Thickness008,Sketch076,AdditivePipe007,Pad049,Pocket029,Sketch077,Pocket030]
  Origin = -> Origin029
  Placement = pos=(69.97,-51.36,1.6) rot=(0,0,1;0rad)
  Tip = -> Pocket030
FEATURE [Sketcher::SketchObject] Sketch078  label="SketchButtonCapBase008"
  ArcFitTolerance = 1e-06
  AttachmentSupport = -> [XY_Plane030]
  ExternalTypes = [0]
  FullyConstrained = true
  MakeInternals = false
  MapMode = 5
  expr: Constraints[19] = <<VarSetButtonDimensions008>>.Base_button_radius
  expr: Constraints[20] = <<VarSetButtonDimensions008>>.Base_button_height
  expr: Constraints[21] = <<VarSetButtonDimensions008>>.Base_button_width
  sketch-geometry (10):
    g0: LineSegment StartX=-5 StartY=-8 StartZ=0 EndX=5 EndY=-8 EndZ=0
    g1: LineSegment StartX=8 StartY=-5 StartZ=0 EndX=8 EndY=5 EndZ=0
    g2: LineSegment StartX=5 StartY=8 StartZ=0 EndX=-5 EndY=8 EndZ=0
    g3: LineSegment StartX=-8 StartY=5 StartZ=0 EndX=-8 EndY=-5 EndZ=0
    g4: ArcOfCircle CenterX=-5 CenterY=-5 CenterZ=0 NormalX=0 NormalY=0 NormalZ=1 AngleXU=0 Radius=3 StartAngle=3.14159 EndAngle=4.71239
    g5: ArcOfCircle CenterX=5 CenterY=-5 CenterZ=0 NormalX=0 NormalY=0 NormalZ=1 AngleXU=0 Radius=3 StartAngle=4.71239 EndAngle=6.28319
    g6: ArcOfCircle CenterX=5 CenterY=5 CenterZ=0 NormalX=0 NormalY=0 NormalZ=1 AngleXU=0 Radius=3 StartAngle=1e-16 EndAngle=1.5708
    g7: ArcOfCircle CenterX=-5 CenterY=5 CenterZ=0 NormalX=0 NormalY=0 NormalZ=1 AngleXU=0 Radius=3 StartAngle=1.5708 EndAngle=3.14159
    g8: GeomPoint [constr] X=8 Y=8 Z=0
    g9: GeomPoint [constr] X=0 Y=0 Z=0
  constraints (22):
    c: Tangent(g0,g4) = -1.5708
    c: Tangent(g0,g5) = -1.5708
    c: Tangent(g1,g5) = -1.5708
    c: Tangent(g1,g6) = -1.5708
    c: Tangent(g2,g6) = -1.5708
    c: Tangent(g2,g7) = -1.5708
    c: Tangent(g3,g7) = -1.5708
    c: Tangent(g3,g4) = -1.5708
    c: Horizontal(g0)
    c: Horizontal(g2)
    c: Vertical(g1)
    c: Vertical(g3)
    c: Equal(g4,g5)
    c: Equal(g5,g6)
    c: Equal(g6,g7)
    c: Symmetric(g2,g0,g9)
    c: PointOnObject(g8,g1)
    c: PointOnObject(g8,g2)
    c: Coincident(g9,g-1)
    c: Radius(g5) = 3
    c: DistanceY(g0,g2) = 16
    c: DistanceX(g3,g1) = 16
FEATURE [PartDesign::Plane] DatumPlane012
  AttachmentSupport = -> [Sketch078]
  Length = 60
  MapMode = 7
  Placement = pos=(8,-5,0) rot=(1,0,0;1.5708rad)
  ResizeMode = 0
  Width = 60
FEATURE [PartDesign::Pad] Pad050  label="PadButtonCapPlusBase008"
  Direction = (0,0,1)
  Length = 4.59
  Length2 = 10
  Profile = -> Sketch078
  ReferenceAxis = -> Sketch078 [N_Axis]
  Refine = true
  SideType = 0
  Suppressed = false
  Type = 0
  Type2 = 0
  expr: Length = <<VarSetButtonDimensions008>>.button_cap_height + <<VarSetButtonDimensions008>>.Base_button_slide_depth + <<VarSetButtonDimensions008>>.Base_base_thickness
FEATURE [PartDesign::Thickness] Thickness009  label="ThicknessCapWall008"
  Base = -> Pad050 [Face9]
  BaseFeature = -> Pad050
  Intersection = false
  Join = 0
  Mode = 0
  Refine = true
  Reversed = true
  SupportTransform = false
  Suppressed = false
  Value = 1.5
  expr: Value = <<VarSetButtonDimensions008>>.button_cap_wall_thickness
FEATURE [Sketcher::SketchObject] Sketch079  label="SketchButtonSkirt008"
  ArcFitTolerance = 1e-06
  AttachmentSupport = -> [YZ_Plane030]
  ExternalGeometry = -> [Thickness009]
  ExternalTypes = [0]
  FullyConstrained = true
  MakeInternals = false
  MapMode = 5
  Placement = pos=(0,0,0) rot=(0.57735,0.57735,0.57735;2.0944rad)
  sketch-geometry (4):
    g0: LineSegment StartX=8 StartY=0 StartZ=0 EndX=8 EndY=2.5 EndZ=0
    g1: LineSegment StartX=8 StartY=2.5 StartZ=0 EndX=9 EndY=2.5 EndZ=0
    g2: LineSegment StartX=8 StartY=0 StartZ=0 EndX=9 EndY=0 EndZ=0
    g3: LineSegment StartX=9 StartY=2.5 StartZ=0 EndX=9 EndY=0 EndZ=0
  constraints (11):
    c: Coincident(g0,g-3)
    c: PointOnObject(g0,g-3)
    c: DistanceY(g0,g0) = 2.5
    c: Coincident(g1,g0)
    c: Horizontal(g1)
    c: Coincident(g2,g0)
    c: PointOnObject(g2,g-1)
    c: Coincident(g3,g1)
    c: Coincident(g3,g2)
    c: Vertical(g3)
    c: DistanceX(g1,g1) = 1
FEATURE [PartDesign::AdditivePipe] AdditivePipe008  label="AdditivePipeButtonSkirt008"
  AuxiliaryCurvilinear = true
  AuxiliarySpineTangent = false
  BaseFeature = -> Thickness009
  Binormal = (0,0,0)
  Mode = 0
  Profile = -> Sketch079
  Refine = true
  Spine = -> Thickness009 [Edge15,Edge18,Edge21,Edge23,Edge3,Edge6,Edge9,Edge12]
  SpineTangent = false
  Suppressed = false
  Transformation = 0
  Transition = 0
FEATURE [PartDesign::Pad] Pad051  label="PadButtonBottomContact008"
  BaseFeature = -> AdditivePipe008
  Direction = (0,0,-1)
  Length = 10
  Length2 = 10
  Profile = -> AdditivePipe008 [Face28]
  Refine = true
  SideType = 0
  Suppressed = false
  Type = 3
  Type2 = 0
  UpToFace = -> AdditivePipe008 [Face19]
FEATURE [PartDesign::Pocket] Pocket031  label="PocketBaseShorten008"
  BaseFeature = -> Pad051
  Direction = (0,0,1)
  Length = 0.2
  Length2 = 5
  Profile = -> Pad051 [Face19]
  Refine = true
  SideType = 0
  Suppressed = false
  Type = 0
  Type2 = 0
FEATURE [App::VarSet] VarSet010  label="VarSetButtonDimensions008"
  Base_base_thickness = 1.5
  Base_button_height = 16
  Base_button_radius = 3
  Base_button_slide_depth = 0.09
  Base_button_width = 16
  button_cap_height = 3
  button_cap_wall_thickness = 1.5
  button_snap_thickness = 0.5
  button_tab_depth = 1
  tolerance = 0.4
FEATURE [Sketcher::SketchObject] Sketch080  label="SketchPorchIcon"
  ArcFitTolerance = 1e-06
  AttachmentOffset = pos=(-25.5,9,0) rot=(0,0,1;0rad)
  AttachmentSupport = -> [Pocket011]
  ExternalTypes = [0]
  FullyConstrained = false
  MakeInternals = false
  MapMode = 5
  Placement = pos=(-25.5,9,4.59) rot=(0,0,1;0rad)
  sketch-geometry (27):
    g0: BSplineCurve PolesCount=2 KnotsCount=2 Degree=1 IsPeriodic=0
    g1: BSplineCurve PolesCount=4 KnotsCount=2 Degree=3 IsPeriodic=0
    g2: BSplineCurve PolesCount=4 KnotsCount=2 Degree=3 IsPeriodic=0
    g3: BSplineCurve PolesCount=2 KnotsCount=2 Degree=1 IsPeriodic=0
    g4: BSplineCurve PolesCount=4 KnotsCount=2 Degree=3 IsPeriodic=0
    g5: BSplineCurve PolesCount=2 KnotsCount=2 Degree=1 IsPeriodic=0
    g6: BSplineCurve PolesCount=4 KnotsCount=2 Degree=3 IsPeriodic=0
    g7: BSplineCurve PolesCount=2 KnotsCount=2 Degree=1 IsPeriodic=0
    g8: BSplineCurve PolesCount=4 KnotsCount=2 Degree=3 IsPeriodic=0
    g9: BSplineCurve PolesCount=4 KnotsCount=2 Degree=3 IsPeriodic=0
    g10: BSplineCurve PolesCount=2 KnotsCount=2 Degree=1 IsPeriodic=0
    g11: BSplineCurve PolesCount=2 KnotsCount=2 Degree=1 IsPeriodic=0
    g12: BSplineCurve PolesCount=4 KnotsCount=2 Degree=3 IsPeriodic=0
    g13: BSplineCurve PolesCount=2 KnotsCount=2 Degree=1 IsPeriodic=0
    g14: BSplineCurve PolesCount=4 KnotsCount=2 Degree=3 IsPeriodic=0
    g15: BSplineCurve PolesCount=2 KnotsCount=2 Degree=1 IsPeriodic=0
    g16: BSplineCurve PolesCount=2 KnotsCount=2 Degree=1 IsPeriodic=0
    g17: BSplineCurve PolesCount=2 KnotsCount=2 Degree=1 IsPeriodic=0
    g18: BSplineCurve PolesCount=2 KnotsCount=2 Degree=1 IsPeriodic=0
    g19: BSplineCurve PolesCount=2 KnotsCount=2 Degree=1 IsPeriodic=0
    g20: BSplineCurve PolesCount=2 KnotsCount=2 Degree=1 IsPeriodic=0
    g21: BSplineCurve PolesCount=2 KnotsCount=2 Degree=1 IsPeriodic=0
    g22: BSplineCurve PolesCount=2 KnotsCount=2 Degree=1 IsPeriodic=0
    g23: BSplineCurve PolesCount=4 KnotsCount=2 Degree=3 IsPeriodic=0
    g24: BSplineCurve PolesCount=4 KnotsCount=2 Degree=3 IsPeriodic=0
    g25: BSplineCurve PolesCount=2 KnotsCount=2 Degree=1 IsPeriodic=0
    g26: BSplineCurve PolesCount=2 KnotsCount=2 Degree=1 IsPeriodic=0
  constraints (27):
    c: Coincident(g0,g1)
    c: Coincident(g1,g2)
    c: Coincident(g2,g3)
    c: Coincident(g3,g4)
    c: Coincident(g4,g5)
    c: Coincident(g5,g6)
    c: Coincident(g6,g7)
    c: Coincident(g7,g8)
    c: Coincident(g8,g9)
    c: Coincident(g9,g0)
    c: Coincident(g10,g11)
    c: Coincident(g11,g12)
    c: Coincident(g12,g13)
    c: Coincident(g13,g14)
    c: Coincident(g14,g15)
    c: Coincident(g15,g16)
    c: Coincident(g16,g17)
    c: Coincident(g17,g18)
    c: Coincident(g18,g19)
    c: Coincident(g19,g20)
    c: Coincident(g20,g21)
    c: Coincident(g21,g10)
    c: Coincident(g22,g23)
    c: Coincident(g23,g24)
    c: Coincident(g24,g25)
    c: Coincident(g25,g26)
    c: Coincident(g26,g22)
FEATURE [PartDesign::Pocket] Pocket032
  BaseFeature = -> Pocket031
  Direction = (0,0,-1)
  Length = 0.2
  Length2 = 5
  Profile = -> Sketch080
  ReferenceAxis = -> Sketch080 [N_Axis]
  Refine = true
  SideType = 0
  Suppressed = false
  Type = 0
  Type2 = 0
FEATURE [PartDesign::Body] Body012  label="BodyButtonCapPorch"
  AllowCompound = false
  Group = -> [Sketch078,DatumPlane012,Pad050,Thickness009,Sketch079,AdditivePipe008,Pad051,Pocket031,Sketch080,Pocket032]
  Origin = -> Origin030
  Placement = pos=(97.71,-51.28,1.6) rot=(0,0,1;0rad)
  Tip = -> Pocket032
FEATURE [Sketcher::SketchObject] Sketch081
  ArcFitTolerance = 1e-06
  AttachmentOffset = pos=(-16.5,4,0) rot=(0,0,1;0rad)
  AttachmentSupport = -> [Pocket023]
  ExternalTypes = [0]
  FullyConstrained = false
  MakeInternals = false
  MapMode = 5
  Placement = pos=(-16.5,4,4.59) rot=(0,0,1;0rad)
  sketch-geometry (39):
    g0: BSplineCurve PolesCount=4 KnotsCount=2 Degree=3 IsPeriodic=0
    g1: BSplineCurve PolesCount=2 KnotsCount=2 Degree=1 IsPeriodic=0
    g2: BSplineCurve PolesCount=4 KnotsCount=2 Degree=3 IsPeriodic=0
    g3: BSplineCurve PolesCount=2 KnotsCount=2 Degree=1 IsPeriodic=0
    g4: BSplineCurve PolesCount=2 KnotsCount=2 Degree=1 IsPeriodic=0
    g5: BSplineCurve PolesCount=4 KnotsCount=2 Degree=3 IsPeriodic=0
    g6: BSplineCurve PolesCount=4 KnotsCount=2 Degree=3 IsPeriodic=0
    g7: BSplineCurve PolesCount=2 KnotsCount=2 Degree=1 IsPeriodic=0
    g8: BSplineCurve PolesCount=2 KnotsCount=2 Degree=1 IsPeriodic=0
    g9: BSplineCurve PolesCount=2 KnotsCount=2 Degree=1 IsPeriodic=0
    g10: BSplineCurve PolesCount=4 KnotsCount=2 Degree=3 IsPeriodic=0
    g11: BSplineCurve PolesCount=4 KnotsCount=2 Degree=3 IsPeriodic=0
    g12: BSplineCurve PolesCount=4 KnotsCount=2 Degree=3 IsPeriodic=0
    g13: BSplineCurve PolesCount=2 KnotsCount=2 Degree=1 IsPeriodic=0
    g14: BSplineCurve PolesCount=4 KnotsCount=2 Degree=3 IsPeriodic=0
    g15: BSplineCurve PolesCount=4 KnotsCount=2 Degree=3 IsPeriodic=0
    g16: BSplineCurve PolesCount=2 KnotsCount=2 Degree=1 IsPeriodic=0
    g17: BSplineCurve PolesCount=4 KnotsCount=2 Degree=3 IsPeriodic=0
    g18: BSplineCurve PolesCount=4 KnotsCount=2 Degree=3 IsPeriodic=0
    g19: BSplineCurve PolesCount=2 KnotsCount=2 Degree=1 IsPeriodic=0
    g20: BSplineCurve PolesCount=4 KnotsCount=2 Degree=3 IsPeriodic=0
    g21: BSplineCurve PolesCount=4 KnotsCount=2 Degree=3 IsPeriodic=0
    g22: BSplineCurve PolesCount=2 KnotsCount=2 Degree=1 IsPeriodic=0
    g23: BSplineCurve PolesCount=4 KnotsCount=2 Degree=3 IsPeriodic=0
    g24: BSplineCurve PolesCount=4 KnotsCount=2 Degree=3 IsPeriodic=0
    g25: BSplineCurve PolesCount=2 KnotsCount=2 Degree=1 IsPeriodic=0
    g26: BSplineCurve PolesCount=4 KnotsCount=2 Degree=3 IsPeriodic=0
    g27: BSplineCurve PolesCount=4 KnotsCount=2 Degree=3 IsPeriodic=0
    g28: BSplineCurve PolesCount=2 KnotsCount=2 Degree=1 IsPeriodic=0
    g29: BSplineCurve PolesCount=4 KnotsCount=2 Degree=3 IsPeriodic=0
    g30: BSplineCurve PolesCount=4 KnotsCount=2 Degree=3 IsPeriodic=0
    g31: BSplineCurve PolesCount=2 KnotsCount=2 Degree=1 IsPeriodic=0
    g32: BSplineCurve PolesCount=4 KnotsCount=2 Degree=3 IsPeriodic=0
    g33: BSplineCurve PolesCount=4 KnotsCount=2 Degree=3 IsPeriodic=0
    g34: BSplineCurve PolesCount=2 KnotsCount=2 Degree=1 IsPeriodic=0
    g35: BSplineCurve PolesCount=2 KnotsCount=2 Degree=1 IsPeriodic=0
    g36: BSplineCurve PolesCount=2 KnotsCount=2 Degree=1 IsPeriodic=0
    g37: BSplineCurve PolesCount=2 KnotsCount=2 Degree=1 IsPeriodic=0
    g38: BSplineCurve PolesCount=2 KnotsCount=2 Degree=1 IsPeriodic=0
  constraints (39):
    c: Coincident(g0,g1)
    c: Coincident(g1,g2)
    c: Coincident(g2,g3)
    c: Coincident(g3,g4)
    c: Coincident(g4,g5)
    c: Coincident(g5,g6)
    c: Coincident(g6,g7)
    c: Coincident(g7,g8)
    c: Coincident(g8,g9)
    c: Coincident(g9,g10)
    c: Coincident(g10,g0)
    c: Coincident(g11,g12)
    c: Coincident(g12,g13)
    c: Coincident(g13,g14)
    c: Coincident(g14,g15)
    c: Coincident(g15,g16)
    c: Coincident(g16,g17)
    c: Coincident(g17,g18)
    c: Coincident(g18,g19)
    c: Coincident(g19,g20)
    c: Coincident(g20,g21)
    c: Coincident(g21,g22)
    c: Coincident(g22,g23)
    c: Coincident(g23,g24)
    c: Coincident(g24,g25)
    c: Coincident(g25,g26)
    c: Coincident(g26,g27)
    c: Coincident(g27,g28)
    c: Coincident(g28,g29)
    c: Coincident(g29,g30)
    c: Coincident(g30,g31)
    c: Coincident(g31,g32)
    c: Coincident(g32,g33)
    c: Coincident(g33,g34)
    c: Coincident(g34,g11)
    c: Coincident(g35,g36)
    c: Coincident(g36,g37)
    c: Coincident(g37,g38)
    c: Coincident(g38,g35)
FEATURE [PartDesign::Pocket] Pocket033
  BaseFeature = -> Pocket023
  Direction = (0,0,-1)
  Length = 0.2
  Length2 = 5
  Profile = -> Sketch081
  ReferenceAxis = -> Sketch081 [N_Axis]
  Refine = true
  SideType = 0
  Suppressed = false
  Type = 0
  Type2 = 0
FEATURE [PartDesign::Body] Body008  label="BodyButtonCapKitchen"
  AllowCompound = false
  Group = -> [Sketch066,DatumPlane008,Pad042,Thickness005,Sketch067,AdditivePipe004,Pad043,Pocket023,Sketch081,Pocket033]
  Origin = -> Origin026
  Placement = pos=(97.75,-15.25,1.6) rot=(0,0,1;0rad)
  Tip = -> Pocket033
FEATURE [Sketcher::SketchObject] Sketch082  label="SketchConnectorClearance"
  ArcFitTolerance = 1e-06
  AttachmentSupport = -> [Pocket014]
  ExternalGeometry = -> [Pocket014]
  ExternalTypes = [0]
  FullyConstrained = true
  MakeInternals = false
  MapMode = 5
  Placement = pos=(0,-1.25,5e-16) rot=(1,0,0;1.5708rad)
  sketch-geometry (4):
    g0: LineSegment StartX=66.785 StartY=-3.2 StartZ=0 EndX=66.785 EndY=0 EndZ=0
    g1: LineSegment StartX=66.785 StartY=0 StartZ=0 EndX=46.785 EndY=0 EndZ=0
    g2: LineSegment StartX=46.785 StartY=0 StartZ=0 EndX=46.785 EndY=-3.2 EndZ=0
    g3: LineSegment StartX=46.785 StartY=-3.2 StartZ=0 EndX=66.785 EndY=-3.2 EndZ=0
  constraints (12):
    c: Coincident(g0,g1)
    c: Coincident(g1,g2)
    c: Coincident(g2,g3)
    c: Coincident(g3,g0)
    c: Vertical(g0)
    c: Vertical(g2)
    c: Horizontal(g1)
    c: Horizontal(g3)
    c: PointOnObject(g0,g-1)
    c: PointOnObject(g0,g-5)
    c: DistanceX(g2,g-4) = 2.5
    c: DistanceX(g-3,g0) = 2.5
FEATURE [PartDesign::Pocket] Pocket034  label="PocketConnectorClearance"
  BaseFeature = -> Pocket014
  Direction = (0,1,-2e-16)
  Length = 5
  Length2 = 5
  Profile = -> Sketch082
  ReferenceAxis = -> Sketch082 [N_Axis]
  Refine = true
  SideType = 0
  Suppressed = false
  Type = 2
  Type2 = 0
FEATURE [PartDesign::Fillet] Fillet
  Base = -> Pocket034 [Edge91,Edge94,Edge101,Edge92]
  BaseFeature = -> Pocket034
  Radius = 3
  Refine = true
  SupportTransform = false
  Suppressed = false
  UseAllEdges = false
FEATURE [PartDesign::Chamfer] Chamfer
  Angle = 45
  Base = -> Fillet [Edge1,Edge2,Edge4,Edge6,Edge8,Edge3,Edge5,Edge7]
  BaseFeature = -> Fillet
  ChamferType = 0
  FlipDirection = false
  Refine = true
  Size = 3
  Size2 = 1
  SupportTransform = false
  Suppressed = false
  UseAllEdges = false
FEATURE [Part::Part2DObjectPython] ShapeString  label="ShapeStringUnderCabinet"  # Draft 2D object (typed FeaturePython)
  FontFile = /Library/Fonts/Arial Unicode.ttf
  Fuse = false
  Justification = 6
  JustificationReference = 0
  KeepLeftMargin = false
  MakeFace = true
  ObliqueAngle = 0
  Placement = pos=(6.21,-31.23,6.18) rot=(0,0,1;0rad)
  ScaleToSize = true
  Size = 3
  String = Cabinet
  Tracking = 0
FEATURE [Part::Part2DObjectPython] ShapeString001  label="ShapeStringKitchen"  # Draft 2D object (typed FeaturePython)
  FontFile = /Library/Fonts/Arial Unicode.ttf
  Fuse = false
  Justification = 6
  JustificationReference = 0
  KeepLeftMargin = false
  MakeFace = true
  ObliqueAngle = 0
  Placement = pos=(35.75,-30.81,6.18) rot=(0,0,1;0rad)
  ScaleToSize = true
  Size = 3
  String = Kitchen
  Tracking = 0
FEATURE [Part::Part2DObjectPython] ShapeString002  label="ShapeStringEntry"  # Draft 2D object (typed FeaturePython)
  FontFile = /Library/Fonts/Arial Unicode.ttf
  Fuse = false
  Justification = 6
  JustificationReference = 0
  KeepLeftMargin = false
  MakeFace = true
  ObliqueAngle = 0
  Placement = pos=(64.9,-29.92,6.18) rot=(0,0,1;0rad)
  ScaleToSize = true
  Size = 3
  String = Entry
  Tracking = 0
FEATURE [Part::Part2DObjectPython] ShapeString003  label="ShapeStringMain"  # Draft 2D object (typed FeaturePython)
  FontFile = /Library/Fonts/Arial Unicode.ttf
  Fuse = false
  Justification = 6
  JustificationReference = 0
  KeepLeftMargin = false
  MakeFace = true
  ObliqueAngle = 0
  Placement = pos=(92.54,-30.76,6.18) rot=(0,0,1;0rad)
  ScaleToSize = true
  Size = 3
  String = Main
  Tracking = 0
FEATURE [Part::Part2DObjectPython] ShapeString004  label="ShapeStringPorch"  # Draft 2D object (typed FeaturePython)
  FontFile = /Library/Fonts/Arial Unicode.ttf
  Fuse = false
  Justification = 6
  JustificationReference = 0
  KeepLeftMargin = false
  MakeFace = true
  ObliqueAngle = 0
  Placement = pos=(9.18,-65.04,6.18) rot=(0,0,1;0rad)
  ScaleToSize = true
  Size = 3
  String = Porch
  Tracking = 0
FEATURE [Part::Part2DObjectPython] ShapeString005  label="ShapeStringTrailer"  # Draft 2D object (typed FeaturePython)
  FontFile = /Library/Fonts/Arial Unicode.ttf
  Fuse = false
  Justification = 6
  JustificationReference = 0
  KeepLeftMargin = false
  MakeFace = true
  ObliqueAngle = 0
  Placement = pos=(35.42,-65.01,6.18) rot=(0,0,1;0rad)
  ScaleToSize = true
  Size = 3
  String = Trailer
  Tracking = 0
FEATURE [Part::Part2DObjectPython] ShapeString006  label="ShapeStringWater"  # Draft 2D object (typed FeaturePython)
  FontFile = /Library/Fonts/Arial Unicode.ttf
  Fuse = false
  Justification = 6
  JustificationReference = 0
  KeepLeftMargin = false
  MakeFace = true
  ObliqueAngle = 0
  Placement = pos=(63.96,-64.76,6.18) rot=(0,0,1;0rad)
  ScaleToSize = true
  Size = 3
  String = Water
  Tracking = 0
FEATURE [Part::Part2DObjectPython] ShapeString007  label="ShapeStringPower"  # Draft 2D object (typed FeaturePython)
  FontFile = /Library/Fonts/Arial Unicode.ttf
  Fuse = false
  Justification = 6
  JustificationReference = 0
  KeepLeftMargin = false
  MakeFace = true
  ObliqueAngle = 0
  Placement = pos=(91.44,-64.52,6.18) rot=(0,0,1;0rad)
  ScaleToSize = true
  Size = 3
  String = Power
  Tracking = 0
FEATURE [PartDesign::Body] Body003  label="BodyFrontMountPcbButtonCover"
  AllowCompound = false
  Group = -> [Binder006,Sketch033,Pad024,Sketch034,Pad025,DatumPlane003,Mirrored004,Sketch040,Pad029,Pocket007,Sketch041,Pad030,Sketch042,Pad031,Sketch043,Pocket008,Binder007,Sketch048,Pad033,Sketch049,Pad034,DatumPlane,Mirrored,Sketch053,Pocket014,Sketch082,Pocket034,Fillet,Chamfer,ShapeString,ShapeString001,ShapeString002,ShapeString003,ShapeString004,ShapeString005,ShapeString006,ShapeString007]
  Origin = -> Origin013
  Tip = -> Chamfer
FEATURE [PartDesign::Fillet] Fillet001
  Base = -> Pocket012 [Edge32,Edge2,Edge66,Edge65]
  BaseFeature = -> Pocket012
  Radius = 3
  Refine = true
  SupportTransform = false
  Suppressed = false
  UseAllEdges = false
FEATURE [PartDesign::Body] Body  label="BodyCaseBack"
  AllowCompound = false
  Group = -> [Binder,Sketch,Pad,Sketch045,Pad032,Sketch046,Pocket,Sketch051,Pocket012,Fillet001]
  Origin = -> Origin021
  Placement = pos=(0,0,-12.73) rot=(0,0,1;0rad)
  Tip = -> Fillet001
FEATURE [App::Point] Origin031  label="Origin"
  Role = Origin
FEATURE [App::Point] Origin032  label="Origin"
  Role = Origin
FEATURE [App::Point] Origin033  label="Origin"
  Role = Origin
FEATURE [App::Point] Origin034  label="Origin"
  Role = Origin
FEATURE [App::Point] Origin035  label="Origin"
  Role = Origin
FEATURE [App::Point] Origin036  label="Origin"
  Role = Origin
FEATURE [App::Point] Origin037  label="Origin"
  Role = Origin
FEATURE [App::Point] Origin038  label="Origin"
  Role = Origin
FEATURE [App::Point] Origin039  label="Origin"
  Role = Origin
FEATURE [App::Point] Origin040  label="Origin"
  Role = Origin
FEATURE [App::Point] Origin041  label="Origin"
  Role = Origin
FEATURE [App::Point] Origin042  label="Origin"
  Role = Origin
FEATURE [App::Point] Origin043  label="Origin"
  Role = Origin
FEATURE [App::Point] Origin044  label="Origin"
  Role = Origin
FEATURE [App::Point] Origin045  label="Origin"
  Role = Origin
FEATURE [App::Point] Origin046  label="Origin"
  Role = Origin
FEATURE [App::Point] Origin047  label="Origin"
  Role = Origin
FEATURE [App::Point] Origin048  label="Origin"
  Role = Origin
FEATURE [App::Point] Origin049  label="Origin"
  Role = Origin
FEATURE [App::Point] Origin050  label="Origin"
  Role = Origin
FEATURE [App::Point] Origin051  label="Origin"
  Role = Origin
FEATURE [App::Point] Origin052  label="Origin"
  Role = Origin
FEATURE [App::Point] Origin053  label="Origin"
  Role = Origin
FEATURE [App::Point] Origin054  label="Origin"
  Role = Origin
